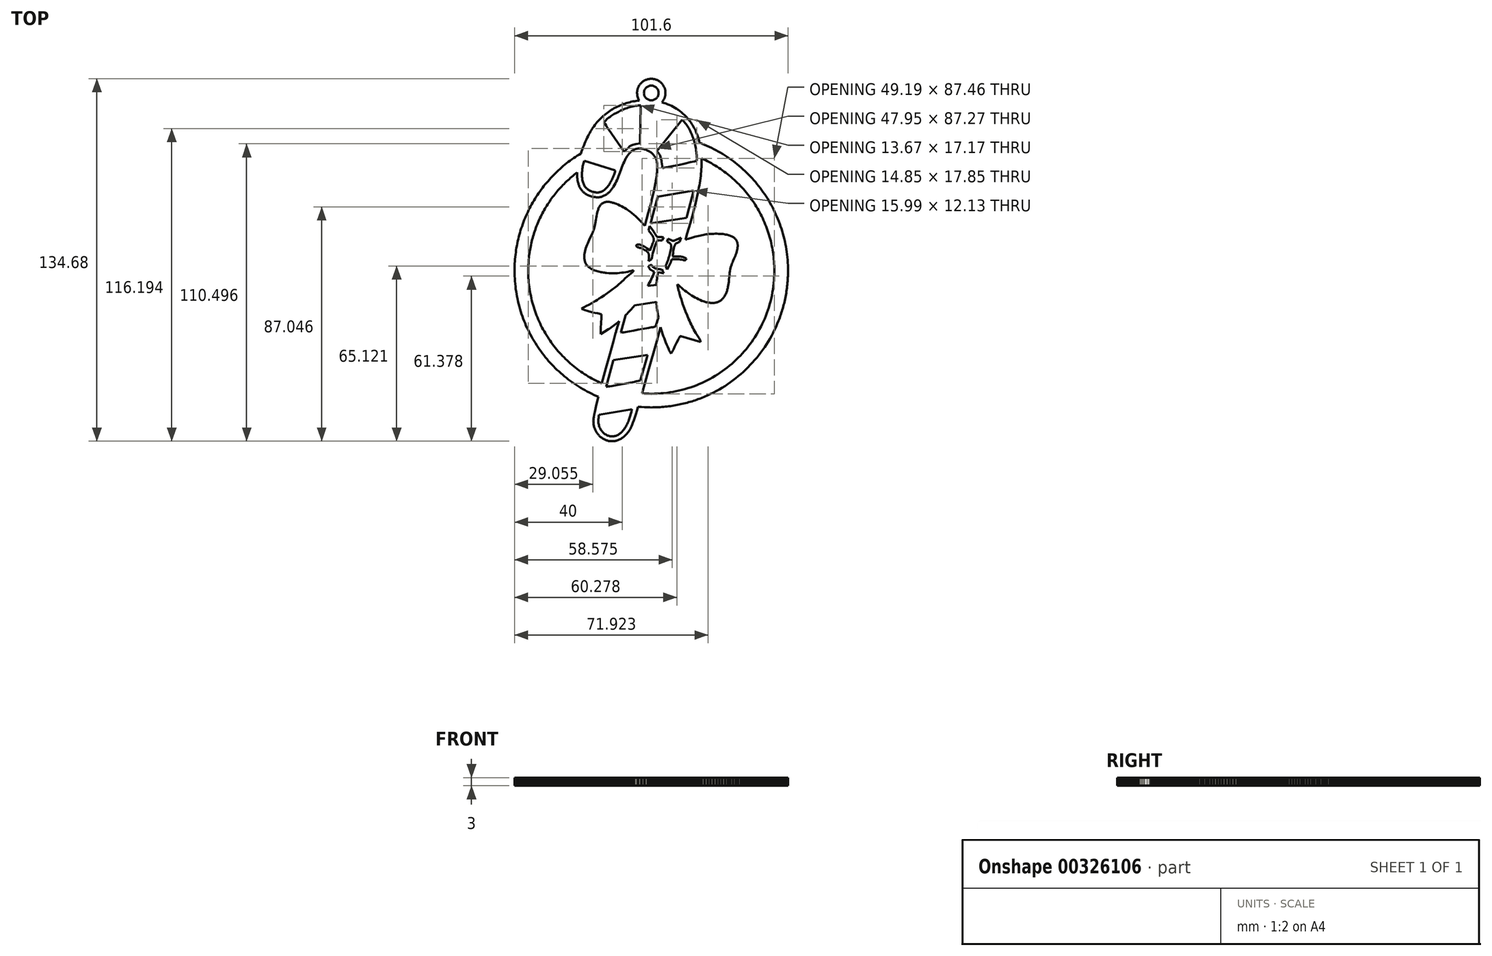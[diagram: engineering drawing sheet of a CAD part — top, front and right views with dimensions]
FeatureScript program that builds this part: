
annotation { "Feature Type Name" : "Feature", "Feature Type Description" : "" }
export const myFeature = defineFeature(function(context is Context, id is Id, definition is map)
    precondition{}
    {
        {
            var Q0;
            Q0=qCreatedBy(makeId("Top.planeOp"),FACE);
            var sketch = newSketch(context, id + "F0", { "sketchPlane" : qUnion([Q0])});
            skLineSegment(sketch, "E0", {"start": v(0.09, -1.72) * mm, "end": v(0.1, -1.8) * mm});
            skLineSegment(sketch, "E1", {"start": v(0.1, -1.8) * mm, "end": v(0.13, -1.9) * mm});
            skLineSegment(sketch, "E2", {"start": v(0.13, -1.9) * mm, "end": v(0.17, -2) * mm});
            skLineSegment(sketch, "E3", {"start": v(0.17, -2) * mm, "end": v(0.22, -2.09) * mm});
            skLineSegment(sketch, "E4", {"start": v(0.22, -2.09) * mm, "end": v(0.27, -2.18) * mm});
            skLineSegment(sketch, "E5", {"start": v(0.27, -2.18) * mm, "end": v(0.4, -2.34) * mm});
            skLineSegment(sketch, "E6", {"start": v(0.4, -2.34) * mm, "end": v(0.54, -2.5) * mm});
            skLineSegment(sketch, "E7", {"start": v(0.54, -2.5) * mm, "end": v(0.72, -2.64) * mm});
            skLineSegment(sketch, "E8", {"start": v(0.72, -2.64) * mm, "end": v(0.9, -2.77) * mm});
            skLineSegment(sketch, "E9", {"start": v(0.9, -2.77) * mm, "end": v(1.12, -2.89) * mm});
            skLineSegment(sketch, "E10", {"start": v(1.12, -2.89) * mm, "end": v(1.34, -3) * mm});
            skLineSegment(sketch, "E11", {"start": v(1.34, -3) * mm, "end": v(1.57, -3.09) * mm});
            skLineSegment(sketch, "E12", {"start": v(1.57, -3.09) * mm, "end": v(1.81, -3.17) * mm});
            skLineSegment(sketch, "E13", {"start": v(1.81, -3.17) * mm, "end": v(2.06, -3.24) * mm});
            skLineSegment(sketch, "E14", {"start": v(2.06, -3.24) * mm, "end": v(2.3, -3.3) * mm});
            skLineSegment(sketch, "E15", {"start": v(2.3, -3.3) * mm, "end": v(2.55, -3.35) * mm});
            skLineSegment(sketch, "E16", {"start": v(2.55, -3.35) * mm, "end": v(2.79, -3.4) * mm});
            skLineSegment(sketch, "E17", {"start": v(2.79, -3.4) * mm, "end": v(3.25, -3.45) * mm});
            skLineSegment(sketch, "E18", {"start": v(3.25, -3.45) * mm, "end": v(3.44, -3.46) * mm});
            skLineSegment(sketch, "E19", {"start": v(3.44, -3.46) * mm, "end": v(3.62, -3.47) * mm});
            skLineSegment(sketch, "E20", {"start": v(3.62, -3.47) * mm, "end": v(3.78, -3.46) * mm});
            skLineSegment(sketch, "E21", {"start": v(3.78, -3.46) * mm, "end": v(3.93, -3.45) * mm});
            skLineSegment(sketch, "E22", {"start": v(3.93, -3.45) * mm, "end": v(4.56, -4.93) * mm});
            skLineSegment(sketch, "E23", {"start": v(4.56, -4.93) * mm, "end": v(4.42, -4.87) * mm});
            skLineSegment(sketch, "E24", {"start": v(4.42, -4.87) * mm, "end": v(4.26, -4.82) * mm});
            skLineSegment(sketch, "E25", {"start": v(4.26, -4.82) * mm, "end": v(4.07, -4.78) * mm});
            skLineSegment(sketch, "E26", {"start": v(4.07, -4.78) * mm, "end": v(3.85, -4.74) * mm});
            skLineSegment(sketch, "E27", {"start": v(3.85, -4.74) * mm, "end": v(3.3, -4.67) * mm});
            skLineSegment(sketch, "E28", {"start": v(3.3, -4.67) * mm, "end": v(2.54, -4.6) * mm});
            skLineSegment(sketch, "E29", {"start": v(2.54, -4.6) * mm, "end": v(2.43, -5.17) * mm});
            skLineSegment(sketch, "E30", {"start": v(2.43, -5.17) * mm, "end": v(2.32, -5.74) * mm});
            skLineSegment(sketch, "E31", {"start": v(2.32, -5.74) * mm, "end": v(2.23, -6.32) * mm});
            skLineSegment(sketch, "E32", {"start": v(2.23, -6.32) * mm, "end": v(2.14, -6.9) * mm});
            skLineSegment(sketch, "E33", {"start": v(2.14, -6.9) * mm, "end": v(2.07, -7.48) * mm});
            skLineSegment(sketch, "E34", {"start": v(2.07, -7.48) * mm, "end": v(2, -8.06) * mm});
            skLineSegment(sketch, "E35", {"start": v(2, -8.06) * mm, "end": v(1.94, -8.64) * mm});
            skLineSegment(sketch, "E36", {"start": v(1.94, -8.64) * mm, "end": v(1.9, -9.23) * mm});
            skLineSegment(sketch, "E37", {"start": v(1.9, -9.23) * mm, "end": v(-1.28, -9.65) * mm});
            skLineSegment(sketch, "E38", {"start": v(-1.28, -9.65) * mm, "end": v(-0.94, -9.02) * mm});
            skLineSegment(sketch, "E39", {"start": v(-0.94, -9.02) * mm, "end": v(-0.61, -8.38) * mm});
            skLineSegment(sketch, "E40", {"start": v(-0.61, -8.38) * mm, "end": v(-0.3, -7.73) * mm});
            skLineSegment(sketch, "E41", {"start": v(-0.3, -7.73) * mm, "end": v(0.02, -7.08) * mm});
            skLineSegment(sketch, "E42", {"start": v(0.02, -7.08) * mm, "end": v(0.31, -6.43) * mm});
            skLineSegment(sketch, "E43", {"start": v(0.31, -6.43) * mm, "end": v(0.6, -5.77) * mm});
            skLineSegment(sketch, "E44", {"start": v(0.6, -5.77) * mm, "end": v(0.87, -5.1) * mm});
            skLineSegment(sketch, "E45", {"start": v(0.87, -5.1) * mm, "end": v(1.13, -4.44) * mm});
            skLineSegment(sketch, "E46", {"start": v(1.13, -4.44) * mm, "end": v(0.88, -4.27) * mm});
            skLineSegment(sketch, "E47", {"start": v(0.88, -4.27) * mm, "end": v(0.65, -4.12) * mm});
            skLineSegment(sketch, "E48", {"start": v(0.65, -4.12) * mm, "end": v(0.25, -3.88) * mm});
            skLineSegment(sketch, "E49", {"start": v(0.25, -3.88) * mm, "end": v(-0.08, -3.7) * mm});
            skLineSegment(sketch, "E50", {"start": v(-0.08, -3.7) * mm, "end": v(-0.22, -3.6) * mm});
            skLineSegment(sketch, "E51", {"start": v(-0.22, -3.6) * mm, "end": v(-0.35, -3.51) * mm});
            skLineSegment(sketch, "E52", {"start": v(-0.35, -3.51) * mm, "end": v(-0.47, -3.42) * mm});
            skLineSegment(sketch, "E53", {"start": v(-0.47, -3.42) * mm, "end": v(-0.57, -3.32) * mm});
            skLineSegment(sketch, "E54", {"start": v(-0.57, -3.32) * mm, "end": v(-0.67, -3.2) * mm});
            skLineSegment(sketch, "E55", {"start": v(-0.67, -3.2) * mm, "end": v(-0.76, -3.06) * mm});
            skLineSegment(sketch, "E56", {"start": v(-0.76, -3.06) * mm, "end": v(-0.84, -2.9) * mm});
            skLineSegment(sketch, "E57", {"start": v(-0.84, -2.9) * mm, "end": v(-0.92, -2.72) * mm});
            skLineSegment(sketch, "E58", {"start": v(-0.92, -2.72) * mm, "end": v(-1, -2.5) * mm});
            skLineSegment(sketch, "E59", {"start": v(-1, -2.5) * mm, "end": v(-1.06, -2.25) * mm});
            skLineSegment(sketch, "E60", {"start": v(-1.06, -2.25) * mm, "end": v(0.09, -1.72) * mm});
            skLineSegment(sketch, "E61", {"start": v(6.21, 7.92) * mm, "end": v(6.78, 7.62) * mm});
            skLineSegment(sketch, "E62", {"start": v(6.78, 7.62) * mm, "end": v(7.06, 7.47) * mm});
            skLineSegment(sketch, "E63", {"start": v(7.06, 7.47) * mm, "end": v(7.34, 7.34) * mm});
            skLineSegment(sketch, "E64", {"start": v(7.34, 7.34) * mm, "end": v(7.6, 7.22) * mm});
            skLineSegment(sketch, "E65", {"start": v(7.6, 7.22) * mm, "end": v(7.84, 7.14) * mm});
            skLineSegment(sketch, "E66", {"start": v(7.84, 7.14) * mm, "end": v(7.96, 7.12) * mm});
            skLineSegment(sketch, "E67", {"start": v(7.96, 7.12) * mm, "end": v(8.07, 7.1) * mm});
            skLineSegment(sketch, "E68", {"start": v(8.07, 7.1) * mm, "end": v(8.17, 7.1) * mm});
            skLineSegment(sketch, "E69", {"start": v(8.17, 7.1) * mm, "end": v(8.27, 7.12) * mm});
            skLineSegment(sketch, "E70", {"start": v(8.27, 7.12) * mm, "end": v(8.44, 7.17) * mm});
            skLineSegment(sketch, "E71", {"start": v(8.44, 7.17) * mm, "end": v(8.69, 7.27) * mm});
            skLineSegment(sketch, "E72", {"start": v(8.69, 7.27) * mm, "end": v(9.34, 7.55) * mm});
            skLineSegment(sketch, "E73", {"start": v(9.34, 7.55) * mm, "end": v(10.14, 7.92) * mm});
            skLineSegment(sketch, "E74", {"start": v(10.14, 7.92) * mm, "end": v(11.02, 8.32) * mm});
            skLineSegment(sketch, "E75", {"start": v(11.02, 8.32) * mm, "end": v(10.58, 6.79) * mm});
            skLineSegment(sketch, "E76", {"start": v(10.58, 6.79) * mm, "end": v(10.17, 6.6) * mm});
            skLineSegment(sketch, "E77", {"start": v(10.17, 6.6) * mm, "end": v(9.8, 6.43) * mm});
            skLineSegment(sketch, "E78", {"start": v(9.8, 6.43) * mm, "end": v(9.46, 6.25) * mm});
            skLineSegment(sketch, "E79", {"start": v(9.46, 6.25) * mm, "end": v(9.18, 6.08) * mm});
            skLineSegment(sketch, "E80", {"start": v(9.18, 6.08) * mm, "end": v(9.09, 6.02) * mm});
            skLineSegment(sketch, "E81", {"start": v(9.09, 6.02) * mm, "end": v(9, 5.94) * mm});
            skLineSegment(sketch, "E82", {"start": v(9, 5.94) * mm, "end": v(8.92, 5.85) * mm});
            skLineSegment(sketch, "E83", {"start": v(8.92, 5.85) * mm, "end": v(8.85, 5.75) * mm});
            skLineSegment(sketch, "E84", {"start": v(8.85, 5.75) * mm, "end": v(8.78, 5.65) * mm});
            skLineSegment(sketch, "E85", {"start": v(8.78, 5.65) * mm, "end": v(8.72, 5.53) * mm});
            skLineSegment(sketch, "E86", {"start": v(8.72, 5.53) * mm, "end": v(8.6, 5.27) * mm});
            skLineSegment(sketch, "E87", {"start": v(8.6, 5.27) * mm, "end": v(8.5, 4.98) * mm});
            skLineSegment(sketch, "E88", {"start": v(8.5, 4.98) * mm, "end": v(8.43, 4.67) * mm});
            skLineSegment(sketch, "E89", {"start": v(8.43, 4.67) * mm, "end": v(8.36, 4.33) * mm});
            skLineSegment(sketch, "E90", {"start": v(8.36, 4.33) * mm, "end": v(8.3, 3.99) * mm});
            skLineSegment(sketch, "E91", {"start": v(8.3, 3.99) * mm, "end": v(8.2, 3.27) * mm});
            skLineSegment(sketch, "E92", {"start": v(8.2, 3.27) * mm, "end": v(8.1, 2.56) * mm});
            skLineSegment(sketch, "E93", {"start": v(8.1, 2.56) * mm, "end": v(8.01, 1.9) * mm});
            skLineSegment(sketch, "E94", {"start": v(8.01, 1.9) * mm, "end": v(7.96, 1.6) * mm});
            skLineSegment(sketch, "E95", {"start": v(7.96, 1.6) * mm, "end": v(7.9, 1.32) * mm});
            skLineSegment(sketch, "E96", {"start": v(7.9, 1.32) * mm, "end": v(8.52, 1.34) * mm});
            skLineSegment(sketch, "E97", {"start": v(8.52, 1.34) * mm, "end": v(9.2, 1.35) * mm});
            skLineSegment(sketch, "E98", {"start": v(9.2, 1.35) * mm, "end": v(9.54, 1.36) * mm});
            skLineSegment(sketch, "E99", {"start": v(9.54, 1.36) * mm, "end": v(9.9, 1.35) * mm});
            skLineSegment(sketch, "E100", {"start": v(9.9, 1.35) * mm, "end": v(10.24, 1.33) * mm});
            skLineSegment(sketch, "E101", {"start": v(10.24, 1.33) * mm, "end": v(10.6, 1.3) * mm});
            skLineSegment(sketch, "E102", {"start": v(10.6, 1.3) * mm, "end": v(10.94, 1.27) * mm});
            skLineSegment(sketch, "E103", {"start": v(10.94, 1.27) * mm, "end": v(11.29, 1.22) * mm});
            skLineSegment(sketch, "E104", {"start": v(11.29, 1.22) * mm, "end": v(11.62, 1.15) * mm});
            skLineSegment(sketch, "E105", {"start": v(11.62, 1.15) * mm, "end": v(11.94, 1.06) * mm});
            skLineSegment(sketch, "E106", {"start": v(11.94, 1.06) * mm, "end": v(12.25, 0.95) * mm});
            skLineSegment(sketch, "E107", {"start": v(12.25, 0.95) * mm, "end": v(12.55, 0.82) * mm});
            skLineSegment(sketch, "E108", {"start": v(12.55, 0.82) * mm, "end": v(12.69, 0.74) * mm});
            skLineSegment(sketch, "E109", {"start": v(12.69, 0.74) * mm, "end": v(12.82, 0.66) * mm});
            skLineSegment(sketch, "E110", {"start": v(12.82, 0.66) * mm, "end": v(12.95, 0.58) * mm});
            skLineSegment(sketch, "E111", {"start": v(12.95, 0.58) * mm, "end": v(13.07, 0.48) * mm});
            skLineSegment(sketch, "E112", {"start": v(13.07, 0.48) * mm, "end": v(12.96, 0.27) * mm});
            skLineSegment(sketch, "E113", {"start": v(12.96, 0.27) * mm, "end": v(12.85, 0.11) * mm});
            skLineSegment(sketch, "E114", {"start": v(12.85, 0.11) * mm, "end": v(12.8, 0.05) * mm});
            skLineSegment(sketch, "E115", {"start": v(12.8, 0.05) * mm, "end": v(12.74, 0) * mm});
            skLineSegment(sketch, "E116", {"start": v(12.74, 0) * mm, "end": v(12.68, -0.03) * mm});
            skLineSegment(sketch, "E117", {"start": v(12.68, -0.03) * mm, "end": v(12.61, -0.06) * mm});
            skLineSegment(sketch, "E118", {"start": v(12.61, -0.06) * mm, "end": v(12.55, -0.08) * mm});
            skLineSegment(sketch, "E119", {"start": v(12.55, -0.08) * mm, "end": v(12.47, -0.09) * mm});
            skLineSegment(sketch, "E120", {"start": v(12.47, -0.09) * mm, "end": v(12.3, -0.08) * mm});
            skLineSegment(sketch, "E121", {"start": v(12.3, -0.08) * mm, "end": v(12.1, -0.06) * mm});
            skLineSegment(sketch, "E122", {"start": v(12.1, -0.06) * mm, "end": v(11.86, -0.01) * mm});
            skLineSegment(sketch, "E123", {"start": v(11.86, -0.01) * mm, "end": v(11.23, 0.1) * mm});
            skLineSegment(sketch, "E124", {"start": v(11.23, 0.1) * mm, "end": v(10.83, 0.17) * mm});
            skLineSegment(sketch, "E125", {"start": v(10.83, 0.17) * mm, "end": v(10.35, 0.23) * mm});
            skLineSegment(sketch, "E126", {"start": v(10.35, 0.23) * mm, "end": v(9.8, 0.27) * mm});
            skLineSegment(sketch, "E127", {"start": v(9.8, 0.27) * mm, "end": v(9.16, 0.3) * mm});
            skLineSegment(sketch, "E128", {"start": v(9.16, 0.3) * mm, "end": v(8.44, 0.29) * mm});
            skLineSegment(sketch, "E129", {"start": v(8.44, 0.29) * mm, "end": v(8.03, 0.27) * mm});
            skLineSegment(sketch, "E130", {"start": v(8.03, 0.27) * mm, "end": v(7.6, 0.25) * mm});
            skLineSegment(sketch, "E131", {"start": v(7.6, 0.25) * mm, "end": v(7.4, -0.37) * mm});
            skLineSegment(sketch, "E132", {"start": v(7.4, -0.37) * mm, "end": v(7.2, -0.9) * mm});
            skLineSegment(sketch, "E133", {"start": v(7.2, -0.9) * mm, "end": v(6.98, -1.39) * mm});
            skLineSegment(sketch, "E134", {"start": v(6.98, -1.39) * mm, "end": v(6.77, -1.82) * mm});
            skLineSegment(sketch, "E135", {"start": v(6.77, -1.82) * mm, "end": v(6.34, -2.65) * mm});
            skLineSegment(sketch, "E136", {"start": v(6.34, -2.65) * mm, "end": v(5.87, -3.5) * mm});
            skLineSegment(sketch, "E137", {"start": v(5.87, -3.5) * mm, "end": v(5.3, -2.17) * mm});
            skLineSegment(sketch, "E138", {"start": v(5.3, -2.17) * mm, "end": v(5.56, -1.66) * mm});
            skLineSegment(sketch, "E139", {"start": v(5.56, -1.66) * mm, "end": v(5.7, -1.37) * mm});
            skLineSegment(sketch, "E140", {"start": v(5.7, -1.37) * mm, "end": v(5.85, -1) * mm});
            skLineSegment(sketch, "E141", {"start": v(5.85, -1) * mm, "end": v(6.02, -0.57) * mm});
            skLineSegment(sketch, "E142", {"start": v(6.02, -0.57) * mm, "end": v(6.19, -0.08) * mm});
            skLineSegment(sketch, "E143", {"start": v(6.19, -0.08) * mm, "end": v(6.37, 0.44) * mm});
            skLineSegment(sketch, "E144", {"start": v(6.37, 0.44) * mm, "end": v(6.54, 1) * mm});
            skLineSegment(sketch, "E145", {"start": v(6.54, 1) * mm, "end": v(6.71, 1.58) * mm});
            skLineSegment(sketch, "E146", {"start": v(6.71, 1.58) * mm, "end": v(6.87, 2.17) * mm});
            skLineSegment(sketch, "E147", {"start": v(6.87, 2.17) * mm, "end": v(7.02, 2.75) * mm});
            skLineSegment(sketch, "E148", {"start": v(7.02, 2.75) * mm, "end": v(7.15, 3.32) * mm});
            skLineSegment(sketch, "E149", {"start": v(7.15, 3.32) * mm, "end": v(7.25, 3.87) * mm});
            skLineSegment(sketch, "E150", {"start": v(7.25, 3.87) * mm, "end": v(7.32, 4.38) * mm});
            skLineSegment(sketch, "E151", {"start": v(7.32, 4.38) * mm, "end": v(7.35, 4.62) * mm});
            skLineSegment(sketch, "E152", {"start": v(7.35, 4.62) * mm, "end": v(7.36, 4.84) * mm});
            skLineSegment(sketch, "E153", {"start": v(7.36, 4.84) * mm, "end": v(7.37, 5.05) * mm});
            skLineSegment(sketch, "E154", {"start": v(7.37, 5.05) * mm, "end": v(7.37, 5.24) * mm});
            skLineSegment(sketch, "E155", {"start": v(7.37, 5.24) * mm, "end": v(7.36, 5.42) * mm});
            skLineSegment(sketch, "E156", {"start": v(7.36, 5.42) * mm, "end": v(7.33, 5.58) * mm});
            skLineSegment(sketch, "E157", {"start": v(7.33, 5.58) * mm, "end": v(7.3, 5.72) * mm});
            skLineSegment(sketch, "E158", {"start": v(7.3, 5.72) * mm, "end": v(7.25, 5.83) * mm});
            skLineSegment(sketch, "E159", {"start": v(7.25, 5.83) * mm, "end": v(7.2, 5.9) * mm});
            skLineSegment(sketch, "E160", {"start": v(7.2, 5.9) * mm, "end": v(7.15, 5.98) * mm});
            skLineSegment(sketch, "E161", {"start": v(7.15, 5.98) * mm, "end": v(7.03, 6.12) * mm});
            skLineSegment(sketch, "E162", {"start": v(7.03, 6.12) * mm, "end": v(6.87, 6.25) * mm});
            skLineSegment(sketch, "E163", {"start": v(6.87, 6.25) * mm, "end": v(6.7, 6.38) * mm});
            skLineSegment(sketch, "E164", {"start": v(6.7, 6.38) * mm, "end": v(6.5, 6.5) * mm});
            skLineSegment(sketch, "E165", {"start": v(6.5, 6.5) * mm, "end": v(6.29, 6.6) * mm});
            skLineSegment(sketch, "E166", {"start": v(6.29, 6.6) * mm, "end": v(6.06, 6.71) * mm});
            skLineSegment(sketch, "E167", {"start": v(6.06, 6.71) * mm, "end": v(5.83, 6.8) * mm});
            skLineSegment(sketch, "E168", {"start": v(5.83, 6.8) * mm, "end": v(6.21, 7.92) * mm});
            skLineSegment(sketch, "E169", {"start": v(2.62, -21.33) * mm, "end": v(1.71, -24.54) * mm});
            skLineSegment(sketch, "E170", {"start": v(1.71, -24.54) * mm, "end": v(1.6, -24.62) * mm});
            skLineSegment(sketch, "E171", {"start": v(1.6, -24.62) * mm, "end": v(1.49, -24.69) * mm});
            skLineSegment(sketch, "E172", {"start": v(1.49, -24.69) * mm, "end": v(1.37, -24.74) * mm});
            skLineSegment(sketch, "E173", {"start": v(1.37, -24.74) * mm, "end": v(1.25, -24.8) * mm});
            skLineSegment(sketch, "E174", {"start": v(1.25, -24.8) * mm, "end": v(1.13, -24.84) * mm});
            skLineSegment(sketch, "E175", {"start": v(1.13, -24.84) * mm, "end": v(1, -24.87) * mm});
            skLineSegment(sketch, "E176", {"start": v(1, -24.87) * mm, "end": v(0.7, -24.93) * mm});
            skLineSegment(sketch, "E177", {"start": v(0.7, -24.93) * mm, "end": v(-0.03, -25.04) * mm});
            skLineSegment(sketch, "E178", {"start": v(-0.03, -25.04) * mm, "end": v(-0.5, -25.1) * mm});
            skLineSegment(sketch, "E179", {"start": v(-0.5, -25.1) * mm, "end": v(-1.05, -25.2) * mm});
            skLineSegment(sketch, "E180", {"start": v(-1.05, -25.2) * mm, "end": v(-3.34, -25.63) * mm});
            skLineSegment(sketch, "E181", {"start": v(-3.34, -25.63) * mm, "end": v(-4.9, -25.93) * mm});
            skLineSegment(sketch, "E182", {"start": v(-4.9, -25.93) * mm, "end": v(-6.54, -26.24) * mm});
            skLineSegment(sketch, "E183", {"start": v(-6.54, -26.24) * mm, "end": v(-8.14, -26.53) * mm});
            skLineSegment(sketch, "E184", {"start": v(-8.14, -26.53) * mm, "end": v(-9.56, -26.77) * mm});
            skLineSegment(sketch, "E185", {"start": v(-9.56, -26.77) * mm, "end": v(-10.16, -26.86) * mm});
            skLineSegment(sketch, "E186", {"start": v(-10.16, -26.86) * mm, "end": v(-10.66, -26.92) * mm});
            skLineSegment(sketch, "E187", {"start": v(-10.66, -26.92) * mm, "end": v(-11.05, -26.95) * mm});
            skLineSegment(sketch, "E188", {"start": v(-11.05, -26.95) * mm, "end": v(-11.2, -26.96) * mm});
            skLineSegment(sketch, "E189", {"start": v(-11.2, -26.96) * mm, "end": v(-11.3, -26.95) * mm});
            skLineSegment(sketch, "E190", {"start": v(-11.3, -26.95) * mm, "end": v(-9.46, -20.43) * mm});
            skLineSegment(sketch, "E191", {"start": v(-9.46, -20.43) * mm, "end": v(-9.03, -20) * mm});
            skLineSegment(sketch, "E192", {"start": v(-9.03, -20) * mm, "end": v(-8.6, -19.57) * mm});
            skLineSegment(sketch, "E193", {"start": v(-8.6, -19.57) * mm, "end": v(-8.19, -19.13) * mm});
            skLineSegment(sketch, "E194", {"start": v(-8.19, -19.13) * mm, "end": v(-7.77, -18.68) * mm});
            skLineSegment(sketch, "E195", {"start": v(-7.77, -18.68) * mm, "end": v(-7.36, -18.23) * mm});
            skLineSegment(sketch, "E196", {"start": v(-7.36, -18.23) * mm, "end": v(-6.96, -17.77) * mm});
            skLineSegment(sketch, "E197", {"start": v(-6.96, -17.77) * mm, "end": v(-6.56, -17.3) * mm});
            skLineSegment(sketch, "E198", {"start": v(-6.56, -17.3) * mm, "end": v(-6.17, -16.83) * mm});
            skLineSegment(sketch, "E199", {"start": v(-6.17, -16.83) * mm, "end": v(1.87, -15.61) * mm});
            skLineSegment(sketch, "E200", {"start": v(1.87, -15.61) * mm, "end": v(1.92, -16.33) * mm});
            skLineSegment(sketch, "E201", {"start": v(1.92, -16.33) * mm, "end": v(2, -17.05) * mm});
            skLineSegment(sketch, "E202", {"start": v(2, -17.05) * mm, "end": v(2.07, -17.77) * mm});
            skLineSegment(sketch, "E203", {"start": v(2.07, -17.77) * mm, "end": v(2.16, -18.49) * mm});
            skLineSegment(sketch, "E204", {"start": v(2.16, -18.49) * mm, "end": v(2.26, -19.2) * mm});
            skLineSegment(sketch, "E205", {"start": v(2.26, -19.2) * mm, "end": v(2.37, -19.91) * mm});
            skLineSegment(sketch, "E206", {"start": v(2.37, -19.91) * mm, "end": v(2.49, -20.62) * mm});
            skLineSegment(sketch, "E207", {"start": v(2.49, -20.62) * mm, "end": v(2.62, -21.33) * mm});
            skLineSegment(sketch, "E208", {"start": v(-1.63, -36.34) * mm, "end": v(-1.35, -35.33) * mm});
            skLineSegment(sketch, "E209", {"start": v(-1.35, -35.33) * mm, "end": v(-14.05, -37.2) * mm});
            skLineSegment(sketch, "E210", {"start": v(-14.05, -37.2) * mm, "end": v(-16.7, -47.05) * mm});
            skLineSegment(sketch, "E211", {"start": v(-16.7, -47.05) * mm, "end": v(-16.62, -47.06) * mm});
            skLineSegment(sketch, "E212", {"start": v(-16.62, -47.06) * mm, "end": v(-16.47, -47.06) * mm});
            skLineSegment(sketch, "E213", {"start": v(-16.47, -47.06) * mm, "end": v(-16.03, -47.01) * mm});
            skLineSegment(sketch, "E214", {"start": v(-16.03, -47.01) * mm, "end": v(-15.4, -46.93) * mm});
            skLineSegment(sketch, "E215", {"start": v(-15.4, -46.93) * mm, "end": v(-14.61, -46.8) * mm});
            skLineSegment(sketch, "E216", {"start": v(-14.61, -46.8) * mm, "end": v(-12.7, -46.48) * mm});
            skLineSegment(sketch, "E217", {"start": v(-12.7, -46.48) * mm, "end": v(-10.53, -46.09) * mm});
            skLineSegment(sketch, "E218", {"start": v(-10.53, -46.09) * mm, "end": v(-8.34, -45.67) * mm});
            skLineSegment(sketch, "E219", {"start": v(-8.34, -45.67) * mm, "end": v(-6.37, -45.27) * mm});
            skLineSegment(sketch, "E220", {"start": v(-6.37, -45.27) * mm, "end": v(-5.54, -45.1) * mm});
            skLineSegment(sketch, "E221", {"start": v(-5.54, -45.1) * mm, "end": v(-4.86, -44.95) * mm});
            skLineSegment(sketch, "E222", {"start": v(-4.86, -44.95) * mm, "end": v(-4.35, -44.82) * mm});
            skLineSegment(sketch, "E223", {"start": v(-4.35, -44.82) * mm, "end": v(-4.04, -44.73) * mm});
            skLineSegment(sketch, "E224", {"start": v(-4.04, -44.73) * mm, "end": v(-1.63, -36.34) * mm});
            skLineSegment(sketch, "E225", {"start": v(-19.42, -57.55) * mm, "end": v(-19.52, -58.08) * mm});
            skLineSegment(sketch, "E226", {"start": v(-19.52, -58.08) * mm, "end": v(-19.6, -58.6) * mm});
            skLineSegment(sketch, "E227", {"start": v(-19.6, -58.6) * mm, "end": v(-19.64, -59.1) * mm});
            skLineSegment(sketch, "E228", {"start": v(-19.64, -59.1) * mm, "end": v(-19.66, -59.58) * mm});
            skLineSegment(sketch, "E229", {"start": v(-19.66, -59.58) * mm, "end": v(-19.65, -60.04) * mm});
            skLineSegment(sketch, "E230", {"start": v(-19.65, -60.04) * mm, "end": v(-19.62, -60.48) * mm});
            skLineSegment(sketch, "E231", {"start": v(-19.62, -60.48) * mm, "end": v(-19.56, -60.9) * mm});
            skLineSegment(sketch, "E232", {"start": v(-19.56, -60.9) * mm, "end": v(-19.47, -61.32) * mm});
            skLineSegment(sketch, "E233", {"start": v(-19.47, -61.32) * mm, "end": v(-19.37, -61.7) * mm});
            skLineSegment(sketch, "E234", {"start": v(-19.37, -61.7) * mm, "end": v(-19.24, -62.08) * mm});
            skLineSegment(sketch, "E235", {"start": v(-19.24, -62.08) * mm, "end": v(-19.1, -62.43) * mm});
            skLineSegment(sketch, "E236", {"start": v(-19.1, -62.43) * mm, "end": v(-18.93, -62.76) * mm});
            skLineSegment(sketch, "E237", {"start": v(-18.93, -62.76) * mm, "end": v(-18.74, -63.08) * mm});
            skLineSegment(sketch, "E238", {"start": v(-18.74, -63.08) * mm, "end": v(-18.54, -63.37) * mm});
            skLineSegment(sketch, "E239", {"start": v(-18.54, -63.37) * mm, "end": v(-18.33, -63.65) * mm});
            skLineSegment(sketch, "E240", {"start": v(-18.33, -63.65) * mm, "end": v(-18.1, -63.9) * mm});
            skLineSegment(sketch, "E241", {"start": v(-18.1, -63.9) * mm, "end": v(-17.86, -64.15) * mm});
            skLineSegment(sketch, "E242", {"start": v(-17.86, -64.15) * mm, "end": v(-17.61, -64.37) * mm});
            skLineSegment(sketch, "E243", {"start": v(-17.61, -64.37) * mm, "end": v(-17.35, -64.57) * mm});
            skLineSegment(sketch, "E244", {"start": v(-17.35, -64.57) * mm, "end": v(-17.08, -64.75) * mm});
            skLineSegment(sketch, "E245", {"start": v(-17.08, -64.75) * mm, "end": v(-16.8, -64.91) * mm});
            skLineSegment(sketch, "E246", {"start": v(-16.8, -64.91) * mm, "end": v(-16.52, -65.06) * mm});
            skLineSegment(sketch, "E247", {"start": v(-16.52, -65.06) * mm, "end": v(-16.23, -65.18) * mm});
            skLineSegment(sketch, "E248", {"start": v(-16.23, -65.18) * mm, "end": v(-15.93, -65.29) * mm});
            skLineSegment(sketch, "E249", {"start": v(-15.93, -65.29) * mm, "end": v(-15.63, -65.37) * mm});
            skLineSegment(sketch, "E250", {"start": v(-15.63, -65.37) * mm, "end": v(-15.34, -65.44) * mm});
            skLineSegment(sketch, "E251", {"start": v(-15.34, -65.44) * mm, "end": v(-15.04, -65.49) * mm});
            skLineSegment(sketch, "E252", {"start": v(-15.04, -65.49) * mm, "end": v(-14.74, -65.52) * mm});
            skLineSegment(sketch, "E253", {"start": v(-14.74, -65.52) * mm, "end": v(-14.44, -65.52) * mm});
            skLineSegment(sketch, "E254", {"start": v(-14.44, -65.52) * mm, "end": v(-14.15, -65.51) * mm});
            skLineSegment(sketch, "E255", {"start": v(-14.15, -65.51) * mm, "end": v(-13.86, -65.48) * mm});
            skLineSegment(sketch, "E256", {"start": v(-13.86, -65.48) * mm, "end": v(-13.58, -65.43) * mm});
            skLineSegment(sketch, "E257", {"start": v(-13.58, -65.43) * mm, "end": v(-13.26, -65.35) * mm});
            skLineSegment(sketch, "E258", {"start": v(-13.26, -65.35) * mm, "end": v(-12.95, -65.24) * mm});
            skLineSegment(sketch, "E259", {"start": v(-12.95, -65.24) * mm, "end": v(-12.65, -65.11) * mm});
            skLineSegment(sketch, "E260", {"start": v(-12.65, -65.11) * mm, "end": v(-12.35, -64.96) * mm});
            skLineSegment(sketch, "E261", {"start": v(-12.35, -64.96) * mm, "end": v(-12.07, -64.8) * mm});
            skLineSegment(sketch, "E262", {"start": v(-12.07, -64.8) * mm, "end": v(-11.79, -64.6) * mm});
            skLineSegment(sketch, "E263", {"start": v(-11.79, -64.6) * mm, "end": v(-11.52, -64.4) * mm});
            skLineSegment(sketch, "E264", {"start": v(-11.52, -64.4) * mm, "end": v(-11.25, -64.17) * mm});
            skLineSegment(sketch, "E265", {"start": v(-11.25, -64.17) * mm, "end": v(-11, -63.93) * mm});
            skLineSegment(sketch, "E266", {"start": v(-11, -63.93) * mm, "end": v(-10.75, -63.67) * mm});
            skLineSegment(sketch, "E267", {"start": v(-10.75, -63.67) * mm, "end": v(-10.51, -63.4) * mm});
            skLineSegment(sketch, "E268", {"start": v(-10.51, -63.4) * mm, "end": v(-10.28, -63.1) * mm});
            skLineSegment(sketch, "E269", {"start": v(-10.28, -63.1) * mm, "end": v(-10.06, -62.8) * mm});
            skLineSegment(sketch, "E270", {"start": v(-10.06, -62.8) * mm, "end": v(-9.84, -62.5) * mm});
            skLineSegment(sketch, "E271", {"start": v(-9.84, -62.5) * mm, "end": v(-9.63, -62.16) * mm});
            skLineSegment(sketch, "E272", {"start": v(-9.63, -62.16) * mm, "end": v(-9.43, -61.82) * mm});
            skLineSegment(sketch, "E273", {"start": v(-9.43, -61.82) * mm, "end": v(-9.24, -61.47) * mm});
            skLineSegment(sketch, "E274", {"start": v(-9.24, -61.47) * mm, "end": v(-9.05, -61.11) * mm});
            skLineSegment(sketch, "E275", {"start": v(-9.05, -61.11) * mm, "end": v(-8.87, -60.74) * mm});
            skLineSegment(sketch, "E276", {"start": v(-8.87, -60.74) * mm, "end": v(-8.7, -60.36) * mm});
            skLineSegment(sketch, "E277", {"start": v(-8.7, -60.36) * mm, "end": v(-8.54, -59.98) * mm});
            skLineSegment(sketch, "E278", {"start": v(-8.54, -59.98) * mm, "end": v(-8.38, -59.59) * mm});
            skLineSegment(sketch, "E279", {"start": v(-8.38, -59.59) * mm, "end": v(-8.23, -59.2) * mm});
            skLineSegment(sketch, "E280", {"start": v(-8.23, -59.2) * mm, "end": v(-8.09, -58.79) * mm});
            skLineSegment(sketch, "E281", {"start": v(-8.09, -58.79) * mm, "end": v(-7.95, -58.38) * mm});
            skLineSegment(sketch, "E282", {"start": v(-7.95, -58.38) * mm, "end": v(-7.82, -57.97) * mm});
            skLineSegment(sketch, "E283", {"start": v(-7.82, -57.97) * mm, "end": v(-7.59, -57.14) * mm});
            skLineSegment(sketch, "E284", {"start": v(-7.59, -57.14) * mm, "end": v(-7.38, -56.31) * mm});
            skLineSegment(sketch, "E285", {"start": v(-7.38, -56.31) * mm, "end": v(-7.2, -55.48) * mm});
            skLineSegment(sketch, "E286", {"start": v(-7.2, -55.48) * mm, "end": v(-19.42, -57.55) * mm});
            skLineSegment(sketch, "E287", {"start": v(-0.56, 12.57) * mm, "end": v(-0.15, 12.03) * mm});
            skLineSegment(sketch, "E288", {"start": v(-0.15, 12.03) * mm, "end": v(0.21, 11.51) * mm});
            skLineSegment(sketch, "E289", {"start": v(0.21, 11.51) * mm, "end": v(0.85, 10.54) * mm});
            skLineSegment(sketch, "E290", {"start": v(0.85, 10.54) * mm, "end": v(1.16, 10.05) * mm});
            skLineSegment(sketch, "E291", {"start": v(1.16, 10.05) * mm, "end": v(1.49, 9.56) * mm});
            skLineSegment(sketch, "E292", {"start": v(1.49, 9.56) * mm, "end": v(1.84, 9.06) * mm});
            skLineSegment(sketch, "E293", {"start": v(1.84, 9.06) * mm, "end": v(2.24, 8.53) * mm});
            skLineSegment(sketch, "E294", {"start": v(2.24, 8.53) * mm, "end": v(2.84, 8.5) * mm});
            skLineSegment(sketch, "E295", {"start": v(2.84, 8.5) * mm, "end": v(3.4, 8.5) * mm});
            skLineSegment(sketch, "E296", {"start": v(3.4, 8.5) * mm, "end": v(3.95, 8.49) * mm});
            skLineSegment(sketch, "E297", {"start": v(3.95, 8.49) * mm, "end": v(4.23, 8.47) * mm});
            skLineSegment(sketch, "E298", {"start": v(4.23, 8.47) * mm, "end": v(4.52, 8.43) * mm});
            skLineSegment(sketch, "E299", {"start": v(4.52, 8.43) * mm, "end": v(4.1, 7.24) * mm});
            skLineSegment(sketch, "E300", {"start": v(4.1, 7.24) * mm, "end": v(3.48, 7.3) * mm});
            skLineSegment(sketch, "E301", {"start": v(3.48, 7.3) * mm, "end": v(3.22, 7.33) * mm});
            skLineSegment(sketch, "E302", {"start": v(3.22, 7.33) * mm, "end": v(3, 7.34) * mm});
            skLineSegment(sketch, "E303", {"start": v(3, 7.34) * mm, "end": v(2.8, 7.33) * mm});
            skLineSegment(sketch, "E304", {"start": v(2.8, 7.33) * mm, "end": v(2.63, 7.32) * mm});
            skLineSegment(sketch, "E305", {"start": v(2.63, 7.32) * mm, "end": v(2.49, 7.28) * mm});
            skLineSegment(sketch, "E306", {"start": v(2.49, 7.28) * mm, "end": v(2.36, 7.22) * mm});
            skLineSegment(sketch, "E307", {"start": v(2.36, 7.22) * mm, "end": v(2.25, 7.14) * mm});
            skLineSegment(sketch, "E308", {"start": v(2.25, 7.14) * mm, "end": v(2.15, 7.03) * mm});
            skLineSegment(sketch, "E309", {"start": v(2.15, 7.03) * mm, "end": v(2.05, 6.9) * mm});
            skLineSegment(sketch, "E310", {"start": v(2.05, 6.9) * mm, "end": v(1.96, 6.73) * mm});
            skLineSegment(sketch, "E311", {"start": v(1.96, 6.73) * mm, "end": v(1.87, 6.54) * mm});
            skLineSegment(sketch, "E312", {"start": v(1.87, 6.54) * mm, "end": v(1.77, 6.3) * mm});
            skLineSegment(sketch, "E313", {"start": v(1.77, 6.3) * mm, "end": v(1.56, 5.73) * mm});
            skLineSegment(sketch, "E314", {"start": v(1.56, 5.73) * mm, "end": v(1.38, 5.22) * mm});
            skLineSegment(sketch, "E315", {"start": v(1.38, 5.22) * mm, "end": v(1.18, 4.63) * mm});
            skLineSegment(sketch, "E316", {"start": v(1.18, 4.63) * mm, "end": v(0.97, 3.97) * mm});
            skLineSegment(sketch, "E317", {"start": v(0.97, 3.97) * mm, "end": v(0.77, 3.25) * mm});
            skLineSegment(sketch, "E318", {"start": v(0.77, 3.25) * mm, "end": v(0.57, 2.5) * mm});
            skLineSegment(sketch, "E319", {"start": v(0.57, 2.5) * mm, "end": v(0.39, 1.73) * mm});
            skLineSegment(sketch, "E320", {"start": v(0.39, 1.73) * mm, "end": v(0.23, 0.97) * mm});
            skLineSegment(sketch, "E321", {"start": v(0.23, 0.97) * mm, "end": v(0.17, 0.6) * mm});
            skLineSegment(sketch, "E322", {"start": v(0.17, 0.6) * mm, "end": v(0.12, 0.24) * mm});
            skLineSegment(sketch, "E323", {"start": v(0.12, 0.24) * mm, "end": v(-1.02, -0.3) * mm});
            skLineSegment(sketch, "E324", {"start": v(-1.02, -0.3) * mm, "end": v(-0.93, 0.58) * mm});
            skLineSegment(sketch, "E325", {"start": v(-0.93, 0.58) * mm, "end": v(-0.9, 0.95) * mm});
            skLineSegment(sketch, "E326", {"start": v(-0.9, 0.95) * mm, "end": v(-0.87, 1.3) * mm});
            skLineSegment(sketch, "E327", {"start": v(-0.87, 1.3) * mm, "end": v(-0.86, 1.6) * mm});
            skLineSegment(sketch, "E328", {"start": v(-0.86, 1.6) * mm, "end": v(-0.88, 1.88) * mm});
            skLineSegment(sketch, "E329", {"start": v(-0.88, 1.88) * mm, "end": v(-0.92, 2.13) * mm});
            skLineSegment(sketch, "E330", {"start": v(-0.92, 2.13) * mm, "end": v(-0.95, 2.25) * mm});
            skLineSegment(sketch, "E331", {"start": v(-0.95, 2.25) * mm, "end": v(-0.98, 2.36) * mm});
            skLineSegment(sketch, "E332", {"start": v(-0.98, 2.36) * mm, "end": v(-1.03, 2.47) * mm});
            skLineSegment(sketch, "E333", {"start": v(-1.03, 2.47) * mm, "end": v(-1.08, 2.58) * mm});
            skLineSegment(sketch, "E334", {"start": v(-1.08, 2.58) * mm, "end": v(-1.14, 2.68) * mm});
            skLineSegment(sketch, "E335", {"start": v(-1.14, 2.68) * mm, "end": v(-1.2, 2.78) * mm});
            skLineSegment(sketch, "E336", {"start": v(-1.2, 2.78) * mm, "end": v(-1.28, 2.88) * mm});
            skLineSegment(sketch, "E337", {"start": v(-1.28, 2.88) * mm, "end": v(-1.37, 2.98) * mm});
            skLineSegment(sketch, "E338", {"start": v(-1.37, 2.98) * mm, "end": v(-1.58, 3.17) * mm});
            skLineSegment(sketch, "E339", {"start": v(-1.58, 3.17) * mm, "end": v(-1.83, 3.37) * mm});
            skLineSegment(sketch, "E340", {"start": v(-1.83, 3.37) * mm, "end": v(-2.12, 3.56) * mm});
            skLineSegment(sketch, "E341", {"start": v(-2.12, 3.56) * mm, "end": v(-2.47, 3.77) * mm});
            skLineSegment(sketch, "E342", {"start": v(-2.47, 3.77) * mm, "end": v(-2.87, 3.99) * mm});
            skLineSegment(sketch, "E343", {"start": v(-2.87, 3.99) * mm, "end": v(-3.23, 4.16) * mm});
            skLineSegment(sketch, "E344", {"start": v(-3.23, 4.16) * mm, "end": v(-3.54, 4.3) * mm});
            skLineSegment(sketch, "E345", {"start": v(-3.54, 4.3) * mm, "end": v(-3.87, 4.42) * mm});
            skLineSegment(sketch, "E346", {"start": v(-3.87, 4.42) * mm, "end": v(-4.25, 4.54) * mm});
            skLineSegment(sketch, "E347", {"start": v(-4.25, 4.54) * mm, "end": v(-4.6, 4.64) * mm});
            skLineSegment(sketch, "E348", {"start": v(-4.6, 4.64) * mm, "end": v(-4.86, 4.7) * mm});
            skLineSegment(sketch, "E349", {"start": v(-4.86, 4.7) * mm, "end": v(-5.07, 4.76) * mm});
            skLineSegment(sketch, "E350", {"start": v(-5.07, 4.76) * mm, "end": v(-5.16, 4.78) * mm});
            skLineSegment(sketch, "E351", {"start": v(-5.16, 4.78) * mm, "end": v(-5.23, 4.81) * mm});
            skLineSegment(sketch, "E352", {"start": v(-5.23, 4.81) * mm, "end": v(-5.3, 4.85) * mm});
            skLineSegment(sketch, "E353", {"start": v(-5.3, 4.85) * mm, "end": v(-5.36, 4.9) * mm});
            skLineSegment(sketch, "E354", {"start": v(-5.36, 4.9) * mm, "end": v(-5.4, 4.95) * mm});
            skLineSegment(sketch, "E355", {"start": v(-5.4, 4.95) * mm, "end": v(-5.45, 5.02) * mm});
            skLineSegment(sketch, "E356", {"start": v(-5.45, 5.02) * mm, "end": v(-5.5, 5.1) * mm});
            skLineSegment(sketch, "E357", {"start": v(-5.5, 5.1) * mm, "end": v(-5.53, 5.2) * mm});
            skLineSegment(sketch, "E358", {"start": v(-5.53, 5.2) * mm, "end": v(-5.61, 5.48) * mm});
            skLineSegment(sketch, "E359", {"start": v(-5.61, 5.48) * mm, "end": v(-5.48, 5.57) * mm});
            skLineSegment(sketch, "E360", {"start": v(-5.48, 5.57) * mm, "end": v(-5.34, 5.64) * mm});
            skLineSegment(sketch, "E361", {"start": v(-5.34, 5.64) * mm, "end": v(-5.2, 5.7) * mm});
            skLineSegment(sketch, "E362", {"start": v(-5.2, 5.7) * mm, "end": v(-5.05, 5.74) * mm});
            skLineSegment(sketch, "E363", {"start": v(-5.05, 5.74) * mm, "end": v(-4.89, 5.76) * mm});
            skLineSegment(sketch, "E364", {"start": v(-4.89, 5.76) * mm, "end": v(-4.72, 5.76) * mm});
            skLineSegment(sketch, "E365", {"start": v(-4.72, 5.76) * mm, "end": v(-4.55, 5.75) * mm});
            skLineSegment(sketch, "E366", {"start": v(-4.55, 5.75) * mm, "end": v(-4.38, 5.73) * mm});
            skLineSegment(sketch, "E367", {"start": v(-4.38, 5.73) * mm, "end": v(-4.2, 5.7) * mm});
            skLineSegment(sketch, "E368", {"start": v(-4.2, 5.7) * mm, "end": v(-4.02, 5.65) * mm});
            skLineSegment(sketch, "E369", {"start": v(-4.02, 5.65) * mm, "end": v(-3.83, 5.6) * mm});
            skLineSegment(sketch, "E370", {"start": v(-3.83, 5.6) * mm, "end": v(-3.65, 5.52) * mm});
            skLineSegment(sketch, "E371", {"start": v(-3.65, 5.52) * mm, "end": v(-3.27, 5.36) * mm});
            skLineSegment(sketch, "E372", {"start": v(-3.27, 5.36) * mm, "end": v(-2.9, 5.17) * mm});
            skLineSegment(sketch, "E373", {"start": v(-2.9, 5.17) * mm, "end": v(-2.52, 4.96) * mm});
            skLineSegment(sketch, "E374", {"start": v(-2.52, 4.96) * mm, "end": v(-2.16, 4.73) * mm});
            skLineSegment(sketch, "E375", {"start": v(-2.16, 4.73) * mm, "end": v(-1.8, 4.5) * mm});
            skLineSegment(sketch, "E376", {"start": v(-1.8, 4.5) * mm, "end": v(-1.48, 4.27) * mm});
            skLineSegment(sketch, "E377", {"start": v(-1.48, 4.27) * mm, "end": v(-0.9, 3.85) * mm});
            skLineSegment(sketch, "E378", {"start": v(-0.9, 3.85) * mm, "end": v(-0.45, 3.52) * mm});
            skLineSegment(sketch, "E379", {"start": v(-0.45, 3.52) * mm, "end": v(-0.34, 3.9) * mm});
            skLineSegment(sketch, "E380", {"start": v(-0.34, 3.9) * mm, "end": v(-0.23, 4.24) * mm});
            skLineSegment(sketch, "E381", {"start": v(-0.23, 4.24) * mm, "end": v(-0.01, 4.87) * mm});
            skLineSegment(sketch, "E382", {"start": v(-0.01, 4.87) * mm, "end": v(0.2, 5.4) * mm});
            skLineSegment(sketch, "E383", {"start": v(0.2, 5.4) * mm, "end": v(0.4, 5.87) * mm});
            skLineSegment(sketch, "E384", {"start": v(0.4, 5.87) * mm, "end": v(0.58, 6.27) * mm});
            skLineSegment(sketch, "E385", {"start": v(0.58, 6.27) * mm, "end": v(0.73, 6.63) * mm});
            skLineSegment(sketch, "E386", {"start": v(0.73, 6.63) * mm, "end": v(0.79, 6.8) * mm});
            skLineSegment(sketch, "E387", {"start": v(0.79, 6.8) * mm, "end": v(0.84, 6.96) * mm});
            skLineSegment(sketch, "E388", {"start": v(0.84, 6.96) * mm, "end": v(0.88, 7.12) * mm});
            skLineSegment(sketch, "E389", {"start": v(0.88, 7.12) * mm, "end": v(0.9, 7.28) * mm});
            skLineSegment(sketch, "E390", {"start": v(0.9, 7.28) * mm, "end": v(0.92, 7.44) * mm});
            skLineSegment(sketch, "E391", {"start": v(0.92, 7.44) * mm, "end": v(0.93, 7.6) * mm});
            skLineSegment(sketch, "E392", {"start": v(0.93, 7.6) * mm, "end": v(0.91, 7.76) * mm});
            skLineSegment(sketch, "E393", {"start": v(0.91, 7.76) * mm, "end": v(0.89, 7.93) * mm});
            skLineSegment(sketch, "E394", {"start": v(0.89, 7.93) * mm, "end": v(0.84, 8.1) * mm});
            skLineSegment(sketch, "E395", {"start": v(0.84, 8.1) * mm, "end": v(0.78, 8.28) * mm});
            skLineSegment(sketch, "E396", {"start": v(0.78, 8.28) * mm, "end": v(0.7, 8.48) * mm});
            skLineSegment(sketch, "E397", {"start": v(0.7, 8.48) * mm, "end": v(0.6, 8.68) * mm});
            skLineSegment(sketch, "E398", {"start": v(0.6, 8.68) * mm, "end": v(0.48, 8.9) * mm});
            skLineSegment(sketch, "E399", {"start": v(0.48, 8.9) * mm, "end": v(0.33, 9.14) * mm});
            skLineSegment(sketch, "E400", {"start": v(0.33, 9.14) * mm, "end": v(0.17, 9.39) * mm});
            skLineSegment(sketch, "E401", {"start": v(0.17, 9.39) * mm, "end": v(-0.02, 9.66) * mm});
            skLineSegment(sketch, "E402", {"start": v(-0.02, 9.66) * mm, "end": v(-0.46, 10.27) * mm});
            skLineSegment(sketch, "E403", {"start": v(-0.46, 10.27) * mm, "end": v(-1.01, 10.98) * mm});
            skLineSegment(sketch, "E404", {"start": v(-1.01, 10.98) * mm, "end": v(-0.56, 12.57) * mm});
            skLineSegment(sketch, "E405", {"start": v(0, 67.34) * mm, "end": v(0.27, 67.33) * mm});
            skLineSegment(sketch, "E406", {"start": v(0.27, 67.33) * mm, "end": v(0.54, 67.3) * mm});
            skLineSegment(sketch, "E407", {"start": v(0.54, 67.3) * mm, "end": v(0.8, 67.28) * mm});
            skLineSegment(sketch, "E408", {"start": v(0.8, 67.28) * mm, "end": v(1.06, 67.23) * mm});
            skLineSegment(sketch, "E409", {"start": v(1.06, 67.23) * mm, "end": v(1.32, 67.17) * mm});
            skLineSegment(sketch, "E410", {"start": v(1.32, 67.17) * mm, "end": v(1.57, 67.1) * mm});
            skLineSegment(sketch, "E411", {"start": v(1.57, 67.1) * mm, "end": v(1.81, 67.02) * mm});
            skLineSegment(sketch, "E412", {"start": v(1.81, 67.02) * mm, "end": v(2.05, 66.92) * mm});
            skLineSegment(sketch, "E413", {"start": v(2.05, 66.92) * mm, "end": v(2.28, 66.82) * mm});
            skLineSegment(sketch, "E414", {"start": v(2.28, 66.82) * mm, "end": v(2.51, 66.7) * mm});
            skLineSegment(sketch, "E415", {"start": v(2.51, 66.7) * mm, "end": v(2.73, 66.57) * mm});
            skLineSegment(sketch, "E416", {"start": v(2.73, 66.57) * mm, "end": v(2.94, 66.44) * mm});
            skLineSegment(sketch, "E417", {"start": v(2.94, 66.44) * mm, "end": v(3.15, 66.3) * mm});
            skLineSegment(sketch, "E418", {"start": v(3.15, 66.3) * mm, "end": v(3.35, 66.13) * mm});
            skLineSegment(sketch, "E419", {"start": v(3.35, 66.13) * mm, "end": v(3.54, 65.97) * mm});
            skLineSegment(sketch, "E420", {"start": v(3.54, 65.97) * mm, "end": v(3.72, 65.8) * mm});
            skLineSegment(sketch, "E421", {"start": v(3.72, 65.8) * mm, "end": v(3.9, 65.61) * mm});
            skLineSegment(sketch, "E422", {"start": v(3.9, 65.61) * mm, "end": v(4.06, 65.42) * mm});
            skLineSegment(sketch, "E423", {"start": v(4.06, 65.42) * mm, "end": v(4.22, 65.22) * mm});
            skLineSegment(sketch, "E424", {"start": v(4.22, 65.22) * mm, "end": v(4.37, 65.01) * mm});
            skLineSegment(sketch, "E425", {"start": v(4.37, 65.01) * mm, "end": v(4.5, 64.8) * mm});
            skLineSegment(sketch, "E426", {"start": v(4.5, 64.8) * mm, "end": v(4.63, 64.58) * mm});
            skLineSegment(sketch, "E427", {"start": v(4.63, 64.58) * mm, "end": v(4.75, 64.35) * mm});
            skLineSegment(sketch, "E428", {"start": v(4.75, 64.35) * mm, "end": v(4.85, 64.12) * mm});
            skLineSegment(sketch, "E429", {"start": v(4.85, 64.12) * mm, "end": v(4.95, 63.88) * mm});
            skLineSegment(sketch, "E430", {"start": v(4.95, 63.88) * mm, "end": v(5.03, 63.64) * mm});
            skLineSegment(sketch, "E431", {"start": v(5.03, 63.64) * mm, "end": v(5.1, 63.39) * mm});
            skLineSegment(sketch, "E432", {"start": v(5.1, 63.39) * mm, "end": v(5.16, 63.13) * mm});
            skLineSegment(sketch, "E433", {"start": v(5.16, 63.13) * mm, "end": v(5.2, 62.87) * mm});
            skLineSegment(sketch, "E434", {"start": v(5.2, 62.87) * mm, "end": v(5.24, 62.6) * mm});
            skLineSegment(sketch, "E435", {"start": v(5.24, 62.6) * mm, "end": v(5.26, 62.34) * mm});
            skLineSegment(sketch, "E436", {"start": v(5.26, 62.34) * mm, "end": v(5.27, 62.07) * mm});
            skLineSegment(sketch, "E437", {"start": v(5.27, 62.07) * mm, "end": v(5.26, 61.82) * mm});
            skLineSegment(sketch, "E438", {"start": v(5.26, 61.82) * mm, "end": v(5.24, 61.58) * mm});
            skLineSegment(sketch, "E439", {"start": v(5.24, 61.58) * mm, "end": v(5.22, 61.33) * mm});
            skLineSegment(sketch, "E440", {"start": v(5.22, 61.33) * mm, "end": v(5.18, 61.1) * mm});
            skLineSegment(sketch, "E441", {"start": v(5.18, 61.1) * mm, "end": v(5.13, 60.86) * mm});
            skLineSegment(sketch, "E442", {"start": v(5.13, 60.86) * mm, "end": v(5.07, 60.63) * mm});
            skLineSegment(sketch, "E443", {"start": v(5.07, 60.63) * mm, "end": v(5, 60.4) * mm});
            skLineSegment(sketch, "E444", {"start": v(5, 60.4) * mm, "end": v(4.92, 60.18) * mm});
            skLineSegment(sketch, "E445", {"start": v(4.92, 60.18) * mm, "end": v(4.83, 59.96) * mm});
            skLineSegment(sketch, "E446", {"start": v(4.83, 59.96) * mm, "end": v(4.73, 59.75) * mm});
            skLineSegment(sketch, "E447", {"start": v(4.73, 59.75) * mm, "end": v(4.62, 59.54) * mm});
            skLineSegment(sketch, "E448", {"start": v(4.62, 59.54) * mm, "end": v(4.5, 59.34) * mm});
            skLineSegment(sketch, "E449", {"start": v(4.5, 59.34) * mm, "end": v(4.38, 59.14) * mm});
            skLineSegment(sketch, "E450", {"start": v(4.38, 59.14) * mm, "end": v(4.25, 58.95) * mm});
            skLineSegment(sketch, "E451", {"start": v(4.25, 58.95) * mm, "end": v(4.1, 58.77) * mm});
            skLineSegment(sketch, "E452", {"start": v(4.1, 58.77) * mm, "end": v(3.96, 58.6) * mm});
            skLineSegment(sketch, "E453", {"start": v(3.96, 58.6) * mm, "end": v(4.68, 58.38) * mm});
            skLineSegment(sketch, "E454", {"start": v(4.68, 58.38) * mm, "end": v(5.4, 58.14) * mm});
            skLineSegment(sketch, "E455", {"start": v(5.4, 58.14) * mm, "end": v(6.1, 57.87) * mm});
            skLineSegment(sketch, "E456", {"start": v(6.1, 57.87) * mm, "end": v(6.8, 57.58) * mm});
            skLineSegment(sketch, "E457", {"start": v(6.8, 57.58) * mm, "end": v(7.49, 57.26) * mm});
            skLineSegment(sketch, "E458", {"start": v(7.49, 57.26) * mm, "end": v(8.16, 56.91) * mm});
            skLineSegment(sketch, "E459", {"start": v(8.16, 56.91) * mm, "end": v(8.82, 56.54) * mm});
            skLineSegment(sketch, "E460", {"start": v(8.82, 56.54) * mm, "end": v(9.46, 56.15) * mm});
            skLineSegment(sketch, "E461", {"start": v(9.46, 56.15) * mm, "end": v(9.78, 55.94) * mm});
            skLineSegment(sketch, "E462", {"start": v(9.78, 55.94) * mm, "end": v(10.09, 55.72) * mm});
            skLineSegment(sketch, "E463", {"start": v(10.09, 55.72) * mm, "end": v(10.4, 55.5) * mm});
            skLineSegment(sketch, "E464", {"start": v(10.4, 55.5) * mm, "end": v(10.7, 55.28) * mm});
            skLineSegment(sketch, "E465", {"start": v(10.7, 55.28) * mm, "end": v(11, 55.04) * mm});
            skLineSegment(sketch, "E466", {"start": v(11, 55.04) * mm, "end": v(11.3, 54.8) * mm});
            skLineSegment(sketch, "E467", {"start": v(11.3, 54.8) * mm, "end": v(11.59, 54.56) * mm});
            skLineSegment(sketch, "E468", {"start": v(11.59, 54.56) * mm, "end": v(11.87, 54.3) * mm});
            skLineSegment(sketch, "E469", {"start": v(11.87, 54.3) * mm, "end": v(12.15, 54.04) * mm});
            skLineSegment(sketch, "E470", {"start": v(12.15, 54.04) * mm, "end": v(12.43, 53.78) * mm});
            skLineSegment(sketch, "E471", {"start": v(12.43, 53.78) * mm, "end": v(12.7, 53.5) * mm});
            skLineSegment(sketch, "E472", {"start": v(12.7, 53.5) * mm, "end": v(12.97, 53.22) * mm});
            skLineSegment(sketch, "E473", {"start": v(12.97, 53.22) * mm, "end": v(13.23, 52.94) * mm});
            skLineSegment(sketch, "E474", {"start": v(13.23, 52.94) * mm, "end": v(13.48, 52.64) * mm});
            skLineSegment(sketch, "E475", {"start": v(13.48, 52.64) * mm, "end": v(13.74, 52.34) * mm});
            skLineSegment(sketch, "E476", {"start": v(13.74, 52.34) * mm, "end": v(13.98, 52.04) * mm});
            skLineSegment(sketch, "E477", {"start": v(13.98, 52.04) * mm, "end": v(14.35, 51.56) * mm});
            skLineSegment(sketch, "E478", {"start": v(14.35, 51.56) * mm, "end": v(14.7, 51.07) * mm});
            skLineSegment(sketch, "E479", {"start": v(14.7, 51.07) * mm, "end": v(15.03, 50.57) * mm});
            skLineSegment(sketch, "E480", {"start": v(15.03, 50.57) * mm, "end": v(15.35, 50.07) * mm});
            skLineSegment(sketch, "E481", {"start": v(15.35, 50.07) * mm, "end": v(15.65, 49.56) * mm});
            skLineSegment(sketch, "E482", {"start": v(15.65, 49.56) * mm, "end": v(15.93, 49.04) * mm});
            skLineSegment(sketch, "E483", {"start": v(15.93, 49.04) * mm, "end": v(16.2, 48.52) * mm});
            skLineSegment(sketch, "E484", {"start": v(16.2, 48.52) * mm, "end": v(16.46, 48) * mm});
            skLineSegment(sketch, "E485", {"start": v(16.46, 48) * mm, "end": v(16.7, 47.46) * mm});
            skLineSegment(sketch, "E486", {"start": v(16.7, 47.46) * mm, "end": v(16.92, 46.92) * mm});
            skLineSegment(sketch, "E487", {"start": v(16.92, 46.92) * mm, "end": v(17.13, 46.37) * mm});
            skLineSegment(sketch, "E488", {"start": v(17.13, 46.37) * mm, "end": v(17.32, 45.82) * mm});
            skLineSegment(sketch, "E489", {"start": v(17.32, 45.82) * mm, "end": v(17.5, 45.26) * mm});
            skLineSegment(sketch, "E490", {"start": v(17.5, 45.26) * mm, "end": v(17.67, 44.7) * mm});
            skLineSegment(sketch, "E491", {"start": v(17.67, 44.7) * mm, "end": v(17.83, 44.13) * mm});
            skLineSegment(sketch, "E492", {"start": v(17.83, 44.13) * mm, "end": v(17.97, 43.56) * mm});
            skLineSegment(sketch, "E493", {"start": v(17.97, 43.56) * mm, "end": v(18.86, 43.2) * mm});
            skLineSegment(sketch, "E494", {"start": v(18.86, 43.2) * mm, "end": v(19.75, 42.84) * mm});
            skLineSegment(sketch, "E495", {"start": v(19.75, 42.84) * mm, "end": v(20.63, 42.46) * mm});
            skLineSegment(sketch, "E496", {"start": v(20.63, 42.46) * mm, "end": v(21.5, 42.07) * mm});
            skLineSegment(sketch, "E497", {"start": v(21.5, 42.07) * mm, "end": v(22.36, 41.65) * mm});
            skLineSegment(sketch, "E498", {"start": v(22.36, 41.65) * mm, "end": v(23.21, 41.22) * mm});
            skLineSegment(sketch, "E499", {"start": v(23.21, 41.22) * mm, "end": v(24.05, 40.78) * mm});
            skLineSegment(sketch, "E500", {"start": v(24.05, 40.78) * mm, "end": v(24.89, 40.32) * mm});
            skLineSegment(sketch, "E501", {"start": v(24.89, 40.32) * mm, "end": v(25.71, 39.85) * mm});
            skLineSegment(sketch, "E502", {"start": v(25.71, 39.85) * mm, "end": v(26.52, 39.36) * mm});
            skLineSegment(sketch, "E503", {"start": v(26.52, 39.36) * mm, "end": v(27.33, 38.86) * mm});
            skLineSegment(sketch, "E504", {"start": v(27.33, 38.86) * mm, "end": v(28.12, 38.34) * mm});
            skLineSegment(sketch, "E505", {"start": v(28.12, 38.34) * mm, "end": v(28.9, 37.8) * mm});
            skLineSegment(sketch, "E506", {"start": v(28.9, 37.8) * mm, "end": v(29.68, 37.26) * mm});
            skLineSegment(sketch, "E507", {"start": v(29.68, 37.26) * mm, "end": v(30.44, 36.7) * mm});
            skLineSegment(sketch, "E508", {"start": v(30.44, 36.7) * mm, "end": v(31.2, 36.12) * mm});
            skLineSegment(sketch, "E509", {"start": v(31.2, 36.12) * mm, "end": v(31.93, 35.54) * mm});
            skLineSegment(sketch, "E510", {"start": v(31.93, 35.54) * mm, "end": v(32.66, 34.94) * mm});
            skLineSegment(sketch, "E511", {"start": v(32.66, 34.94) * mm, "end": v(33.38, 34.32) * mm});
            skLineSegment(sketch, "E512", {"start": v(33.38, 34.32) * mm, "end": v(34.08, 33.7) * mm});
            skLineSegment(sketch, "E513", {"start": v(34.08, 33.7) * mm, "end": v(34.78, 33.05) * mm});
            skLineSegment(sketch, "E514", {"start": v(34.78, 33.05) * mm, "end": v(35.46, 32.4) * mm});
            skLineSegment(sketch, "E515", {"start": v(35.46, 32.4) * mm, "end": v(36.13, 31.74) * mm});
            skLineSegment(sketch, "E516", {"start": v(36.13, 31.74) * mm, "end": v(36.79, 31.06) * mm});
            skLineSegment(sketch, "E517", {"start": v(36.79, 31.06) * mm, "end": v(37.43, 30.37) * mm});
            skLineSegment(sketch, "E518", {"start": v(37.43, 30.37) * mm, "end": v(38.06, 29.67) * mm});
            skLineSegment(sketch, "E519", {"start": v(38.06, 29.67) * mm, "end": v(38.68, 28.96) * mm});
            skLineSegment(sketch, "E520", {"start": v(38.68, 28.96) * mm, "end": v(39.29, 28.23) * mm});
            skLineSegment(sketch, "E521", {"start": v(39.29, 28.23) * mm, "end": v(39.88, 27.5) * mm});
            skLineSegment(sketch, "E522", {"start": v(39.88, 27.5) * mm, "end": v(40.46, 26.75) * mm});
            skLineSegment(sketch, "E523", {"start": v(40.46, 26.75) * mm, "end": v(41.03, 25.99) * mm});
            skLineSegment(sketch, "E524", {"start": v(41.03, 25.99) * mm, "end": v(41.58, 25.22) * mm});
            skLineSegment(sketch, "E525", {"start": v(41.58, 25.22) * mm, "end": v(42.12, 24.44) * mm});
            skLineSegment(sketch, "E526", {"start": v(42.12, 24.44) * mm, "end": v(42.64, 23.65) * mm});
            skLineSegment(sketch, "E527", {"start": v(42.64, 23.65) * mm, "end": v(43.15, 22.85) * mm});
            skLineSegment(sketch, "E528", {"start": v(43.15, 22.85) * mm, "end": v(43.64, 22.04) * mm});
            skLineSegment(sketch, "E529", {"start": v(43.64, 22.04) * mm, "end": v(44.12, 21.22) * mm});
            skLineSegment(sketch, "E530", {"start": v(44.12, 21.22) * mm, "end": v(44.59, 20.4) * mm});
            skLineSegment(sketch, "E531", {"start": v(44.59, 20.4) * mm, "end": v(45.04, 19.55) * mm});
            skLineSegment(sketch, "E532", {"start": v(45.04, 19.55) * mm, "end": v(45.47, 18.7) * mm});
            skLineSegment(sketch, "E533", {"start": v(45.47, 18.7) * mm, "end": v(45.89, 17.85) * mm});
            skLineSegment(sketch, "E534", {"start": v(45.89, 17.85) * mm, "end": v(46.3, 16.98) * mm});
            skLineSegment(sketch, "E535", {"start": v(46.3, 16.98) * mm, "end": v(46.68, 16.1) * mm});
            skLineSegment(sketch, "E536", {"start": v(46.68, 16.1) * mm, "end": v(47.05, 15.22) * mm});
            skLineSegment(sketch, "E537", {"start": v(47.05, 15.22) * mm, "end": v(47.4, 14.33) * mm});
            skLineSegment(sketch, "E538", {"start": v(47.4, 14.33) * mm, "end": v(47.74, 13.43) * mm});
            skLineSegment(sketch, "E539", {"start": v(47.74, 13.43) * mm, "end": v(48.06, 12.52) * mm});
            skLineSegment(sketch, "E540", {"start": v(48.06, 12.52) * mm, "end": v(48.37, 11.6) * mm});
            skLineSegment(sketch, "E541", {"start": v(48.37, 11.6) * mm, "end": v(48.66, 10.68) * mm});
            skLineSegment(sketch, "E542", {"start": v(48.66, 10.68) * mm, "end": v(48.93, 9.75) * mm});
            skLineSegment(sketch, "E543", {"start": v(48.93, 9.75) * mm, "end": v(49.18, 8.8) * mm});
            skLineSegment(sketch, "E544", {"start": v(49.18, 8.8) * mm, "end": v(49.41, 7.86) * mm});
            skLineSegment(sketch, "E545", {"start": v(49.41, 7.86) * mm, "end": v(49.63, 6.91) * mm});
            skLineSegment(sketch, "E546", {"start": v(49.63, 6.91) * mm, "end": v(49.83, 5.95) * mm});
            skLineSegment(sketch, "E547", {"start": v(49.83, 5.95) * mm, "end": v(50.01, 4.99) * mm});
            skLineSegment(sketch, "E548", {"start": v(50.01, 4.99) * mm, "end": v(50.18, 4.01) * mm});
            skLineSegment(sketch, "E549", {"start": v(50.18, 4.01) * mm, "end": v(50.32, 3.03) * mm});
            skLineSegment(sketch, "E550", {"start": v(50.32, 3.03) * mm, "end": v(50.45, 2.05) * mm});
            skLineSegment(sketch, "E551", {"start": v(50.45, 2.05) * mm, "end": v(50.55, 1.06) * mm});
            skLineSegment(sketch, "E552", {"start": v(50.55, 1.06) * mm, "end": v(50.64, 0.06) * mm});
            skLineSegment(sketch, "E553", {"start": v(50.64, 0.06) * mm, "end": v(50.71, -0.94) * mm});
            skLineSegment(sketch, "E554", {"start": v(50.71, -0.94) * mm, "end": v(50.76, -1.94) * mm});
            skLineSegment(sketch, "E555", {"start": v(50.76, -1.94) * mm, "end": v(50.8, -2.95) * mm});
            skLineSegment(sketch, "E556", {"start": v(50.8, -2.95) * mm, "end": v(50.8, -3.97) * mm});
            skLineSegment(sketch, "E557", {"start": v(50.8, -3.97) * mm, "end": v(50.8, -4.63) * mm});
            skLineSegment(sketch, "E558", {"start": v(50.8, -4.63) * mm, "end": v(50.78, -5.28) * mm});
            skLineSegment(sketch, "E559", {"start": v(50.78, -5.28) * mm, "end": v(50.76, -5.93) * mm});
            skLineSegment(sketch, "E560", {"start": v(50.76, -5.93) * mm, "end": v(50.73, -6.58) * mm});
            skLineSegment(sketch, "E561", {"start": v(50.73, -6.58) * mm, "end": v(50.7, -7.23) * mm});
            skLineSegment(sketch, "E562", {"start": v(50.7, -7.23) * mm, "end": v(50.65, -7.88) * mm});
            skLineSegment(sketch, "E563", {"start": v(50.65, -7.88) * mm, "end": v(50.6, -8.52) * mm});
            skLineSegment(sketch, "E564", {"start": v(50.6, -8.52) * mm, "end": v(50.54, -9.16) * mm});
            skLineSegment(sketch, "E565", {"start": v(50.54, -9.16) * mm, "end": v(50.47, -9.8) * mm});
            skLineSegment(sketch, "E566", {"start": v(50.47, -9.8) * mm, "end": v(50.4, -10.44) * mm});
            skLineSegment(sketch, "E567", {"start": v(50.4, -10.44) * mm, "end": v(50.3, -11.07) * mm});
            skLineSegment(sketch, "E568", {"start": v(50.3, -11.07) * mm, "end": v(50.21, -11.7) * mm});
            skLineSegment(sketch, "E569", {"start": v(50.21, -11.7) * mm, "end": v(50.11, -12.34) * mm});
            skLineSegment(sketch, "E570", {"start": v(50.11, -12.34) * mm, "end": v(50, -12.96) * mm});
            skLineSegment(sketch, "E571", {"start": v(50, -12.96) * mm, "end": v(49.9, -13.59) * mm});
            skLineSegment(sketch, "E572", {"start": v(49.9, -13.59) * mm, "end": v(49.77, -14.2) * mm});
            skLineSegment(sketch, "E573", {"start": v(49.77, -14.2) * mm, "end": v(49.64, -14.83) * mm});
            skLineSegment(sketch, "E574", {"start": v(49.64, -14.83) * mm, "end": v(49.5, -15.44) * mm});
            skLineSegment(sketch, "E575", {"start": v(49.5, -15.44) * mm, "end": v(49.35, -16.06) * mm});
            skLineSegment(sketch, "E576", {"start": v(49.35, -16.06) * mm, "end": v(49.2, -16.67) * mm});
            skLineSegment(sketch, "E577", {"start": v(49.2, -16.67) * mm, "end": v(49.04, -17.27) * mm});
            skLineSegment(sketch, "E578", {"start": v(49.04, -17.27) * mm, "end": v(48.87, -17.88) * mm});
            skLineSegment(sketch, "E579", {"start": v(48.87, -17.88) * mm, "end": v(48.7, -18.48) * mm});
            skLineSegment(sketch, "E580", {"start": v(48.7, -18.48) * mm, "end": v(48.52, -19.08) * mm});
            skLineSegment(sketch, "E581", {"start": v(48.52, -19.08) * mm, "end": v(48.33, -19.67) * mm});
            skLineSegment(sketch, "E582", {"start": v(48.33, -19.67) * mm, "end": v(48.13, -20.26) * mm});
            skLineSegment(sketch, "E583", {"start": v(48.13, -20.26) * mm, "end": v(47.93, -20.85) * mm});
            skLineSegment(sketch, "E584", {"start": v(47.93, -20.85) * mm, "end": v(47.72, -21.44) * mm});
            skLineSegment(sketch, "E585", {"start": v(47.72, -21.44) * mm, "end": v(47.5, -22.02) * mm});
            skLineSegment(sketch, "E586", {"start": v(47.5, -22.02) * mm, "end": v(47.28, -22.6) * mm});
            skLineSegment(sketch, "E587", {"start": v(47.28, -22.6) * mm, "end": v(46.8, -23.74) * mm});
            skLineSegment(sketch, "E588", {"start": v(46.8, -23.74) * mm, "end": v(46.31, -24.88) * mm});
            skLineSegment(sketch, "E589", {"start": v(46.31, -24.88) * mm, "end": v(45.8, -26) * mm});
            skLineSegment(sketch, "E590", {"start": v(45.8, -26) * mm, "end": v(45.24, -27.1) * mm});
            skLineSegment(sketch, "E591", {"start": v(45.24, -27.1) * mm, "end": v(44.67, -28.18) * mm});
            skLineSegment(sketch, "E592", {"start": v(44.67, -28.18) * mm, "end": v(44.07, -29.26) * mm});
            skLineSegment(sketch, "E593", {"start": v(44.07, -29.26) * mm, "end": v(43.45, -30.31) * mm});
            skLineSegment(sketch, "E594", {"start": v(43.45, -30.31) * mm, "end": v(42.8, -31.35) * mm});
            skLineSegment(sketch, "E595", {"start": v(42.8, -31.35) * mm, "end": v(42.12, -32.37) * mm});
            skLineSegment(sketch, "E596", {"start": v(42.12, -32.37) * mm, "end": v(41.43, -33.38) * mm});
            skLineSegment(sketch, "E597", {"start": v(41.43, -33.38) * mm, "end": v(40.7, -34.36) * mm});
            skLineSegment(sketch, "E598", {"start": v(40.7, -34.36) * mm, "end": v(39.97, -35.33) * mm});
            skLineSegment(sketch, "E599", {"start": v(39.97, -35.33) * mm, "end": v(39.2, -36.28) * mm});
            skLineSegment(sketch, "E600", {"start": v(39.2, -36.28) * mm, "end": v(38.41, -37.22) * mm});
            skLineSegment(sketch, "E601", {"start": v(38.41, -37.22) * mm, "end": v(37.6, -38.13) * mm});
            skLineSegment(sketch, "E602", {"start": v(37.6, -38.13) * mm, "end": v(36.77, -39.02) * mm});
            skLineSegment(sketch, "E603", {"start": v(36.77, -39.02) * mm, "end": v(35.92, -39.9) * mm});
            skLineSegment(sketch, "E604", {"start": v(35.92, -39.9) * mm, "end": v(35.05, -40.74) * mm});
            skLineSegment(sketch, "E605", {"start": v(35.05, -40.74) * mm, "end": v(34.16, -41.57) * mm});
            skLineSegment(sketch, "E606", {"start": v(34.16, -41.57) * mm, "end": v(33.24, -42.38) * mm});
            skLineSegment(sketch, "E607", {"start": v(33.24, -42.38) * mm, "end": v(32.31, -43.17) * mm});
            skLineSegment(sketch, "E608", {"start": v(32.31, -43.17) * mm, "end": v(31.36, -43.94) * mm});
            skLineSegment(sketch, "E609", {"start": v(31.36, -43.94) * mm, "end": v(30.4, -44.68) * mm});
            skLineSegment(sketch, "E610", {"start": v(30.4, -44.68) * mm, "end": v(29.4, -45.4) * mm});
            skLineSegment(sketch, "E611", {"start": v(29.4, -45.4) * mm, "end": v(28.4, -46.1) * mm});
            skLineSegment(sketch, "E612", {"start": v(28.4, -46.1) * mm, "end": v(27.38, -46.77) * mm});
            skLineSegment(sketch, "E613", {"start": v(27.38, -46.77) * mm, "end": v(26.34, -47.42) * mm});
            skLineSegment(sketch, "E614", {"start": v(26.34, -47.42) * mm, "end": v(25.29, -48.04) * mm});
            skLineSegment(sketch, "E615", {"start": v(25.29, -48.04) * mm, "end": v(24.21, -48.64) * mm});
            skLineSegment(sketch, "E616", {"start": v(24.21, -48.64) * mm, "end": v(23.13, -49.21) * mm});
            skLineSegment(sketch, "E617", {"start": v(23.13, -49.21) * mm, "end": v(22.02, -49.76) * mm});
            skLineSegment(sketch, "E618", {"start": v(22.02, -49.76) * mm, "end": v(20.9, -50.28) * mm});
            skLineSegment(sketch, "E619", {"start": v(20.9, -50.28) * mm, "end": v(19.77, -50.78) * mm});
            skLineSegment(sketch, "E620", {"start": v(19.77, -50.78) * mm, "end": v(18.63, -51.25) * mm});
            skLineSegment(sketch, "E621", {"start": v(18.63, -51.25) * mm, "end": v(18.05, -51.47) * mm});
            skLineSegment(sketch, "E622", {"start": v(18.05, -51.47) * mm, "end": v(17.47, -51.69) * mm});
            skLineSegment(sketch, "E623", {"start": v(17.47, -51.69) * mm, "end": v(16.88, -51.9) * mm});
            skLineSegment(sketch, "E624", {"start": v(16.88, -51.9) * mm, "end": v(16.3, -52.1) * mm});
            skLineSegment(sketch, "E625", {"start": v(16.3, -52.1) * mm, "end": v(15.7, -52.3) * mm});
            skLineSegment(sketch, "E626", {"start": v(15.7, -52.3) * mm, "end": v(15.1, -52.49) * mm});
            skLineSegment(sketch, "E627", {"start": v(15.1, -52.49) * mm, "end": v(14.5, -52.67) * mm});
            skLineSegment(sketch, "E628", {"start": v(14.5, -52.67) * mm, "end": v(13.9, -52.84) * mm});
            skLineSegment(sketch, "E629", {"start": v(13.9, -52.84) * mm, "end": v(13.3, -53.01) * mm});
            skLineSegment(sketch, "E630", {"start": v(13.3, -53.01) * mm, "end": v(12.7, -53.17) * mm});
            skLineSegment(sketch, "E631", {"start": v(12.7, -53.17) * mm, "end": v(12.09, -53.32) * mm});
            skLineSegment(sketch, "E632", {"start": v(12.09, -53.32) * mm, "end": v(11.47, -53.47) * mm});
            skLineSegment(sketch, "E633", {"start": v(11.47, -53.47) * mm, "end": v(10.86, -53.6) * mm});
            skLineSegment(sketch, "E634", {"start": v(10.86, -53.6) * mm, "end": v(10.24, -53.74) * mm});
            skLineSegment(sketch, "E635", {"start": v(10.24, -53.74) * mm, "end": v(9.62, -53.86) * mm});
            skLineSegment(sketch, "E636", {"start": v(9.62, -53.86) * mm, "end": v(9, -53.98) * mm});
            skLineSegment(sketch, "E637", {"start": v(9, -53.98) * mm, "end": v(8.37, -54.08) * mm});
            skLineSegment(sketch, "E638", {"start": v(8.37, -54.08) * mm, "end": v(7.74, -54.18) * mm});
            skLineSegment(sketch, "E639", {"start": v(7.74, -54.18) * mm, "end": v(7.1, -54.28) * mm});
            skLineSegment(sketch, "E640", {"start": v(7.1, -54.28) * mm, "end": v(6.47, -54.36) * mm});
            skLineSegment(sketch, "E641", {"start": v(6.47, -54.36) * mm, "end": v(5.83, -54.44) * mm});
            skLineSegment(sketch, "E642", {"start": v(5.83, -54.44) * mm, "end": v(5.2, -54.5) * mm});
            skLineSegment(sketch, "E643", {"start": v(5.2, -54.5) * mm, "end": v(4.55, -54.57) * mm});
            skLineSegment(sketch, "E644", {"start": v(4.55, -54.57) * mm, "end": v(3.9, -54.62) * mm});
            skLineSegment(sketch, "E645", {"start": v(3.9, -54.62) * mm, "end": v(3.26, -54.67) * mm});
            skLineSegment(sketch, "E646", {"start": v(3.26, -54.67) * mm, "end": v(2.61, -54.7) * mm});
            skLineSegment(sketch, "E647", {"start": v(2.61, -54.7) * mm, "end": v(1.96, -54.73) * mm});
            skLineSegment(sketch, "E648", {"start": v(1.96, -54.73) * mm, "end": v(1.31, -54.75) * mm});
            skLineSegment(sketch, "E649", {"start": v(1.31, -54.75) * mm, "end": v(0.66, -54.77) * mm});
            skLineSegment(sketch, "E650", {"start": v(0.66, -54.77) * mm, "end": v(0, -54.77) * mm});
            skLineSegment(sketch, "E651", {"start": v(0, -54.77) * mm, "end": v(-0.62, -54.77) * mm});
            skLineSegment(sketch, "E652", {"start": v(-0.62, -54.77) * mm, "end": v(-1.25, -54.75) * mm});
            skLineSegment(sketch, "E653", {"start": v(-1.25, -54.75) * mm, "end": v(-2.48, -54.7) * mm});
            skLineSegment(sketch, "E654", {"start": v(-2.48, -54.7) * mm, "end": v(-3.72, -54.63) * mm});
            skLineSegment(sketch, "E655", {"start": v(-3.72, -54.63) * mm, "end": v(-4.94, -54.53) * mm});
            skLineSegment(sketch, "E656", {"start": v(-4.94, -54.53) * mm, "end": v(-5.36, -55.92) * mm});
            skLineSegment(sketch, "E657", {"start": v(-5.36, -55.92) * mm, "end": v(-5.76, -57.22) * mm});
            skLineSegment(sketch, "E658", {"start": v(-5.76, -57.22) * mm, "end": v(-6.14, -58.4) * mm});
            skLineSegment(sketch, "E659", {"start": v(-6.14, -58.4) * mm, "end": v(-6.5, -59.48) * mm});
            skLineSegment(sketch, "E660", {"start": v(-6.5, -59.48) * mm, "end": v(-6.81, -60.41) * mm});
            skLineSegment(sketch, "E661", {"start": v(-6.81, -60.41) * mm, "end": v(-7.1, -61.2) * mm});
            skLineSegment(sketch, "E662", {"start": v(-7.1, -61.2) * mm, "end": v(-7.35, -61.82) * mm});
            skLineSegment(sketch, "E663", {"start": v(-7.35, -61.82) * mm, "end": v(-7.46, -62.07) * mm});
            skLineSegment(sketch, "E664", {"start": v(-7.46, -62.07) * mm, "end": v(-7.56, -62.27) * mm});
            skLineSegment(sketch, "E665", {"start": v(-7.56, -62.27) * mm, "end": v(-7.78, -62.68) * mm});
            skLineSegment(sketch, "E666", {"start": v(-7.78, -62.68) * mm, "end": v(-8.01, -63.07) * mm});
            skLineSegment(sketch, "E667", {"start": v(-8.01, -63.07) * mm, "end": v(-8.25, -63.44) * mm});
            skLineSegment(sketch, "E668", {"start": v(-8.25, -63.44) * mm, "end": v(-8.5, -63.8) * mm});
            skLineSegment(sketch, "E669", {"start": v(-8.5, -63.8) * mm, "end": v(-8.74, -64.13) * mm});
            skLineSegment(sketch, "E670", {"start": v(-8.74, -64.13) * mm, "end": v(-9, -64.44) * mm});
            skLineSegment(sketch, "E671", {"start": v(-9, -64.44) * mm, "end": v(-9.25, -64.74) * mm});
            skLineSegment(sketch, "E672", {"start": v(-9.25, -64.74) * mm, "end": v(-9.52, -65.02) * mm});
            skLineSegment(sketch, "E673", {"start": v(-9.52, -65.02) * mm, "end": v(-9.79, -65.29) * mm});
            skLineSegment(sketch, "E674", {"start": v(-9.79, -65.29) * mm, "end": v(-10.06, -65.53) * mm});
            skLineSegment(sketch, "E675", {"start": v(-10.06, -65.53) * mm, "end": v(-10.33, -65.76) * mm});
            skLineSegment(sketch, "E676", {"start": v(-10.33, -65.76) * mm, "end": v(-10.61, -65.98) * mm});
            skLineSegment(sketch, "E677", {"start": v(-10.61, -65.98) * mm, "end": v(-10.9, -66.17) * mm});
            skLineSegment(sketch, "E678", {"start": v(-10.9, -66.17) * mm, "end": v(-11.18, -66.35) * mm});
            skLineSegment(sketch, "E679", {"start": v(-11.18, -66.35) * mm, "end": v(-11.47, -66.52) * mm});
            skLineSegment(sketch, "E680", {"start": v(-11.47, -66.52) * mm, "end": v(-11.75, -66.67) * mm});
            skLineSegment(sketch, "E681", {"start": v(-11.75, -66.67) * mm, "end": v(-12.04, -66.8) * mm});
            skLineSegment(sketch, "E682", {"start": v(-12.04, -66.8) * mm, "end": v(-12.34, -66.92) * mm});
            skLineSegment(sketch, "E683", {"start": v(-12.34, -66.92) * mm, "end": v(-12.63, -67.02) * mm});
            skLineSegment(sketch, "E684", {"start": v(-12.63, -67.02) * mm, "end": v(-12.92, -67.1) * mm});
            skLineSegment(sketch, "E685", {"start": v(-12.92, -67.1) * mm, "end": v(-13.22, -67.18) * mm});
            skLineSegment(sketch, "E686", {"start": v(-13.22, -67.18) * mm, "end": v(-13.51, -67.24) * mm});
            skLineSegment(sketch, "E687", {"start": v(-13.51, -67.24) * mm, "end": v(-13.8, -67.29) * mm});
            skLineSegment(sketch, "E688", {"start": v(-13.8, -67.29) * mm, "end": v(-14.1, -67.32) * mm});
            skLineSegment(sketch, "E689", {"start": v(-14.1, -67.32) * mm, "end": v(-14.4, -67.33) * mm});
            skLineSegment(sketch, "E690", {"start": v(-14.4, -67.33) * mm, "end": v(-14.68, -67.34) * mm});
            skLineSegment(sketch, "E691", {"start": v(-14.68, -67.34) * mm, "end": v(-14.97, -67.33) * mm});
            skLineSegment(sketch, "E692", {"start": v(-14.97, -67.33) * mm, "end": v(-15.26, -67.3) * mm});
            skLineSegment(sketch, "E693", {"start": v(-15.26, -67.3) * mm, "end": v(-15.54, -67.27) * mm});
            skLineSegment(sketch, "E694", {"start": v(-15.54, -67.27) * mm, "end": v(-15.83, -67.22) * mm});
            skLineSegment(sketch, "E695", {"start": v(-15.83, -67.22) * mm, "end": v(-16.1, -67.15) * mm});
            skLineSegment(sketch, "E696", {"start": v(-16.1, -67.15) * mm, "end": v(-16.38, -67.08) * mm});
            skLineSegment(sketch, "E697", {"start": v(-16.38, -67.08) * mm, "end": v(-16.66, -67) * mm});
            skLineSegment(sketch, "E698", {"start": v(-16.66, -67) * mm, "end": v(-16.92, -66.9) * mm});
            skLineSegment(sketch, "E699", {"start": v(-16.92, -66.9) * mm, "end": v(-17.19, -66.79) * mm});
            skLineSegment(sketch, "E700", {"start": v(-17.19, -66.79) * mm, "end": v(-17.45, -66.66) * mm});
            skLineSegment(sketch, "E701", {"start": v(-17.45, -66.66) * mm, "end": v(-17.7, -66.53) * mm});
            skLineSegment(sketch, "E702", {"start": v(-17.7, -66.53) * mm, "end": v(-17.95, -66.39) * mm});
            skLineSegment(sketch, "E703", {"start": v(-17.95, -66.39) * mm, "end": v(-18.2, -66.23) * mm});
            skLineSegment(sketch, "E704", {"start": v(-18.2, -66.23) * mm, "end": v(-18.44, -66.07) * mm});
            skLineSegment(sketch, "E705", {"start": v(-18.44, -66.07) * mm, "end": v(-18.67, -65.9) * mm});
            skLineSegment(sketch, "E706", {"start": v(-18.67, -65.9) * mm, "end": v(-18.9, -65.7) * mm});
            skLineSegment(sketch, "E707", {"start": v(-18.9, -65.7) * mm, "end": v(-19.11, -65.5) * mm});
            skLineSegment(sketch, "E708", {"start": v(-19.11, -65.5) * mm, "end": v(-19.32, -65.3) * mm});
            skLineSegment(sketch, "E709", {"start": v(-19.32, -65.3) * mm, "end": v(-19.53, -65.09) * mm});
            skLineSegment(sketch, "E710", {"start": v(-19.53, -65.09) * mm, "end": v(-19.72, -64.86) * mm});
            skLineSegment(sketch, "E711", {"start": v(-19.72, -64.86) * mm, "end": v(-19.9, -64.63) * mm});
            skLineSegment(sketch, "E712", {"start": v(-19.9, -64.63) * mm, "end": v(-20.09, -64.38) * mm});
            skLineSegment(sketch, "E713", {"start": v(-20.09, -64.38) * mm, "end": v(-20.26, -64.13) * mm});
            skLineSegment(sketch, "E714", {"start": v(-20.26, -64.13) * mm, "end": v(-20.42, -63.87) * mm});
            skLineSegment(sketch, "E715", {"start": v(-20.42, -63.87) * mm, "end": v(-20.57, -63.6) * mm});
            skLineSegment(sketch, "E716", {"start": v(-20.57, -63.6) * mm, "end": v(-20.71, -63.33) * mm});
            skLineSegment(sketch, "E717", {"start": v(-20.71, -63.33) * mm, "end": v(-20.84, -63.04) * mm});
            skLineSegment(sketch, "E718", {"start": v(-20.84, -63.04) * mm, "end": v(-20.96, -62.75) * mm});
            skLineSegment(sketch, "E719", {"start": v(-20.96, -62.75) * mm, "end": v(-21.07, -62.45) * mm});
            skLineSegment(sketch, "E720", {"start": v(-21.07, -62.45) * mm, "end": v(-21.17, -62.14) * mm});
            skLineSegment(sketch, "E721", {"start": v(-21.17, -62.14) * mm, "end": v(-21.26, -61.83) * mm});
            skLineSegment(sketch, "E722", {"start": v(-21.26, -61.83) * mm, "end": v(-21.33, -61.5) * mm});
            skLineSegment(sketch, "E723", {"start": v(-21.33, -61.5) * mm, "end": v(-21.4, -61.18) * mm});
            skLineSegment(sketch, "E724", {"start": v(-21.4, -61.18) * mm, "end": v(-21.45, -60.84) * mm});
            skLineSegment(sketch, "E725", {"start": v(-21.45, -60.84) * mm, "end": v(-21.48, -60.5) * mm});
            skLineSegment(sketch, "E726", {"start": v(-21.48, -60.5) * mm, "end": v(-21.5, -60.16) * mm});
            skLineSegment(sketch, "E727", {"start": v(-21.5, -60.16) * mm, "end": v(-21.52, -59.8) * mm});
            skLineSegment(sketch, "E728", {"start": v(-21.52, -59.8) * mm, "end": v(-21.51, -59.45) * mm});
            skLineSegment(sketch, "E729", {"start": v(-21.51, -59.45) * mm, "end": v(-21.5, -59.23) * mm});
            skLineSegment(sketch, "E730", {"start": v(-21.5, -59.23) * mm, "end": v(-21.47, -58.96) * mm});
            skLineSegment(sketch, "E731", {"start": v(-21.47, -58.96) * mm, "end": v(-21.36, -58.26) * mm});
            skLineSegment(sketch, "E732", {"start": v(-21.36, -58.26) * mm, "end": v(-21.2, -57.39) * mm});
            skLineSegment(sketch, "E733", {"start": v(-21.2, -57.39) * mm, "end": v(-20.97, -56.34) * mm});
            skLineSegment(sketch, "E734", {"start": v(-20.97, -56.34) * mm, "end": v(-20.7, -55.14) * mm});
            skLineSegment(sketch, "E735", {"start": v(-20.7, -55.14) * mm, "end": v(-20.38, -53.81) * mm});
            skLineSegment(sketch, "E736", {"start": v(-20.38, -53.81) * mm, "end": v(-20.03, -52.37) * mm});
            skLineSegment(sketch, "E737", {"start": v(-20.03, -52.37) * mm, "end": v(-19.64, -50.83) * mm});
            skLineSegment(sketch, "E738", {"start": v(-19.64, -50.83) * mm, "end": v(-20.5, -50.46) * mm});
            skLineSegment(sketch, "E739", {"start": v(-20.5, -50.46) * mm, "end": v(-21.34, -50.08) * mm});
            skLineSegment(sketch, "E740", {"start": v(-21.34, -50.08) * mm, "end": v(-22.18, -49.68) * mm});
            skLineSegment(sketch, "E741", {"start": v(-22.18, -49.68) * mm, "end": v(-23, -49.27) * mm});
            skLineSegment(sketch, "E742", {"start": v(-23, -49.27) * mm, "end": v(-23.83, -48.84) * mm});
            skLineSegment(sketch, "E743", {"start": v(-23.83, -48.84) * mm, "end": v(-24.64, -48.4) * mm});
            skLineSegment(sketch, "E744", {"start": v(-24.64, -48.4) * mm, "end": v(-25.44, -47.94) * mm});
            skLineSegment(sketch, "E745", {"start": v(-25.44, -47.94) * mm, "end": v(-26.24, -47.47) * mm});
            skLineSegment(sketch, "E746", {"start": v(-26.24, -47.47) * mm, "end": v(-27.02, -46.99) * mm});
            skLineSegment(sketch, "E747", {"start": v(-27.02, -46.99) * mm, "end": v(-27.8, -46.5) * mm});
            skLineSegment(sketch, "E748", {"start": v(-27.8, -46.5) * mm, "end": v(-28.56, -45.98) * mm});
            skLineSegment(sketch, "E749", {"start": v(-28.56, -45.98) * mm, "end": v(-29.31, -45.46) * mm});
            skLineSegment(sketch, "E750", {"start": v(-29.31, -45.46) * mm, "end": v(-30.06, -44.92) * mm});
            skLineSegment(sketch, "E751", {"start": v(-30.06, -44.92) * mm, "end": v(-30.8, -44.37) * mm});
            skLineSegment(sketch, "E752", {"start": v(-30.8, -44.37) * mm, "end": v(-31.52, -43.8) * mm});
            skLineSegment(sketch, "E753", {"start": v(-31.52, -43.8) * mm, "end": v(-32.23, -43.23) * mm});
            skLineSegment(sketch, "E754", {"start": v(-32.23, -43.23) * mm, "end": v(-32.94, -42.64) * mm});
            skLineSegment(sketch, "E755", {"start": v(-32.94, -42.64) * mm, "end": v(-33.63, -42.04) * mm});
            skLineSegment(sketch, "E756", {"start": v(-33.63, -42.04) * mm, "end": v(-34.3, -41.43) * mm});
            skLineSegment(sketch, "E757", {"start": v(-34.3, -41.43) * mm, "end": v(-34.98, -40.8) * mm});
            skLineSegment(sketch, "E758", {"start": v(-34.98, -40.8) * mm, "end": v(-35.64, -40.17) * mm});
            skLineSegment(sketch, "E759", {"start": v(-35.64, -40.17) * mm, "end": v(-36.28, -39.52) * mm});
            skLineSegment(sketch, "E760", {"start": v(-36.28, -39.52) * mm, "end": v(-36.92, -38.86) * mm});
            skLineSegment(sketch, "E761", {"start": v(-36.92, -38.86) * mm, "end": v(-37.54, -38.19) * mm});
            skLineSegment(sketch, "E762", {"start": v(-37.54, -38.19) * mm, "end": v(-38.16, -37.5) * mm});
            skLineSegment(sketch, "E763", {"start": v(-38.16, -37.5) * mm, "end": v(-38.75, -36.81) * mm});
            skLineSegment(sketch, "E764", {"start": v(-38.75, -36.81) * mm, "end": v(-39.34, -36.1) * mm});
            skLineSegment(sketch, "E765", {"start": v(-39.34, -36.1) * mm, "end": v(-39.92, -35.4) * mm});
            skLineSegment(sketch, "E766", {"start": v(-39.92, -35.4) * mm, "end": v(-40.48, -34.67) * mm});
            skLineSegment(sketch, "E767", {"start": v(-40.48, -34.67) * mm, "end": v(-41.03, -33.93) * mm});
            skLineSegment(sketch, "E768", {"start": v(-41.03, -33.93) * mm, "end": v(-41.56, -33.18) * mm});
            skLineSegment(sketch, "E769", {"start": v(-41.56, -33.18) * mm, "end": v(-42.08, -32.43) * mm});
            skLineSegment(sketch, "E770", {"start": v(-42.08, -32.43) * mm, "end": v(-42.6, -31.66) * mm});
            skLineSegment(sketch, "E771", {"start": v(-42.6, -31.66) * mm, "end": v(-43.09, -30.89) * mm});
            skLineSegment(sketch, "E772", {"start": v(-43.09, -30.89) * mm, "end": v(-43.57, -30.1) * mm});
            skLineSegment(sketch, "E773", {"start": v(-43.57, -30.1) * mm, "end": v(-44.04, -29.3) * mm});
            skLineSegment(sketch, "E774", {"start": v(-44.04, -29.3) * mm, "end": v(-44.5, -28.5) * mm});
            skLineSegment(sketch, "E775", {"start": v(-44.5, -28.5) * mm, "end": v(-44.93, -27.7) * mm});
            skLineSegment(sketch, "E776", {"start": v(-44.93, -27.7) * mm, "end": v(-45.36, -26.87) * mm});
            skLineSegment(sketch, "E777", {"start": v(-45.36, -26.87) * mm, "end": v(-45.77, -26.04) * mm});
            skLineSegment(sketch, "E778", {"start": v(-45.77, -26.04) * mm, "end": v(-46.16, -25.2) * mm});
            skLineSegment(sketch, "E779", {"start": v(-46.16, -25.2) * mm, "end": v(-46.54, -24.35) * mm});
            skLineSegment(sketch, "E780", {"start": v(-46.54, -24.35) * mm, "end": v(-46.9, -23.5) * mm});
            skLineSegment(sketch, "E781", {"start": v(-46.9, -23.5) * mm, "end": v(-47.26, -22.64) * mm});
            skLineSegment(sketch, "E782", {"start": v(-47.26, -22.64) * mm, "end": v(-47.6, -21.77) * mm});
            skLineSegment(sketch, "E783", {"start": v(-47.6, -21.77) * mm, "end": v(-47.91, -20.89) * mm});
            skLineSegment(sketch, "E784", {"start": v(-47.91, -20.89) * mm, "end": v(-48.22, -20) * mm});
            skLineSegment(sketch, "E785", {"start": v(-48.22, -20) * mm, "end": v(-48.5, -19.1) * mm});
            skLineSegment(sketch, "E786", {"start": v(-48.5, -19.1) * mm, "end": v(-48.78, -18.2) * mm});
            skLineSegment(sketch, "E787", {"start": v(-48.78, -18.2) * mm, "end": v(-49.03, -17.3) * mm});
            skLineSegment(sketch, "E788", {"start": v(-49.03, -17.3) * mm, "end": v(-49.27, -16.39) * mm});
            skLineSegment(sketch, "E789", {"start": v(-49.27, -16.39) * mm, "end": v(-49.5, -15.47) * mm});
            skLineSegment(sketch, "E790", {"start": v(-49.5, -15.47) * mm, "end": v(-49.7, -14.54) * mm});
            skLineSegment(sketch, "E791", {"start": v(-49.7, -14.54) * mm, "end": v(-49.89, -13.6) * mm});
            skLineSegment(sketch, "E792", {"start": v(-49.89, -13.6) * mm, "end": v(-50.06, -12.67) * mm});
            skLineSegment(sketch, "E793", {"start": v(-50.06, -12.67) * mm, "end": v(-50.21, -11.72) * mm});
            skLineSegment(sketch, "E794", {"start": v(-50.21, -11.72) * mm, "end": v(-50.35, -10.77) * mm});
            skLineSegment(sketch, "E795", {"start": v(-50.35, -10.77) * mm, "end": v(-50.47, -9.82) * mm});
            skLineSegment(sketch, "E796", {"start": v(-50.47, -9.82) * mm, "end": v(-50.57, -8.85) * mm});
            skLineSegment(sketch, "E797", {"start": v(-50.57, -8.85) * mm, "end": v(-50.65, -7.89) * mm});
            skLineSegment(sketch, "E798", {"start": v(-50.65, -7.89) * mm, "end": v(-50.72, -6.92) * mm});
            skLineSegment(sketch, "E799", {"start": v(-50.72, -6.92) * mm, "end": v(-50.76, -5.94) * mm});
            skLineSegment(sketch, "E800", {"start": v(-50.76, -5.94) * mm, "end": v(-50.8, -4.96) * mm});
            skLineSegment(sketch, "E801", {"start": v(-50.8, -4.96) * mm, "end": v(-50.8, -3.97) * mm});
            skLineSegment(sketch, "E802", {"start": v(-50.8, -3.97) * mm, "end": v(-50.8, -3.1) * mm});
            skLineSegment(sketch, "E803", {"start": v(-50.8, -3.1) * mm, "end": v(-50.77, -2.24) * mm});
            skLineSegment(sketch, "E804", {"start": v(-50.77, -2.24) * mm, "end": v(-50.74, -1.39) * mm});
            skLineSegment(sketch, "E805", {"start": v(-50.74, -1.39) * mm, "end": v(-50.69, -0.53) * mm});
            skLineSegment(sketch, "E806", {"start": v(-50.69, -0.53) * mm, "end": v(-50.62, 0.32) * mm});
            skLineSegment(sketch, "E807", {"start": v(-50.62, 0.32) * mm, "end": v(-50.54, 1.17) * mm});
            skLineSegment(sketch, "E808", {"start": v(-50.54, 1.17) * mm, "end": v(-50.45, 2) * mm});
            skLineSegment(sketch, "E809", {"start": v(-50.45, 2) * mm, "end": v(-50.35, 2.85) * mm});
            skLineSegment(sketch, "E810", {"start": v(-50.35, 2.85) * mm, "end": v(-50.23, 3.68) * mm});
            skLineSegment(sketch, "E811", {"start": v(-50.23, 3.68) * mm, "end": v(-50.1, 4.51) * mm});
            skLineSegment(sketch, "E812", {"start": v(-50.1, 4.51) * mm, "end": v(-49.95, 5.34) * mm});
            skLineSegment(sketch, "E813", {"start": v(-49.95, 5.34) * mm, "end": v(-49.8, 6.16) * mm});
            skLineSegment(sketch, "E814", {"start": v(-49.8, 6.16) * mm, "end": v(-49.62, 6.97) * mm});
            skLineSegment(sketch, "E815", {"start": v(-49.62, 6.97) * mm, "end": v(-49.43, 7.78) * mm});
            skLineSegment(sketch, "E816", {"start": v(-49.43, 7.78) * mm, "end": v(-49.24, 8.59) * mm});
            skLineSegment(sketch, "E817", {"start": v(-49.24, 8.59) * mm, "end": v(-49.02, 9.39) * mm});
            skLineSegment(sketch, "E818", {"start": v(-49.02, 9.39) * mm, "end": v(-48.8, 10.18) * mm});
            skLineSegment(sketch, "E819", {"start": v(-48.8, 10.18) * mm, "end": v(-48.57, 10.97) * mm});
            skLineSegment(sketch, "E820", {"start": v(-48.57, 10.97) * mm, "end": v(-48.32, 11.76) * mm});
            skLineSegment(sketch, "E821", {"start": v(-48.32, 11.76) * mm, "end": v(-48.06, 12.54) * mm});
            skLineSegment(sketch, "E822", {"start": v(-48.06, 12.54) * mm, "end": v(-47.78, 13.31) * mm});
            skLineSegment(sketch, "E823", {"start": v(-47.78, 13.31) * mm, "end": v(-47.5, 14.08) * mm});
            skLineSegment(sketch, "E824", {"start": v(-47.5, 14.08) * mm, "end": v(-47.2, 14.84) * mm});
            skLineSegment(sketch, "E825", {"start": v(-47.2, 14.84) * mm, "end": v(-46.9, 15.6) * mm});
            skLineSegment(sketch, "E826", {"start": v(-46.9, 15.6) * mm, "end": v(-46.57, 16.35) * mm});
            skLineSegment(sketch, "E827", {"start": v(-46.57, 16.35) * mm, "end": v(-46.24, 17.1) * mm});
            skLineSegment(sketch, "E828", {"start": v(-46.24, 17.1) * mm, "end": v(-45.9, 17.83) * mm});
            skLineSegment(sketch, "E829", {"start": v(-45.9, 17.83) * mm, "end": v(-45.54, 18.56) * mm});
            skLineSegment(sketch, "E830", {"start": v(-45.54, 18.56) * mm, "end": v(-45.18, 19.28) * mm});
            skLineSegment(sketch, "E831", {"start": v(-45.18, 19.28) * mm, "end": v(-44.8, 20) * mm});
            skLineSegment(sketch, "E832", {"start": v(-44.8, 20) * mm, "end": v(-44.41, 20.71) * mm});
            skLineSegment(sketch, "E833", {"start": v(-44.41, 20.71) * mm, "end": v(-44.01, 21.41) * mm});
            skLineSegment(sketch, "E834", {"start": v(-44.01, 21.41) * mm, "end": v(-43.6, 22.11) * mm});
            skLineSegment(sketch, "E835", {"start": v(-43.6, 22.11) * mm, "end": v(-43.18, 22.8) * mm});
            skLineSegment(sketch, "E836", {"start": v(-43.18, 22.8) * mm, "end": v(-42.75, 23.48) * mm});
            skLineSegment(sketch, "E837", {"start": v(-42.75, 23.48) * mm, "end": v(-42.3, 24.16) * mm});
            skLineSegment(sketch, "E838", {"start": v(-42.3, 24.16) * mm, "end": v(-41.85, 24.82) * mm});
            skLineSegment(sketch, "E839", {"start": v(-41.85, 24.82) * mm, "end": v(-41.4, 25.48) * mm});
            skLineSegment(sketch, "E840", {"start": v(-41.4, 25.48) * mm, "end": v(-40.92, 26.14) * mm});
            skLineSegment(sketch, "E841", {"start": v(-40.92, 26.14) * mm, "end": v(-40.44, 26.78) * mm});
            skLineSegment(sketch, "E842", {"start": v(-40.44, 26.78) * mm, "end": v(-39.94, 27.42) * mm});
            skLineSegment(sketch, "E843", {"start": v(-39.94, 27.42) * mm, "end": v(-39.44, 28.04) * mm});
            skLineSegment(sketch, "E844", {"start": v(-39.44, 28.04) * mm, "end": v(-38.93, 28.66) * mm});
            skLineSegment(sketch, "E845", {"start": v(-38.93, 28.66) * mm, "end": v(-38.4, 29.28) * mm});
            skLineSegment(sketch, "E846", {"start": v(-38.4, 29.28) * mm, "end": v(-37.88, 29.88) * mm});
            skLineSegment(sketch, "E847", {"start": v(-37.88, 29.88) * mm, "end": v(-37.34, 30.47) * mm});
            skLineSegment(sketch, "E848", {"start": v(-37.34, 30.47) * mm, "end": v(-36.79, 31.06) * mm});
            skLineSegment(sketch, "E849", {"start": v(-36.79, 31.06) * mm, "end": v(-36.23, 31.64) * mm});
            skLineSegment(sketch, "E850", {"start": v(-36.23, 31.64) * mm, "end": v(-35.66, 32.2) * mm});
            skLineSegment(sketch, "E851", {"start": v(-35.66, 32.2) * mm, "end": v(-35.08, 32.77) * mm});
            skLineSegment(sketch, "E852", {"start": v(-35.08, 32.77) * mm, "end": v(-34.5, 33.32) * mm});
            skLineSegment(sketch, "E853", {"start": v(-34.5, 33.32) * mm, "end": v(-33.9, 33.86) * mm});
            skLineSegment(sketch, "E854", {"start": v(-33.9, 33.86) * mm, "end": v(-33.3, 34.39) * mm});
            skLineSegment(sketch, "E855", {"start": v(-33.3, 34.39) * mm, "end": v(-32.69, 34.91) * mm});
            skLineSegment(sketch, "E856", {"start": v(-32.69, 34.91) * mm, "end": v(-32.07, 35.42) * mm});
            skLineSegment(sketch, "E857", {"start": v(-32.07, 35.42) * mm, "end": v(-31.44, 35.93) * mm});
            skLineSegment(sketch, "E858", {"start": v(-31.44, 35.93) * mm, "end": v(-30.8, 36.42) * mm});
            skLineSegment(sketch, "E859", {"start": v(-30.8, 36.42) * mm, "end": v(-30.16, 36.9) * mm});
            skLineSegment(sketch, "E860", {"start": v(-30.16, 36.9) * mm, "end": v(-29.51, 37.38) * mm});
            skLineSegment(sketch, "E861", {"start": v(-29.51, 37.38) * mm, "end": v(-28.85, 37.84) * mm});
            skLineSegment(sketch, "E862", {"start": v(-28.85, 37.84) * mm, "end": v(-28.19, 38.3) * mm});
            skLineSegment(sketch, "E863", {"start": v(-28.19, 38.3) * mm, "end": v(-27.51, 38.74) * mm});
            skLineSegment(sketch, "E864", {"start": v(-27.51, 38.74) * mm, "end": v(-26.83, 39.17) * mm});
            skLineSegment(sketch, "E865", {"start": v(-26.83, 39.17) * mm, "end": v(-26.14, 39.6) * mm});
            skLineSegment(sketch, "E866", {"start": v(-26.14, 39.6) * mm, "end": v(-25.89, 40.36) * mm});
            skLineSegment(sketch, "E867", {"start": v(-25.89, 40.36) * mm, "end": v(-25.62, 41.11) * mm});
            skLineSegment(sketch, "E868", {"start": v(-25.62, 41.11) * mm, "end": v(-25.35, 41.86) * mm});
            skLineSegment(sketch, "E869", {"start": v(-25.35, 41.86) * mm, "end": v(-25.06, 42.6) * mm});
            skLineSegment(sketch, "E870", {"start": v(-25.06, 42.6) * mm, "end": v(-24.76, 43.31) * mm});
            skLineSegment(sketch, "E871", {"start": v(-24.76, 43.31) * mm, "end": v(-24.45, 44.01) * mm});
            skLineSegment(sketch, "E872", {"start": v(-24.45, 44.01) * mm, "end": v(-24.14, 44.7) * mm});
            skLineSegment(sketch, "E873", {"start": v(-24.14, 44.7) * mm, "end": v(-23.83, 45.36) * mm});
            skLineSegment(sketch, "E874", {"start": v(-23.83, 45.36) * mm, "end": v(-23.51, 46) * mm});
            skLineSegment(sketch, "E875", {"start": v(-23.51, 46) * mm, "end": v(-23.2, 46.6) * mm});
            skLineSegment(sketch, "E876", {"start": v(-23.2, 46.6) * mm, "end": v(-22.88, 47.2) * mm});
            skLineSegment(sketch, "E877", {"start": v(-22.88, 47.2) * mm, "end": v(-22.56, 47.74) * mm});
            skLineSegment(sketch, "E878", {"start": v(-22.56, 47.74) * mm, "end": v(-22.25, 48.27) * mm});
            skLineSegment(sketch, "E879", {"start": v(-22.25, 48.27) * mm, "end": v(-21.95, 48.76) * mm});
            skLineSegment(sketch, "E880", {"start": v(-21.95, 48.76) * mm, "end": v(-21.65, 49.2) * mm});
            skLineSegment(sketch, "E881", {"start": v(-21.65, 49.2) * mm, "end": v(-21.36, 49.62) * mm});
            skLineSegment(sketch, "E882", {"start": v(-21.36, 49.62) * mm, "end": v(-20.97, 50.16) * mm});
            skLineSegment(sketch, "E883", {"start": v(-20.97, 50.16) * mm, "end": v(-20.56, 50.67) * mm});
            skLineSegment(sketch, "E884", {"start": v(-20.56, 50.67) * mm, "end": v(-20.14, 51.17) * mm});
            skLineSegment(sketch, "E885", {"start": v(-20.14, 51.17) * mm, "end": v(-19.71, 51.66) * mm});
            skLineSegment(sketch, "E886", {"start": v(-19.71, 51.66) * mm, "end": v(-19.27, 52.14) * mm});
            skLineSegment(sketch, "E887", {"start": v(-19.27, 52.14) * mm, "end": v(-18.82, 52.6) * mm});
            skLineSegment(sketch, "E888", {"start": v(-18.82, 52.6) * mm, "end": v(-18.35, 53.04) * mm});
            skLineSegment(sketch, "E889", {"start": v(-18.35, 53.04) * mm, "end": v(-17.88, 53.47) * mm});
            skLineSegment(sketch, "E890", {"start": v(-17.88, 53.47) * mm, "end": v(-17.4, 53.88) * mm});
            skLineSegment(sketch, "E891", {"start": v(-17.4, 53.88) * mm, "end": v(-16.9, 54.28) * mm});
            skLineSegment(sketch, "E892", {"start": v(-16.9, 54.28) * mm, "end": v(-16.4, 54.66) * mm});
            skLineSegment(sketch, "E893", {"start": v(-16.4, 54.66) * mm, "end": v(-15.9, 55.03) * mm});
            skLineSegment(sketch, "E894", {"start": v(-15.9, 55.03) * mm, "end": v(-15.37, 55.39) * mm});
            skLineSegment(sketch, "E895", {"start": v(-15.37, 55.39) * mm, "end": v(-14.85, 55.73) * mm});
            skLineSegment(sketch, "E896", {"start": v(-14.85, 55.73) * mm, "end": v(-14.31, 56.05) * mm});
            skLineSegment(sketch, "E897", {"start": v(-14.31, 56.05) * mm, "end": v(-13.77, 56.36) * mm});
            skLineSegment(sketch, "E898", {"start": v(-13.77, 56.36) * mm, "end": v(-13.22, 56.65) * mm});
            skLineSegment(sketch, "E899", {"start": v(-13.22, 56.65) * mm, "end": v(-12.67, 56.93) * mm});
            skLineSegment(sketch, "E900", {"start": v(-12.67, 56.93) * mm, "end": v(-12.1, 57.2) * mm});
            skLineSegment(sketch, "E901", {"start": v(-12.1, 57.2) * mm, "end": v(-11.54, 57.45) * mm});
            skLineSegment(sketch, "E902", {"start": v(-11.54, 57.45) * mm, "end": v(-10.97, 57.68) * mm});
            skLineSegment(sketch, "E903", {"start": v(-10.97, 57.68) * mm, "end": v(-10.4, 57.9) * mm});
            skLineSegment(sketch, "E904", {"start": v(-10.4, 57.9) * mm, "end": v(-9.81, 58.1) * mm});
            skLineSegment(sketch, "E905", {"start": v(-9.81, 58.1) * mm, "end": v(-9.23, 58.3) * mm});
            skLineSegment(sketch, "E906", {"start": v(-9.23, 58.3) * mm, "end": v(-8.64, 58.47) * mm});
            skLineSegment(sketch, "E907", {"start": v(-8.64, 58.47) * mm, "end": v(-8.05, 58.63) * mm});
            skLineSegment(sketch, "E908", {"start": v(-8.05, 58.63) * mm, "end": v(-7.46, 58.78) * mm});
            skLineSegment(sketch, "E909", {"start": v(-7.46, 58.78) * mm, "end": v(-6.86, 58.9) * mm});
            skLineSegment(sketch, "E910", {"start": v(-6.86, 58.9) * mm, "end": v(-6.26, 59.02) * mm});
            skLineSegment(sketch, "E911", {"start": v(-6.26, 59.02) * mm, "end": v(-5.66, 59.12) * mm});
            skLineSegment(sketch, "E912", {"start": v(-5.66, 59.12) * mm, "end": v(-5.06, 59.2) * mm});
            skLineSegment(sketch, "E913", {"start": v(-5.06, 59.2) * mm, "end": v(-4.46, 59.27) * mm});
            skLineSegment(sketch, "E914", {"start": v(-4.46, 59.27) * mm, "end": v(-4.64, 59.58) * mm});
            skLineSegment(sketch, "E915", {"start": v(-4.64, 59.58) * mm, "end": v(-4.8, 59.9) * mm});
            skLineSegment(sketch, "E916", {"start": v(-4.8, 59.9) * mm, "end": v(-4.94, 60.24) * mm});
            skLineSegment(sketch, "E917", {"start": v(-4.94, 60.24) * mm, "end": v(-5.06, 60.59) * mm});
            skLineSegment(sketch, "E918", {"start": v(-5.06, 60.59) * mm, "end": v(-5.15, 60.95) * mm});
            skLineSegment(sketch, "E919", {"start": v(-5.15, 60.95) * mm, "end": v(-5.21, 61.31) * mm});
            skLineSegment(sketch, "E920", {"start": v(-5.21, 61.31) * mm, "end": v(-5.25, 61.69) * mm});
            skLineSegment(sketch, "E921", {"start": v(-5.25, 61.69) * mm, "end": v(-5.27, 62.07) * mm});
            skLineSegment(sketch, "E922", {"start": v(-5.27, 62.07) * mm, "end": v(-5.26, 62.34) * mm});
            skLineSegment(sketch, "E923", {"start": v(-5.26, 62.34) * mm, "end": v(-5.24, 62.6) * mm});
            skLineSegment(sketch, "E924", {"start": v(-5.24, 62.6) * mm, "end": v(-5.2, 62.87) * mm});
            skLineSegment(sketch, "E925", {"start": v(-5.2, 62.87) * mm, "end": v(-5.16, 63.13) * mm});
            skLineSegment(sketch, "E926", {"start": v(-5.16, 63.13) * mm, "end": v(-5.1, 63.39) * mm});
            skLineSegment(sketch, "E927", {"start": v(-5.1, 63.39) * mm, "end": v(-5.03, 63.64) * mm});
            skLineSegment(sketch, "E928", {"start": v(-5.03, 63.64) * mm, "end": v(-4.95, 63.88) * mm});
            skLineSegment(sketch, "E929", {"start": v(-4.95, 63.88) * mm, "end": v(-4.85, 64.12) * mm});
            skLineSegment(sketch, "E930", {"start": v(-4.85, 64.12) * mm, "end": v(-4.75, 64.35) * mm});
            skLineSegment(sketch, "E931", {"start": v(-4.75, 64.35) * mm, "end": v(-4.63, 64.58) * mm});
            skLineSegment(sketch, "E932", {"start": v(-4.63, 64.58) * mm, "end": v(-4.5, 64.8) * mm});
            skLineSegment(sketch, "E933", {"start": v(-4.5, 64.8) * mm, "end": v(-4.37, 65.01) * mm});
            skLineSegment(sketch, "E934", {"start": v(-4.37, 65.01) * mm, "end": v(-4.22, 65.22) * mm});
            skLineSegment(sketch, "E935", {"start": v(-4.22, 65.22) * mm, "end": v(-4.06, 65.42) * mm});
            skLineSegment(sketch, "E936", {"start": v(-4.06, 65.42) * mm, "end": v(-3.9, 65.61) * mm});
            skLineSegment(sketch, "E937", {"start": v(-3.9, 65.61) * mm, "end": v(-3.72, 65.8) * mm});
            skLineSegment(sketch, "E938", {"start": v(-3.72, 65.8) * mm, "end": v(-3.54, 65.97) * mm});
            skLineSegment(sketch, "E939", {"start": v(-3.54, 65.97) * mm, "end": v(-3.35, 66.13) * mm});
            skLineSegment(sketch, "E940", {"start": v(-3.35, 66.13) * mm, "end": v(-3.15, 66.3) * mm});
            skLineSegment(sketch, "E941", {"start": v(-3.15, 66.3) * mm, "end": v(-2.94, 66.44) * mm});
            skLineSegment(sketch, "E942", {"start": v(-2.94, 66.44) * mm, "end": v(-2.73, 66.57) * mm});
            skLineSegment(sketch, "E943", {"start": v(-2.73, 66.57) * mm, "end": v(-2.51, 66.7) * mm});
            skLineSegment(sketch, "E944", {"start": v(-2.51, 66.7) * mm, "end": v(-2.28, 66.82) * mm});
            skLineSegment(sketch, "E945", {"start": v(-2.28, 66.82) * mm, "end": v(-2.05, 66.92) * mm});
            skLineSegment(sketch, "E946", {"start": v(-2.05, 66.92) * mm, "end": v(-1.81, 67.02) * mm});
            skLineSegment(sketch, "E947", {"start": v(-1.81, 67.02) * mm, "end": v(-1.57, 67.1) * mm});
            skLineSegment(sketch, "E948", {"start": v(-1.57, 67.1) * mm, "end": v(-1.32, 67.17) * mm});
            skLineSegment(sketch, "E949", {"start": v(-1.32, 67.17) * mm, "end": v(-1.06, 67.23) * mm});
            skLineSegment(sketch, "E950", {"start": v(-1.06, 67.23) * mm, "end": v(-0.8, 67.28) * mm});
            skLineSegment(sketch, "E951", {"start": v(-0.8, 67.28) * mm, "end": v(-0.54, 67.3) * mm});
            skLineSegment(sketch, "E952", {"start": v(-0.54, 67.3) * mm, "end": v(-0.27, 67.33) * mm});
            skLineSegment(sketch, "E953", {"start": v(-0.27, 67.33) * mm, "end": v(0, 67.34) * mm});
            skLineSegment(sketch, "E954", {"start": v(0, 64.8) * mm, "end": v(0.28, 64.78) * mm});
            skLineSegment(sketch, "E955", {"start": v(0.28, 64.78) * mm, "end": v(0.55, 64.74) * mm});
            skLineSegment(sketch, "E956", {"start": v(0.55, 64.74) * mm, "end": v(0.81, 64.67) * mm});
            skLineSegment(sketch, "E957", {"start": v(0.81, 64.67) * mm, "end": v(1.06, 64.58) * mm});
            skLineSegment(sketch, "E958", {"start": v(1.06, 64.58) * mm, "end": v(1.3, 64.47) * mm});
            skLineSegment(sketch, "E959", {"start": v(1.3, 64.47) * mm, "end": v(1.52, 64.33) * mm});
            skLineSegment(sketch, "E960", {"start": v(1.52, 64.33) * mm, "end": v(1.73, 64.17) * mm});
            skLineSegment(sketch, "E961", {"start": v(1.73, 64.17) * mm, "end": v(1.93, 64) * mm});
            skLineSegment(sketch, "E962", {"start": v(1.93, 64) * mm, "end": v(2.1, 63.8) * mm});
            skLineSegment(sketch, "E963", {"start": v(2.1, 63.8) * mm, "end": v(2.26, 63.6) * mm});
            skLineSegment(sketch, "E964", {"start": v(2.26, 63.6) * mm, "end": v(2.4, 63.37) * mm});
            skLineSegment(sketch, "E965", {"start": v(2.4, 63.37) * mm, "end": v(2.51, 63.13) * mm});
            skLineSegment(sketch, "E966", {"start": v(2.51, 63.13) * mm, "end": v(2.6, 62.88) * mm});
            skLineSegment(sketch, "E967", {"start": v(2.6, 62.88) * mm, "end": v(2.67, 62.62) * mm});
            skLineSegment(sketch, "E968", {"start": v(2.67, 62.62) * mm, "end": v(2.71, 62.35) * mm});
            skLineSegment(sketch, "E969", {"start": v(2.71, 62.35) * mm, "end": v(2.73, 62.07) * mm});
            skLineSegment(sketch, "E970", {"start": v(2.73, 62.07) * mm, "end": v(2.71, 61.8) * mm});
            skLineSegment(sketch, "E971", {"start": v(2.71, 61.8) * mm, "end": v(2.67, 61.52) * mm});
            skLineSegment(sketch, "E972", {"start": v(2.67, 61.52) * mm, "end": v(2.6, 61.26) * mm});
            skLineSegment(sketch, "E973", {"start": v(2.6, 61.26) * mm, "end": v(2.51, 61) * mm});
            skLineSegment(sketch, "E974", {"start": v(2.51, 61) * mm, "end": v(2.4, 60.77) * mm});
            skLineSegment(sketch, "E975", {"start": v(2.4, 60.77) * mm, "end": v(2.26, 60.55) * mm});
            skLineSegment(sketch, "E976", {"start": v(2.26, 60.55) * mm, "end": v(2.1, 60.34) * mm});
            skLineSegment(sketch, "E977", {"start": v(2.1, 60.34) * mm, "end": v(1.93, 60.14) * mm});
            skLineSegment(sketch, "E978", {"start": v(1.93, 60.14) * mm, "end": v(1.73, 59.97) * mm});
            skLineSegment(sketch, "E979", {"start": v(1.73, 59.97) * mm, "end": v(1.52, 59.8) * mm});
            skLineSegment(sketch, "E980", {"start": v(1.52, 59.8) * mm, "end": v(1.3, 59.67) * mm});
            skLineSegment(sketch, "E981", {"start": v(1.3, 59.67) * mm, "end": v(1.06, 59.56) * mm});
            skLineSegment(sketch, "E982", {"start": v(1.06, 59.56) * mm, "end": v(0.81, 59.47) * mm});
            skLineSegment(sketch, "E983", {"start": v(0.81, 59.47) * mm, "end": v(0.55, 59.4) * mm});
            skLineSegment(sketch, "E984", {"start": v(0.55, 59.4) * mm, "end": v(0.28, 59.36) * mm});
            skLineSegment(sketch, "E985", {"start": v(0.28, 59.36) * mm, "end": v(0, 59.34) * mm});
            skLineSegment(sketch, "E986", {"start": v(0, 59.34) * mm, "end": v(-0.28, 59.36) * mm});
            skLineSegment(sketch, "E987", {"start": v(-0.28, 59.36) * mm, "end": v(-0.55, 59.4) * mm});
            skLineSegment(sketch, "E988", {"start": v(-0.55, 59.4) * mm, "end": v(-0.81, 59.47) * mm});
            skLineSegment(sketch, "E989", {"start": v(-0.81, 59.47) * mm, "end": v(-1.06, 59.56) * mm});
            skLineSegment(sketch, "E990", {"start": v(-1.06, 59.56) * mm, "end": v(-1.3, 59.67) * mm});
            skLineSegment(sketch, "E991", {"start": v(-1.3, 59.67) * mm, "end": v(-1.52, 59.8) * mm});
            skLineSegment(sketch, "E992", {"start": v(-1.52, 59.8) * mm, "end": v(-1.73, 59.97) * mm});
            skLineSegment(sketch, "E993", {"start": v(-1.73, 59.97) * mm, "end": v(-1.93, 60.14) * mm});
            skLineSegment(sketch, "E994", {"start": v(-1.93, 60.14) * mm, "end": v(-2.1, 60.34) * mm});
            skLineSegment(sketch, "E995", {"start": v(-2.1, 60.34) * mm, "end": v(-2.26, 60.55) * mm});
            skLineSegment(sketch, "E996", {"start": v(-2.26, 60.55) * mm, "end": v(-2.4, 60.77) * mm});
            skLineSegment(sketch, "E997", {"start": v(-2.4, 60.77) * mm, "end": v(-2.51, 61) * mm});
            skLineSegment(sketch, "E998", {"start": v(-2.51, 61) * mm, "end": v(-2.6, 61.26) * mm});
            skLineSegment(sketch, "E999", {"start": v(-2.6, 61.26) * mm, "end": v(-2.67, 61.52) * mm});
            skLineSegment(sketch, "E1000", {"start": v(-2.67, 61.52) * mm, "end": v(-2.71, 61.8) * mm});
            skLineSegment(sketch, "E1001", {"start": v(-2.71, 61.8) * mm, "end": v(-2.73, 62.07) * mm});
            skLineSegment(sketch, "E1002", {"start": v(-2.73, 62.07) * mm, "end": v(-2.71, 62.35) * mm});
            skLineSegment(sketch, "E1003", {"start": v(-2.71, 62.35) * mm, "end": v(-2.67, 62.62) * mm});
            skLineSegment(sketch, "E1004", {"start": v(-2.67, 62.62) * mm, "end": v(-2.6, 62.88) * mm});
            skLineSegment(sketch, "E1005", {"start": v(-2.6, 62.88) * mm, "end": v(-2.51, 63.13) * mm});
            skLineSegment(sketch, "E1006", {"start": v(-2.51, 63.13) * mm, "end": v(-2.4, 63.37) * mm});
            skLineSegment(sketch, "E1007", {"start": v(-2.4, 63.37) * mm, "end": v(-2.26, 63.6) * mm});
            skLineSegment(sketch, "E1008", {"start": v(-2.26, 63.6) * mm, "end": v(-2.1, 63.8) * mm});
            skLineSegment(sketch, "E1009", {"start": v(-2.1, 63.8) * mm, "end": v(-1.93, 64) * mm});
            skLineSegment(sketch, "E1010", {"start": v(-1.93, 64) * mm, "end": v(-1.73, 64.17) * mm});
            skLineSegment(sketch, "E1011", {"start": v(-1.73, 64.17) * mm, "end": v(-1.52, 64.33) * mm});
            skLineSegment(sketch, "E1012", {"start": v(-1.52, 64.33) * mm, "end": v(-1.3, 64.47) * mm});
            skLineSegment(sketch, "E1013", {"start": v(-1.3, 64.47) * mm, "end": v(-1.06, 64.58) * mm});
            skLineSegment(sketch, "E1014", {"start": v(-1.06, 64.58) * mm, "end": v(-0.81, 64.67) * mm});
            skLineSegment(sketch, "E1015", {"start": v(-0.81, 64.67) * mm, "end": v(-0.55, 64.74) * mm});
            skLineSegment(sketch, "E1016", {"start": v(-0.55, 64.74) * mm, "end": v(-0.28, 64.78) * mm});
            skLineSegment(sketch, "E1017", {"start": v(-0.28, 64.78) * mm, "end": v(0, 64.8) * mm});
            skLineSegment(sketch, "E1018", {"start": v(-3.47, -49.56) * mm, "end": v(-2.61, -49.61) * mm});
            skLineSegment(sketch, "E1019", {"start": v(-2.61, -49.61) * mm, "end": v(-1.75, -49.66) * mm});
            skLineSegment(sketch, "E1020", {"start": v(-1.75, -49.66) * mm, "end": v(-0.87, -49.68) * mm});
            skLineSegment(sketch, "E1021", {"start": v(-0.87, -49.68) * mm, "end": v(0, -49.7) * mm});
            skLineSegment(sketch, "E1022", {"start": v(0, -49.7) * mm, "end": v(1.18, -49.68) * mm});
            skLineSegment(sketch, "E1023", {"start": v(1.18, -49.68) * mm, "end": v(2.35, -49.63) * mm});
            skLineSegment(sketch, "E1024", {"start": v(2.35, -49.63) * mm, "end": v(3.52, -49.56) * mm});
            skLineSegment(sketch, "E1025", {"start": v(3.52, -49.56) * mm, "end": v(4.67, -49.45) * mm});
            skLineSegment(sketch, "E1026", {"start": v(4.67, -49.45) * mm, "end": v(5.82, -49.32) * mm});
            skLineSegment(sketch, "E1027", {"start": v(5.82, -49.32) * mm, "end": v(6.96, -49.16) * mm});
            skLineSegment(sketch, "E1028", {"start": v(6.96, -49.16) * mm, "end": v(8.1, -48.98) * mm});
            skLineSegment(sketch, "E1029", {"start": v(8.1, -48.98) * mm, "end": v(9.21, -48.76) * mm});
            skLineSegment(sketch, "E1030", {"start": v(9.21, -48.76) * mm, "end": v(10.33, -48.52) * mm});
            skLineSegment(sketch, "E1031", {"start": v(10.33, -48.52) * mm, "end": v(11.43, -48.25) * mm});
            skLineSegment(sketch, "E1032", {"start": v(11.43, -48.25) * mm, "end": v(12.52, -47.96) * mm});
            skLineSegment(sketch, "E1033", {"start": v(12.52, -47.96) * mm, "end": v(13.6, -47.63) * mm});
            skLineSegment(sketch, "E1034", {"start": v(13.6, -47.63) * mm, "end": v(14.66, -47.29) * mm});
            skLineSegment(sketch, "E1035", {"start": v(14.66, -47.29) * mm, "end": v(15.72, -46.92) * mm});
            skLineSegment(sketch, "E1036", {"start": v(15.72, -46.92) * mm, "end": v(16.76, -46.52) * mm});
            skLineSegment(sketch, "E1037", {"start": v(16.76, -46.52) * mm, "end": v(17.8, -46.1) * mm});
            skLineSegment(sketch, "E1038", {"start": v(17.8, -46.1) * mm, "end": v(18.82, -45.65) * mm});
            skLineSegment(sketch, "E1039", {"start": v(18.82, -45.65) * mm, "end": v(19.82, -45.18) * mm});
            skLineSegment(sketch, "E1040", {"start": v(19.82, -45.18) * mm, "end": v(20.81, -44.69) * mm});
            skLineSegment(sketch, "E1041", {"start": v(20.81, -44.69) * mm, "end": v(21.8, -44.17) * mm});
            skLineSegment(sketch, "E1042", {"start": v(21.8, -44.17) * mm, "end": v(22.76, -43.63) * mm});
            skLineSegment(sketch, "E1043", {"start": v(22.76, -43.63) * mm, "end": v(23.7, -43.07) * mm});
            skLineSegment(sketch, "E1044", {"start": v(23.7, -43.07) * mm, "end": v(24.64, -42.49) * mm});
            skLineSegment(sketch, "E1045", {"start": v(24.64, -42.49) * mm, "end": v(25.56, -41.88) * mm});
            skLineSegment(sketch, "E1046", {"start": v(25.56, -41.88) * mm, "end": v(26.47, -41.26) * mm});
            skLineSegment(sketch, "E1047", {"start": v(26.47, -41.26) * mm, "end": v(27.36, -40.6) * mm});
            skLineSegment(sketch, "E1048", {"start": v(27.36, -40.6) * mm, "end": v(28.23, -39.94) * mm});
            skLineSegment(sketch, "E1049", {"start": v(28.23, -39.94) * mm, "end": v(29.08, -39.25) * mm});
            skLineSegment(sketch, "E1050", {"start": v(29.08, -39.25) * mm, "end": v(29.92, -38.54) * mm});
            skLineSegment(sketch, "E1051", {"start": v(29.92, -38.54) * mm, "end": v(30.74, -37.81) * mm});
            skLineSegment(sketch, "E1052", {"start": v(30.74, -37.81) * mm, "end": v(31.54, -37.07) * mm});
            skLineSegment(sketch, "E1053", {"start": v(31.54, -37.07) * mm, "end": v(32.33, -36.3) * mm});
            skLineSegment(sketch, "E1054", {"start": v(32.33, -36.3) * mm, "end": v(33.1, -35.51) * mm});
            skLineSegment(sketch, "E1055", {"start": v(33.1, -35.51) * mm, "end": v(33.84, -34.71) * mm});
            skLineSegment(sketch, "E1056", {"start": v(33.84, -34.71) * mm, "end": v(34.57, -33.9) * mm});
            skLineSegment(sketch, "E1057", {"start": v(34.57, -33.9) * mm, "end": v(35.28, -33.05) * mm});
            skLineSegment(sketch, "E1058", {"start": v(35.28, -33.05) * mm, "end": v(35.97, -32.2) * mm});
            skLineSegment(sketch, "E1059", {"start": v(35.97, -32.2) * mm, "end": v(36.64, -31.33) * mm});
            skLineSegment(sketch, "E1060", {"start": v(36.64, -31.33) * mm, "end": v(37.28, -30.44) * mm});
            skLineSegment(sketch, "E1061", {"start": v(37.28, -30.44) * mm, "end": v(37.91, -29.53) * mm});
            skLineSegment(sketch, "E1062", {"start": v(37.91, -29.53) * mm, "end": v(38.52, -28.61) * mm});
            skLineSegment(sketch, "E1063", {"start": v(38.52, -28.61) * mm, "end": v(39.1, -27.68) * mm});
            skLineSegment(sketch, "E1064", {"start": v(39.1, -27.68) * mm, "end": v(39.66, -26.73) * mm});
            skLineSegment(sketch, "E1065", {"start": v(39.66, -26.73) * mm, "end": v(40.2, -25.76) * mm});
            skLineSegment(sketch, "E1066", {"start": v(40.2, -25.76) * mm, "end": v(40.72, -24.78) * mm});
            skLineSegment(sketch, "E1067", {"start": v(40.72, -24.78) * mm, "end": v(41.21, -23.8) * mm});
            skLineSegment(sketch, "E1068", {"start": v(41.21, -23.8) * mm, "end": v(41.68, -22.79) * mm});
            skLineSegment(sketch, "E1069", {"start": v(41.68, -22.79) * mm, "end": v(42.13, -21.77) * mm});
            skLineSegment(sketch, "E1070", {"start": v(42.13, -21.77) * mm, "end": v(42.55, -20.73) * mm});
            skLineSegment(sketch, "E1071", {"start": v(42.55, -20.73) * mm, "end": v(42.95, -19.7) * mm});
            skLineSegment(sketch, "E1072", {"start": v(42.95, -19.7) * mm, "end": v(43.32, -18.63) * mm});
            skLineSegment(sketch, "E1073", {"start": v(43.32, -18.63) * mm, "end": v(43.66, -17.57) * mm});
            skLineSegment(sketch, "E1074", {"start": v(43.66, -17.57) * mm, "end": v(43.99, -16.49) * mm});
            skLineSegment(sketch, "E1075", {"start": v(43.99, -16.49) * mm, "end": v(44.28, -15.4) * mm});
            skLineSegment(sketch, "E1076", {"start": v(44.28, -15.4) * mm, "end": v(44.55, -14.3) * mm});
            skLineSegment(sketch, "E1077", {"start": v(44.55, -14.3) * mm, "end": v(44.8, -13.18) * mm});
            skLineSegment(sketch, "E1078", {"start": v(44.8, -13.18) * mm, "end": v(45, -12.06) * mm});
            skLineSegment(sketch, "E1079", {"start": v(45, -12.06) * mm, "end": v(45.2, -10.93) * mm});
            skLineSegment(sketch, "E1080", {"start": v(45.2, -10.93) * mm, "end": v(45.35, -9.8) * mm});
            skLineSegment(sketch, "E1081", {"start": v(45.35, -9.8) * mm, "end": v(45.48, -8.64) * mm});
            skLineSegment(sketch, "E1082", {"start": v(45.48, -8.64) * mm, "end": v(45.59, -7.49) * mm});
            skLineSegment(sketch, "E1083", {"start": v(45.59, -7.49) * mm, "end": v(45.66, -6.32) * mm});
            skLineSegment(sketch, "E1084", {"start": v(45.66, -6.32) * mm, "end": v(45.7, -5.15) * mm});
            skLineSegment(sketch, "E1085", {"start": v(45.7, -5.15) * mm, "end": v(45.72, -3.97) * mm});
            skLineSegment(sketch, "E1086", {"start": v(45.72, -3.97) * mm, "end": v(45.71, -3.1) * mm});
            skLineSegment(sketch, "E1087", {"start": v(45.71, -3.1) * mm, "end": v(45.69, -2.23) * mm});
            skLineSegment(sketch, "E1088", {"start": v(45.69, -2.23) * mm, "end": v(45.65, -1.37) * mm});
            skLineSegment(sketch, "E1089", {"start": v(45.65, -1.37) * mm, "end": v(45.6, -0.52) * mm});
            skLineSegment(sketch, "E1090", {"start": v(45.6, -0.52) * mm, "end": v(45.52, 0.34) * mm});
            skLineSegment(sketch, "E1091", {"start": v(45.52, 0.34) * mm, "end": v(45.43, 1.19) * mm});
            skLineSegment(sketch, "E1092", {"start": v(45.43, 1.19) * mm, "end": v(45.33, 2.03) * mm});
            skLineSegment(sketch, "E1093", {"start": v(45.33, 2.03) * mm, "end": v(45.21, 2.87) * mm});
            skLineSegment(sketch, "E1094", {"start": v(45.21, 2.87) * mm, "end": v(45.08, 3.7) * mm});
            skLineSegment(sketch, "E1095", {"start": v(45.08, 3.7) * mm, "end": v(44.93, 4.53) * mm});
            skLineSegment(sketch, "E1096", {"start": v(44.93, 4.53) * mm, "end": v(44.77, 5.36) * mm});
            skLineSegment(sketch, "E1097", {"start": v(44.77, 5.36) * mm, "end": v(44.6, 6.17) * mm});
            skLineSegment(sketch, "E1098", {"start": v(44.6, 6.17) * mm, "end": v(44.4, 6.99) * mm});
            skLineSegment(sketch, "E1099", {"start": v(44.4, 6.99) * mm, "end": v(44.2, 7.8) * mm});
            skLineSegment(sketch, "E1100", {"start": v(44.2, 7.8) * mm, "end": v(43.97, 8.6) * mm});
            skLineSegment(sketch, "E1101", {"start": v(43.97, 8.6) * mm, "end": v(43.74, 9.4) * mm});
            skLineSegment(sketch, "E1102", {"start": v(43.74, 9.4) * mm, "end": v(43.49, 10.18) * mm});
            skLineSegment(sketch, "E1103", {"start": v(43.49, 10.18) * mm, "end": v(43.23, 10.96) * mm});
            skLineSegment(sketch, "E1104", {"start": v(43.23, 10.96) * mm, "end": v(42.95, 11.74) * mm});
            skLineSegment(sketch, "E1105", {"start": v(42.95, 11.74) * mm, "end": v(42.66, 12.5) * mm});
            skLineSegment(sketch, "E1106", {"start": v(42.66, 12.5) * mm, "end": v(42.36, 13.27) * mm});
            skLineSegment(sketch, "E1107", {"start": v(42.36, 13.27) * mm, "end": v(42.04, 14.03) * mm});
            skLineSegment(sketch, "E1108", {"start": v(42.04, 14.03) * mm, "end": v(41.7, 14.78) * mm});
            skLineSegment(sketch, "E1109", {"start": v(41.7, 14.78) * mm, "end": v(41.37, 15.52) * mm});
            skLineSegment(sketch, "E1110", {"start": v(41.37, 15.52) * mm, "end": v(41.01, 16.26) * mm});
            skLineSegment(sketch, "E1111", {"start": v(41.01, 16.26) * mm, "end": v(40.64, 16.99) * mm});
            skLineSegment(sketch, "E1112", {"start": v(40.64, 16.99) * mm, "end": v(40.26, 17.7) * mm});
            skLineSegment(sketch, "E1113", {"start": v(40.26, 17.7) * mm, "end": v(39.87, 18.42) * mm});
            skLineSegment(sketch, "E1114", {"start": v(39.87, 18.42) * mm, "end": v(39.47, 19.12) * mm});
            skLineSegment(sketch, "E1115", {"start": v(39.47, 19.12) * mm, "end": v(39.05, 19.82) * mm});
            skLineSegment(sketch, "E1116", {"start": v(39.05, 19.82) * mm, "end": v(38.62, 20.51) * mm});
            skLineSegment(sketch, "E1117", {"start": v(38.62, 20.51) * mm, "end": v(38.18, 21.2) * mm});
            skLineSegment(sketch, "E1118", {"start": v(38.18, 21.2) * mm, "end": v(37.73, 21.86) * mm});
            skLineSegment(sketch, "E1119", {"start": v(37.73, 21.86) * mm, "end": v(37.26, 22.53) * mm});
            skLineSegment(sketch, "E1120", {"start": v(37.26, 22.53) * mm, "end": v(36.79, 23.18) * mm});
            skLineSegment(sketch, "E1121", {"start": v(36.79, 23.18) * mm, "end": v(36.3, 23.83) * mm});
            skLineSegment(sketch, "E1122", {"start": v(36.3, 23.83) * mm, "end": v(35.8, 24.47) * mm});
            skLineSegment(sketch, "E1123", {"start": v(35.8, 24.47) * mm, "end": v(35.3, 25.1) * mm});
            skLineSegment(sketch, "E1124", {"start": v(35.3, 25.1) * mm, "end": v(34.77, 25.71) * mm});
            skLineSegment(sketch, "E1125", {"start": v(34.77, 25.71) * mm, "end": v(34.24, 26.32) * mm});
            skLineSegment(sketch, "E1126", {"start": v(34.24, 26.32) * mm, "end": v(33.7, 26.92) * mm});
            skLineSegment(sketch, "E1127", {"start": v(33.7, 26.92) * mm, "end": v(33.15, 27.51) * mm});
            skLineSegment(sketch, "E1128", {"start": v(33.15, 27.51) * mm, "end": v(32.59, 28.1) * mm});
            skLineSegment(sketch, "E1129", {"start": v(32.59, 28.1) * mm, "end": v(32.02, 28.66) * mm});
            skLineSegment(sketch, "E1130", {"start": v(32.02, 28.66) * mm, "end": v(31.43, 29.23) * mm});
            skLineSegment(sketch, "E1131", {"start": v(31.43, 29.23) * mm, "end": v(30.84, 29.78) * mm});
            skLineSegment(sketch, "E1132", {"start": v(30.84, 29.78) * mm, "end": v(30.24, 30.32) * mm});
            skLineSegment(sketch, "E1133", {"start": v(30.24, 30.32) * mm, "end": v(29.63, 30.84) * mm});
            skLineSegment(sketch, "E1134", {"start": v(29.63, 30.84) * mm, "end": v(29.01, 31.36) * mm});
            skLineSegment(sketch, "E1135", {"start": v(29.01, 31.36) * mm, "end": v(28.38, 31.87) * mm});
            skLineSegment(sketch, "E1136", {"start": v(28.38, 31.87) * mm, "end": v(27.74, 32.37) * mm});
            skLineSegment(sketch, "E1137", {"start": v(27.74, 32.37) * mm, "end": v(27.1, 32.85) * mm});
            skLineSegment(sketch, "E1138", {"start": v(27.1, 32.85) * mm, "end": v(26.44, 33.33) * mm});
            skLineSegment(sketch, "E1139", {"start": v(26.44, 33.33) * mm, "end": v(25.78, 33.8) * mm});
            skLineSegment(sketch, "E1140", {"start": v(25.78, 33.8) * mm, "end": v(25.1, 34.24) * mm});
            skLineSegment(sketch, "E1141", {"start": v(25.1, 34.24) * mm, "end": v(24.42, 34.68) * mm});
            skLineSegment(sketch, "E1142", {"start": v(24.42, 34.68) * mm, "end": v(23.73, 35.11) * mm});
            skLineSegment(sketch, "E1143", {"start": v(23.73, 35.11) * mm, "end": v(23.03, 35.53) * mm});
            skLineSegment(sketch, "E1144", {"start": v(23.03, 35.53) * mm, "end": v(22.33, 35.93) * mm});
            skLineSegment(sketch, "E1145", {"start": v(22.33, 35.93) * mm, "end": v(21.61, 36.32) * mm});
            skLineSegment(sketch, "E1146", {"start": v(21.61, 36.32) * mm, "end": v(20.9, 36.7) * mm});
            skLineSegment(sketch, "E1147", {"start": v(20.9, 36.7) * mm, "end": v(20.16, 37.07) * mm});
            skLineSegment(sketch, "E1148", {"start": v(20.16, 37.07) * mm, "end": v(19.43, 37.42) * mm});
            skLineSegment(sketch, "E1149", {"start": v(19.43, 37.42) * mm, "end": v(18.69, 37.77) * mm});
            skLineSegment(sketch, "E1150", {"start": v(18.69, 37.77) * mm, "end": v(18.7, 36.97) * mm});
            skLineSegment(sketch, "E1151", {"start": v(18.7, 36.97) * mm, "end": v(18.7, 36.17) * mm});
            skLineSegment(sketch, "E1152", {"start": v(18.7, 36.17) * mm, "end": v(18.68, 35.36) * mm});
            skLineSegment(sketch, "E1153", {"start": v(18.68, 35.36) * mm, "end": v(18.65, 34.54) * mm});
            skLineSegment(sketch, "E1154", {"start": v(18.65, 34.54) * mm, "end": v(18.6, 33.72) * mm});
            skLineSegment(sketch, "E1155", {"start": v(18.6, 33.72) * mm, "end": v(18.54, 32.9) * mm});
            skLineSegment(sketch, "E1156", {"start": v(18.54, 32.9) * mm, "end": v(18.46, 32.06) * mm});
            skLineSegment(sketch, "E1157", {"start": v(18.46, 32.06) * mm, "end": v(18.37, 31.22) * mm});
            skLineSegment(sketch, "E1158", {"start": v(18.37, 31.22) * mm, "end": v(18.26, 30.37) * mm});
            skLineSegment(sketch, "E1159", {"start": v(18.26, 30.37) * mm, "end": v(18.15, 29.52) * mm});
            skLineSegment(sketch, "E1160", {"start": v(18.15, 29.52) * mm, "end": v(18.02, 28.67) * mm});
            skLineSegment(sketch, "E1161", {"start": v(18.02, 28.67) * mm, "end": v(17.87, 27.8) * mm});
            skLineSegment(sketch, "E1162", {"start": v(17.87, 27.8) * mm, "end": v(17.72, 26.94) * mm});
            skLineSegment(sketch, "E1163", {"start": v(17.72, 26.94) * mm, "end": v(17.56, 26.07) * mm});
            skLineSegment(sketch, "E1164", {"start": v(17.56, 26.07) * mm, "end": v(17.39, 25.2) * mm});
            skLineSegment(sketch, "E1165", {"start": v(17.39, 25.2) * mm, "end": v(17.2, 24.32) * mm});
            skLineSegment(sketch, "E1166", {"start": v(17.2, 24.32) * mm, "end": v(16.8, 22.56) * mm});
            skLineSegment(sketch, "E1167", {"start": v(16.8, 22.56) * mm, "end": v(16.38, 20.78) * mm});
            skLineSegment(sketch, "E1168", {"start": v(16.38, 20.78) * mm, "end": v(15.93, 18.99) * mm});
            skLineSegment(sketch, "E1169", {"start": v(15.93, 18.99) * mm, "end": v(15.45, 17.19) * mm});
            skLineSegment(sketch, "E1170", {"start": v(15.45, 17.19) * mm, "end": v(14.95, 15.38) * mm});
            skLineSegment(sketch, "E1171", {"start": v(14.95, 15.38) * mm, "end": v(14.43, 13.56) * mm});
            skLineSegment(sketch, "E1172", {"start": v(14.43, 13.56) * mm, "end": v(13.36, 9.92) * mm});
            skLineSegment(sketch, "E1173", {"start": v(13.36, 9.92) * mm, "end": v(12.7, 7.58) * mm});
            skLineSegment(sketch, "E1174", {"start": v(12.7, 7.58) * mm, "end": v(13.27, 7.77) * mm});
            skLineSegment(sketch, "E1175", {"start": v(13.27, 7.77) * mm, "end": v(13.87, 7.96) * mm});
            skLineSegment(sketch, "E1176", {"start": v(13.87, 7.96) * mm, "end": v(15.08, 8.32) * mm});
            skLineSegment(sketch, "E1177", {"start": v(15.08, 8.32) * mm, "end": v(16.32, 8.65) * mm});
            skLineSegment(sketch, "E1178", {"start": v(16.32, 8.65) * mm, "end": v(17.55, 8.96) * mm});
            skLineSegment(sketch, "E1179", {"start": v(17.55, 8.96) * mm, "end": v(18.15, 9.1) * mm});
            skLineSegment(sketch, "E1180", {"start": v(18.15, 9.1) * mm, "end": v(18.74, 9.22) * mm});
            skLineSegment(sketch, "E1181", {"start": v(18.74, 9.22) * mm, "end": v(19.3, 9.34) * mm});
            skLineSegment(sketch, "E1182", {"start": v(19.3, 9.34) * mm, "end": v(19.86, 9.43) * mm});
            skLineSegment(sketch, "E1183", {"start": v(19.86, 9.43) * mm, "end": v(20.38, 9.52) * mm});
            skLineSegment(sketch, "E1184", {"start": v(20.38, 9.52) * mm, "end": v(20.87, 9.59) * mm});
            skLineSegment(sketch, "E1185", {"start": v(20.87, 9.59) * mm, "end": v(21.32, 9.64) * mm});
            skLineSegment(sketch, "E1186", {"start": v(21.32, 9.64) * mm, "end": v(21.74, 9.68) * mm});
            skLineSegment(sketch, "E1187", {"start": v(21.74, 9.68) * mm, "end": v(22.46, 9.72) * mm});
            skLineSegment(sketch, "E1188", {"start": v(22.46, 9.72) * mm, "end": v(23.15, 9.74) * mm});
            skLineSegment(sketch, "E1189", {"start": v(23.15, 9.74) * mm, "end": v(23.8, 9.76) * mm});
            skLineSegment(sketch, "E1190", {"start": v(23.8, 9.76) * mm, "end": v(24.44, 9.76) * mm});
            skLineSegment(sketch, "E1191", {"start": v(24.44, 9.76) * mm, "end": v(25.03, 9.74) * mm});
            skLineSegment(sketch, "E1192", {"start": v(25.03, 9.74) * mm, "end": v(25.6, 9.72) * mm});
            skLineSegment(sketch, "E1193", {"start": v(25.6, 9.72) * mm, "end": v(26.14, 9.68) * mm});
            skLineSegment(sketch, "E1194", {"start": v(26.14, 9.68) * mm, "end": v(26.65, 9.63) * mm});
            skLineSegment(sketch, "E1195", {"start": v(26.65, 9.63) * mm, "end": v(27.14, 9.57) * mm});
            skLineSegment(sketch, "E1196", {"start": v(27.14, 9.57) * mm, "end": v(27.6, 9.5) * mm});
            skLineSegment(sketch, "E1197", {"start": v(27.6, 9.5) * mm, "end": v(28.02, 9.4) * mm});
            skLineSegment(sketch, "E1198", {"start": v(28.02, 9.4) * mm, "end": v(28.43, 9.31) * mm});
            skLineSegment(sketch, "E1199", {"start": v(28.43, 9.31) * mm, "end": v(28.8, 9.2) * mm});
            skLineSegment(sketch, "E1200", {"start": v(28.8, 9.2) * mm, "end": v(29.16, 9.1) * mm});
            skLineSegment(sketch, "E1201", {"start": v(29.16, 9.1) * mm, "end": v(29.5, 8.97) * mm});
            skLineSegment(sketch, "E1202", {"start": v(29.5, 8.97) * mm, "end": v(29.8, 8.83) * mm});
            skLineSegment(sketch, "E1203", {"start": v(29.8, 8.83) * mm, "end": v(30.09, 8.69) * mm});
            skLineSegment(sketch, "E1204", {"start": v(30.09, 8.69) * mm, "end": v(30.35, 8.54) * mm});
            skLineSegment(sketch, "E1205", {"start": v(30.35, 8.54) * mm, "end": v(30.6, 8.38) * mm});
            skLineSegment(sketch, "E1206", {"start": v(30.6, 8.38) * mm, "end": v(30.81, 8.2) * mm});
            skLineSegment(sketch, "E1207", {"start": v(30.81, 8.2) * mm, "end": v(31.02, 8.03) * mm});
            skLineSegment(sketch, "E1208", {"start": v(31.02, 8.03) * mm, "end": v(31.2, 7.85) * mm});
            skLineSegment(sketch, "E1209", {"start": v(31.2, 7.85) * mm, "end": v(31.36, 7.66) * mm});
            skLineSegment(sketch, "E1210", {"start": v(31.36, 7.66) * mm, "end": v(31.5, 7.46) * mm});
            skLineSegment(sketch, "E1211", {"start": v(31.5, 7.46) * mm, "end": v(31.64, 7.26) * mm});
            skLineSegment(sketch, "E1212", {"start": v(31.64, 7.26) * mm, "end": v(31.75, 7.05) * mm});
            skLineSegment(sketch, "E1213", {"start": v(31.75, 7.05) * mm, "end": v(31.84, 6.84) * mm});
            skLineSegment(sketch, "E1214", {"start": v(31.84, 6.84) * mm, "end": v(31.92, 6.62) * mm});
            skLineSegment(sketch, "E1215", {"start": v(31.92, 6.62) * mm, "end": v(31.99, 6.4) * mm});
            skLineSegment(sketch, "E1216", {"start": v(31.99, 6.4) * mm, "end": v(32.04, 6.16) * mm});
            skLineSegment(sketch, "E1217", {"start": v(32.04, 6.16) * mm, "end": v(32.07, 5.93) * mm});
            skLineSegment(sketch, "E1218", {"start": v(32.07, 5.93) * mm, "end": v(32.1, 5.69) * mm});
            skLineSegment(sketch, "E1219", {"start": v(32.1, 5.69) * mm, "end": v(32.1, 5.45) * mm});
            skLineSegment(sketch, "E1220", {"start": v(32.1, 5.45) * mm, "end": v(32.1, 5.2) * mm});
            skLineSegment(sketch, "E1221", {"start": v(32.1, 5.2) * mm, "end": v(32.1, 4.95) * mm});
            skLineSegment(sketch, "E1222", {"start": v(32.1, 4.95) * mm, "end": v(32.07, 4.7) * mm});
            skLineSegment(sketch, "E1223", {"start": v(32.07, 4.7) * mm, "end": v(32.04, 4.45) * mm});
            skLineSegment(sketch, "E1224", {"start": v(32.04, 4.45) * mm, "end": v(32, 4.2) * mm});
            skLineSegment(sketch, "E1225", {"start": v(32, 4.2) * mm, "end": v(31.9, 3.68) * mm});
            skLineSegment(sketch, "E1226", {"start": v(31.9, 3.68) * mm, "end": v(31.75, 3.16) * mm});
            skLineSegment(sketch, "E1227", {"start": v(31.75, 3.16) * mm, "end": v(31.6, 2.63) * mm});
            skLineSegment(sketch, "E1228", {"start": v(31.6, 2.63) * mm, "end": v(31.4, 2.11) * mm});
            skLineSegment(sketch, "E1229", {"start": v(31.4, 2.11) * mm, "end": v(31.21, 1.6) * mm});
            skLineSegment(sketch, "E1230", {"start": v(31.21, 1.6) * mm, "end": v(30.8, 0.59) * mm});
            skLineSegment(sketch, "E1231", {"start": v(30.8, 0.59) * mm, "end": v(30.38, -0.38) * mm});
            skLineSegment(sketch, "E1232", {"start": v(30.38, -0.38) * mm, "end": v(30.19, -0.84) * mm});
            skLineSegment(sketch, "E1233", {"start": v(30.19, -0.84) * mm, "end": v(30, -1.27) * mm});
            skLineSegment(sketch, "E1234", {"start": v(30, -1.27) * mm, "end": v(29.85, -1.7) * mm});
            skLineSegment(sketch, "E1235", {"start": v(29.85, -1.7) * mm, "end": v(29.72, -2.08) * mm});
            skLineSegment(sketch, "E1236", {"start": v(29.72, -2.08) * mm, "end": v(29.62, -2.42) * mm});
            skLineSegment(sketch, "E1237", {"start": v(29.62, -2.42) * mm, "end": v(29.53, -2.76) * mm});
            skLineSegment(sketch, "E1238", {"start": v(29.53, -2.76) * mm, "end": v(29.38, -3.44) * mm});
            skLineSegment(sketch, "E1239", {"start": v(29.38, -3.44) * mm, "end": v(29.25, -4.1) * mm});
            skLineSegment(sketch, "E1240", {"start": v(29.25, -4.1) * mm, "end": v(29.15, -4.78) * mm});
            skLineSegment(sketch, "E1241", {"start": v(29.15, -4.78) * mm, "end": v(29.07, -5.44) * mm});
            skLineSegment(sketch, "E1242", {"start": v(29.07, -5.44) * mm, "end": v(29, -6.1) * mm});
            skLineSegment(sketch, "E1243", {"start": v(29, -6.1) * mm, "end": v(28.87, -7.43) * mm});
            skLineSegment(sketch, "E1244", {"start": v(28.87, -7.43) * mm, "end": v(28.8, -8.08) * mm});
            skLineSegment(sketch, "E1245", {"start": v(28.8, -8.08) * mm, "end": v(28.71, -8.74) * mm});
            skLineSegment(sketch, "E1246", {"start": v(28.71, -8.74) * mm, "end": v(28.62, -9.4) * mm});
            skLineSegment(sketch, "E1247", {"start": v(28.62, -9.4) * mm, "end": v(28.5, -10.04) * mm});
            skLineSegment(sketch, "E1248", {"start": v(28.5, -10.04) * mm, "end": v(28.42, -10.37) * mm});
            skLineSegment(sketch, "E1249", {"start": v(28.42, -10.37) * mm, "end": v(28.34, -10.7) * mm});
            skLineSegment(sketch, "E1250", {"start": v(28.34, -10.7) * mm, "end": v(28.25, -11.02) * mm});
            skLineSegment(sketch, "E1251", {"start": v(28.25, -11.02) * mm, "end": v(28.16, -11.35) * mm});
            skLineSegment(sketch, "E1252", {"start": v(28.16, -11.35) * mm, "end": v(28.05, -11.67) * mm});
            skLineSegment(sketch, "E1253", {"start": v(28.05, -11.67) * mm, "end": v(27.93, -12) * mm});
            skLineSegment(sketch, "E1254", {"start": v(27.93, -12) * mm, "end": v(27.8, -12.32) * mm});
            skLineSegment(sketch, "E1255", {"start": v(27.8, -12.32) * mm, "end": v(27.65, -12.65) * mm});
            skLineSegment(sketch, "E1256", {"start": v(27.65, -12.65) * mm, "end": v(27.5, -12.97) * mm});
            skLineSegment(sketch, "E1257", {"start": v(27.5, -12.97) * mm, "end": v(27.34, -13.27) * mm});
            skLineSegment(sketch, "E1258", {"start": v(27.34, -13.27) * mm, "end": v(27.16, -13.55) * mm});
            skLineSegment(sketch, "E1259", {"start": v(27.16, -13.55) * mm, "end": v(26.98, -13.82) * mm});
            skLineSegment(sketch, "E1260", {"start": v(26.98, -13.82) * mm, "end": v(26.8, -14.07) * mm});
            skLineSegment(sketch, "E1261", {"start": v(26.8, -14.07) * mm, "end": v(26.6, -14.3) * mm});
            skLineSegment(sketch, "E1262", {"start": v(26.6, -14.3) * mm, "end": v(26.4, -14.52) * mm});
            skLineSegment(sketch, "E1263", {"start": v(26.4, -14.52) * mm, "end": v(26.18, -14.72) * mm});
            skLineSegment(sketch, "E1264", {"start": v(26.18, -14.72) * mm, "end": v(25.96, -14.9) * mm});
            skLineSegment(sketch, "E1265", {"start": v(25.96, -14.9) * mm, "end": v(25.74, -15.07) * mm});
            skLineSegment(sketch, "E1266", {"start": v(25.74, -15.07) * mm, "end": v(25.5, -15.22) * mm});
            skLineSegment(sketch, "E1267", {"start": v(25.5, -15.22) * mm, "end": v(25.26, -15.36) * mm});
            skLineSegment(sketch, "E1268", {"start": v(25.26, -15.36) * mm, "end": v(25.02, -15.48) * mm});
            skLineSegment(sketch, "E1269", {"start": v(25.02, -15.48) * mm, "end": v(24.77, -15.59) * mm});
            skLineSegment(sketch, "E1270", {"start": v(24.77, -15.59) * mm, "end": v(24.51, -15.68) * mm});
            skLineSegment(sketch, "E1271", {"start": v(24.51, -15.68) * mm, "end": v(24.25, -15.76) * mm});
            skLineSegment(sketch, "E1272", {"start": v(24.25, -15.76) * mm, "end": v(23.98, -15.83) * mm});
            skLineSegment(sketch, "E1273", {"start": v(23.98, -15.83) * mm, "end": v(23.7, -15.88) * mm});
            skLineSegment(sketch, "E1274", {"start": v(23.7, -15.88) * mm, "end": v(23.43, -15.92) * mm});
            skLineSegment(sketch, "E1275", {"start": v(23.43, -15.92) * mm, "end": v(23.15, -15.95) * mm});
            skLineSegment(sketch, "E1276", {"start": v(23.15, -15.95) * mm, "end": v(22.86, -15.96) * mm});
            skLineSegment(sketch, "E1277", {"start": v(22.86, -15.96) * mm, "end": v(22.57, -15.96) * mm});
            skLineSegment(sketch, "E1278", {"start": v(22.57, -15.96) * mm, "end": v(22.28, -15.95) * mm});
            skLineSegment(sketch, "E1279", {"start": v(22.28, -15.95) * mm, "end": v(21.98, -15.93) * mm});
            skLineSegment(sketch, "E1280", {"start": v(21.98, -15.93) * mm, "end": v(21.68, -15.9) * mm});
            skLineSegment(sketch, "E1281", {"start": v(21.68, -15.9) * mm, "end": v(21.37, -15.86) * mm});
            skLineSegment(sketch, "E1282", {"start": v(21.37, -15.86) * mm, "end": v(21.06, -15.8) * mm});
            skLineSegment(sketch, "E1283", {"start": v(21.06, -15.8) * mm, "end": v(20.75, -15.74) * mm});
            skLineSegment(sketch, "E1284", {"start": v(20.75, -15.74) * mm, "end": v(20.44, -15.66) * mm});
            skLineSegment(sketch, "E1285", {"start": v(20.44, -15.66) * mm, "end": v(20.12, -15.58) * mm});
            skLineSegment(sketch, "E1286", {"start": v(20.12, -15.58) * mm, "end": v(19.8, -15.48) * mm});
            skLineSegment(sketch, "E1287", {"start": v(19.8, -15.48) * mm, "end": v(19.48, -15.38) * mm});
            skLineSegment(sketch, "E1288", {"start": v(19.48, -15.38) * mm, "end": v(18.84, -15.15) * mm});
            skLineSegment(sketch, "E1289", {"start": v(18.84, -15.15) * mm, "end": v(18.19, -14.88) * mm});
            skLineSegment(sketch, "E1290", {"start": v(18.19, -14.88) * mm, "end": v(17.54, -14.58) * mm});
            skLineSegment(sketch, "E1291", {"start": v(17.54, -14.58) * mm, "end": v(16.88, -14.25) * mm});
            skLineSegment(sketch, "E1292", {"start": v(16.88, -14.25) * mm, "end": v(16.23, -13.9) * mm});
            skLineSegment(sketch, "E1293", {"start": v(16.23, -13.9) * mm, "end": v(15.58, -13.52) * mm});
            skLineSegment(sketch, "E1294", {"start": v(15.58, -13.52) * mm, "end": v(14.93, -13.12) * mm});
            skLineSegment(sketch, "E1295", {"start": v(14.93, -13.12) * mm, "end": v(14.3, -12.7) * mm});
            skLineSegment(sketch, "E1296", {"start": v(14.3, -12.7) * mm, "end": v(13.66, -12.27) * mm});
            skLineSegment(sketch, "E1297", {"start": v(13.66, -12.27) * mm, "end": v(13.04, -11.82) * mm});
            skLineSegment(sketch, "E1298", {"start": v(13.04, -11.82) * mm, "end": v(12.43, -11.35) * mm});
            skLineSegment(sketch, "E1299", {"start": v(12.43, -11.35) * mm, "end": v(11.83, -10.88) * mm});
            skLineSegment(sketch, "E1300", {"start": v(11.83, -10.88) * mm, "end": v(11.25, -10.4) * mm});
            skLineSegment(sketch, "E1301", {"start": v(11.25, -10.4) * mm, "end": v(10.69, -9.9) * mm});
            skLineSegment(sketch, "E1302", {"start": v(10.69, -9.9) * mm, "end": v(10.14, -9.42) * mm});
            skLineSegment(sketch, "E1303", {"start": v(10.14, -9.42) * mm, "end": v(9.62, -8.92) * mm});
            skLineSegment(sketch, "E1304", {"start": v(9.62, -8.92) * mm, "end": v(10.16, -11.47) * mm});
            skLineSegment(sketch, "E1305", {"start": v(10.16, -11.47) * mm, "end": v(10.16, -11.47) * mm});
            skLineSegment(sketch, "E1306", {"start": v(10.16, -11.47) * mm, "end": v(10.26, -11.7) * mm});
            skLineSegment(sketch, "E1307", {"start": v(10.26, -11.7) * mm, "end": v(10.36, -12) * mm});
            skLineSegment(sketch, "E1308", {"start": v(10.36, -12) * mm, "end": v(10.47, -12.34) * mm});
            skLineSegment(sketch, "E1309", {"start": v(10.47, -12.34) * mm, "end": v(10.58, -12.75) * mm});
            skLineSegment(sketch, "E1310", {"start": v(10.58, -12.75) * mm, "end": v(10.85, -13.71) * mm});
            skLineSegment(sketch, "E1311", {"start": v(10.85, -13.71) * mm, "end": v(11.12, -14.64) * mm});
            skLineSegment(sketch, "E1312", {"start": v(11.12, -14.64) * mm, "end": v(11.42, -15.54) * mm});
            skLineSegment(sketch, "E1313", {"start": v(11.42, -15.54) * mm, "end": v(11.74, -16.44) * mm});
            skLineSegment(sketch, "E1314", {"start": v(11.74, -16.44) * mm, "end": v(12.22, -17.73) * mm});
            skLineSegment(sketch, "E1315", {"start": v(12.22, -17.73) * mm, "end": v(12.74, -19.09) * mm});
            skLineSegment(sketch, "E1316", {"start": v(12.74, -19.09) * mm, "end": v(13.3, -20.48) * mm});
            skLineSegment(sketch, "E1317", {"start": v(13.3, -20.48) * mm, "end": v(13.9, -21.89) * mm});
            skLineSegment(sketch, "E1318", {"start": v(13.9, -21.89) * mm, "end": v(14.2, -22.6) * mm});
            skLineSegment(sketch, "E1319", {"start": v(14.2, -22.6) * mm, "end": v(14.51, -23.28) * mm});
            skLineSegment(sketch, "E1320", {"start": v(14.51, -23.28) * mm, "end": v(14.83, -23.97) * mm});
            skLineSegment(sketch, "E1321", {"start": v(14.83, -23.97) * mm, "end": v(15.15, -24.64) * mm});
            skLineSegment(sketch, "E1322", {"start": v(15.15, -24.64) * mm, "end": v(15.48, -25.3) * mm});
            skLineSegment(sketch, "E1323", {"start": v(15.48, -25.3) * mm, "end": v(15.81, -25.93) * mm});
            skLineSegment(sketch, "E1324", {"start": v(15.81, -25.93) * mm, "end": v(16.15, -26.54) * mm});
            skLineSegment(sketch, "E1325", {"start": v(16.15, -26.54) * mm, "end": v(16.49, -27.12) * mm});
            skLineSegment(sketch, "E1326", {"start": v(16.49, -27.12) * mm, "end": v(16.72, -27.49) * mm});
            skLineSegment(sketch, "E1327", {"start": v(16.72, -27.49) * mm, "end": v(16.98, -27.87) * mm});
            skLineSegment(sketch, "E1328", {"start": v(16.98, -27.87) * mm, "end": v(17.26, -28.26) * mm});
            skLineSegment(sketch, "E1329", {"start": v(17.26, -28.26) * mm, "end": v(17.54, -28.67) * mm});
            skLineSegment(sketch, "E1330", {"start": v(17.54, -28.67) * mm, "end": v(17.8, -29.1) * mm});
            skLineSegment(sketch, "E1331", {"start": v(17.8, -29.1) * mm, "end": v(17.92, -29.31) * mm});
            skLineSegment(sketch, "E1332", {"start": v(17.92, -29.31) * mm, "end": v(18.03, -29.53) * mm});
            skLineSegment(sketch, "E1333", {"start": v(18.03, -29.53) * mm, "end": v(18.13, -29.75) * mm});
            skLineSegment(sketch, "E1334", {"start": v(18.13, -29.75) * mm, "end": v(18.21, -29.98) * mm});
            skLineSegment(sketch, "E1335", {"start": v(18.21, -29.98) * mm, "end": v(18.28, -30.2) * mm});
            skLineSegment(sketch, "E1336", {"start": v(18.28, -30.2) * mm, "end": v(18.32, -30.43) * mm});
            skLineSegment(sketch, "E1337", {"start": v(18.32, -30.43) * mm, "end": v(10.92, -28.27) * mm});
            skLineSegment(sketch, "E1338", {"start": v(10.92, -28.27) * mm, "end": v(10.8, -28.34) * mm});
            skLineSegment(sketch, "E1339", {"start": v(10.8, -28.34) * mm, "end": v(10.75, -28.37) * mm});
            skLineSegment(sketch, "E1340", {"start": v(10.75, -28.37) * mm, "end": v(10.55, -28.58) * mm});
            skLineSegment(sketch, "E1341", {"start": v(10.55, -28.58) * mm, "end": v(10.45, -28.7) * mm});
            skLineSegment(sketch, "E1342", {"start": v(10.45, -28.7) * mm, "end": v(10.39, -28.78) * mm});
            skLineSegment(sketch, "E1343", {"start": v(10.39, -28.78) * mm, "end": v(10.25, -29) * mm});
            skLineSegment(sketch, "E1344", {"start": v(10.25, -29) * mm, "end": v(10.05, -29.4) * mm});
            skLineSegment(sketch, "E1345", {"start": v(10.05, -29.4) * mm, "end": v(9.85, -29.83) * mm});
            skLineSegment(sketch, "E1346", {"start": v(9.85, -29.83) * mm, "end": v(9.45, -30.64) * mm});
            skLineSegment(sketch, "E1347", {"start": v(9.45, -30.64) * mm, "end": v(9.03, -31.48) * mm});
            skLineSegment(sketch, "E1348", {"start": v(9.03, -31.48) * mm, "end": v(8.68, -32.23) * mm});
            skLineSegment(sketch, "E1349", {"start": v(8.68, -32.23) * mm, "end": v(8.23, -33.2) * mm});
            skLineSegment(sketch, "E1350", {"start": v(8.23, -33.2) * mm, "end": v(7.99, -33.67) * mm});
            skLineSegment(sketch, "E1351", {"start": v(7.99, -33.67) * mm, "end": v(7.75, -34.11) * mm});
            skLineSegment(sketch, "E1352", {"start": v(7.75, -34.11) * mm, "end": v(7.63, -34.3) * mm});
            skLineSegment(sketch, "E1353", {"start": v(7.63, -34.3) * mm, "end": v(7.52, -34.47) * mm});
            skLineSegment(sketch, "E1354", {"start": v(7.52, -34.47) * mm, "end": v(7.42, -34.62) * mm});
            skLineSegment(sketch, "E1355", {"start": v(7.42, -34.62) * mm, "end": v(7.32, -34.73) * mm});
            skLineSegment(sketch, "E1356", {"start": v(7.32, -34.73) * mm, "end": v(7.22, -34.58) * mm});
            skLineSegment(sketch, "E1357", {"start": v(7.22, -34.58) * mm, "end": v(7.1, -34.42) * mm});
            skLineSegment(sketch, "E1358", {"start": v(7.1, -34.42) * mm, "end": v(6.9, -34.03) * mm});
            skLineSegment(sketch, "E1359", {"start": v(6.9, -34.03) * mm, "end": v(6.68, -33.6) * mm});
            skLineSegment(sketch, "E1360", {"start": v(6.68, -33.6) * mm, "end": v(6.46, -33.14) * mm});
            skLineSegment(sketch, "E1361", {"start": v(6.46, -33.14) * mm, "end": v(6.06, -32.2) * mm});
            skLineSegment(sketch, "E1362", {"start": v(6.06, -32.2) * mm, "end": v(5.72, -31.4) * mm});
            skLineSegment(sketch, "E1363", {"start": v(5.72, -31.4) * mm, "end": v(5.4, -30.63) * mm});
            skLineSegment(sketch, "E1364", {"start": v(5.4, -30.63) * mm, "end": v(5.09, -29.86) * mm});
            skLineSegment(sketch, "E1365", {"start": v(5.09, -29.86) * mm, "end": v(4.79, -29.07) * mm});
            skLineSegment(sketch, "E1366", {"start": v(4.79, -29.07) * mm, "end": v(4.5, -28.28) * mm});
            skLineSegment(sketch, "E1367", {"start": v(4.5, -28.28) * mm, "end": v(4.23, -27.48) * mm});
            skLineSegment(sketch, "E1368", {"start": v(4.23, -27.48) * mm, "end": v(3.97, -26.67) * mm});
            skLineSegment(sketch, "E1369", {"start": v(3.97, -26.67) * mm, "end": v(3.72, -25.85) * mm});
            skLineSegment(sketch, "E1370", {"start": v(3.72, -25.85) * mm, "end": v(3.49, -25.03) * mm});
            skLineSegment(sketch, "E1371", {"start": v(3.49, -25.03) * mm, "end": v(2.45, -28.68) * mm});
            skLineSegment(sketch, "E1372", {"start": v(2.45, -28.68) * mm, "end": v(2.31, -29.22) * mm});
            skLineSegment(sketch, "E1373", {"start": v(2.31, -29.22) * mm, "end": v(2.13, -29.84) * mm});
            skLineSegment(sketch, "E1374", {"start": v(2.13, -29.84) * mm, "end": v(2.04, -30.13) * mm});
            skLineSegment(sketch, "E1375", {"start": v(2.04, -30.13) * mm, "end": v(-1.1, -41.2) * mm});
            skLineSegment(sketch, "E1376", {"start": v(-1.1, -41.2) * mm, "end": v(-2.27, -45.37) * mm});
            skLineSegment(sketch, "E1377", {"start": v(-2.27, -45.37) * mm, "end": v(-3.47, -49.56) * mm});
            skLineSegment(sketch, "E1378", {"start": v(-27.52, 32.54) * mm, "end": v(-28.03, 32.14) * mm});
            skLineSegment(sketch, "E1379", {"start": v(-28.03, 32.14) * mm, "end": v(-28.54, 31.74) * mm});
            skLineSegment(sketch, "E1380", {"start": v(-28.54, 31.74) * mm, "end": v(-29.05, 31.33) * mm});
            skLineSegment(sketch, "E1381", {"start": v(-29.05, 31.33) * mm, "end": v(-29.55, 30.92) * mm});
            skLineSegment(sketch, "E1382", {"start": v(-29.55, 30.92) * mm, "end": v(-30.04, 30.5) * mm});
            skLineSegment(sketch, "E1383", {"start": v(-30.04, 30.5) * mm, "end": v(-30.52, 30.07) * mm});
            skLineSegment(sketch, "E1384", {"start": v(-30.52, 30.07) * mm, "end": v(-31, 29.63) * mm});
            skLineSegment(sketch, "E1385", {"start": v(-31, 29.63) * mm, "end": v(-31.48, 29.19) * mm});
            skLineSegment(sketch, "E1386", {"start": v(-31.48, 29.19) * mm, "end": v(-31.94, 28.74) * mm});
            skLineSegment(sketch, "E1387", {"start": v(-31.94, 28.74) * mm, "end": v(-32.4, 28.28) * mm});
            skLineSegment(sketch, "E1388", {"start": v(-32.4, 28.28) * mm, "end": v(-32.86, 27.82) * mm});
            skLineSegment(sketch, "E1389", {"start": v(-32.86, 27.82) * mm, "end": v(-33.3, 27.35) * mm});
            skLineSegment(sketch, "E1390", {"start": v(-33.3, 27.35) * mm, "end": v(-33.74, 26.87) * mm});
            skLineSegment(sketch, "E1391", {"start": v(-33.74, 26.87) * mm, "end": v(-34.18, 26.4) * mm});
            skLineSegment(sketch, "E1392", {"start": v(-34.18, 26.4) * mm, "end": v(-34.6, 25.9) * mm});
            skLineSegment(sketch, "E1393", {"start": v(-34.6, 25.9) * mm, "end": v(-35.03, 25.41) * mm});
            skLineSegment(sketch, "E1394", {"start": v(-35.03, 25.41) * mm, "end": v(-35.44, 24.91) * mm});
            skLineSegment(sketch, "E1395", {"start": v(-35.44, 24.91) * mm, "end": v(-35.85, 24.4) * mm});
            skLineSegment(sketch, "E1396", {"start": v(-35.85, 24.4) * mm, "end": v(-36.25, 23.9) * mm});
            skLineSegment(sketch, "E1397", {"start": v(-36.25, 23.9) * mm, "end": v(-36.64, 23.38) * mm});
            skLineSegment(sketch, "E1398", {"start": v(-36.64, 23.38) * mm, "end": v(-37.02, 22.86) * mm});
            skLineSegment(sketch, "E1399", {"start": v(-37.02, 22.86) * mm, "end": v(-37.4, 22.33) * mm});
            skLineSegment(sketch, "E1400", {"start": v(-37.4, 22.33) * mm, "end": v(-37.77, 21.8) * mm});
            skLineSegment(sketch, "E1401", {"start": v(-37.77, 21.8) * mm, "end": v(-38.14, 21.25) * mm});
            skLineSegment(sketch, "E1402", {"start": v(-38.14, 21.25) * mm, "end": v(-38.5, 20.7) * mm});
            skLineSegment(sketch, "E1403", {"start": v(-38.5, 20.7) * mm, "end": v(-38.84, 20.16) * mm});
            skLineSegment(sketch, "E1404", {"start": v(-38.84, 20.16) * mm, "end": v(-39.18, 19.6) * mm});
            skLineSegment(sketch, "E1405", {"start": v(-39.18, 19.6) * mm, "end": v(-39.51, 19.04) * mm});
            skLineSegment(sketch, "E1406", {"start": v(-39.51, 19.04) * mm, "end": v(-39.84, 18.48) * mm});
            skLineSegment(sketch, "E1407", {"start": v(-39.84, 18.48) * mm, "end": v(-40.15, 17.9) * mm});
            skLineSegment(sketch, "E1408", {"start": v(-40.15, 17.9) * mm, "end": v(-40.46, 17.33) * mm});
            skLineSegment(sketch, "E1409", {"start": v(-40.46, 17.33) * mm, "end": v(-40.77, 16.75) * mm});
            skLineSegment(sketch, "E1410", {"start": v(-40.77, 16.75) * mm, "end": v(-41.06, 16.16) * mm});
            skLineSegment(sketch, "E1411", {"start": v(-41.06, 16.16) * mm, "end": v(-41.34, 15.57) * mm});
            skLineSegment(sketch, "E1412", {"start": v(-41.34, 15.57) * mm, "end": v(-41.62, 14.98) * mm});
            skLineSegment(sketch, "E1413", {"start": v(-41.62, 14.98) * mm, "end": v(-41.89, 14.38) * mm});
            skLineSegment(sketch, "E1414", {"start": v(-41.89, 14.38) * mm, "end": v(-42.15, 13.78) * mm});
            skLineSegment(sketch, "E1415", {"start": v(-42.15, 13.78) * mm, "end": v(-42.4, 13.17) * mm});
            skLineSegment(sketch, "E1416", {"start": v(-42.4, 13.17) * mm, "end": v(-42.64, 12.55) * mm});
            skLineSegment(sketch, "E1417", {"start": v(-42.64, 12.55) * mm, "end": v(-42.88, 11.94) * mm});
            skLineSegment(sketch, "E1418", {"start": v(-42.88, 11.94) * mm, "end": v(-43.1, 11.32) * mm});
            skLineSegment(sketch, "E1419", {"start": v(-43.1, 11.32) * mm, "end": v(-43.32, 10.69) * mm});
            skLineSegment(sketch, "E1420", {"start": v(-43.32, 10.69) * mm, "end": v(-43.53, 10.06) * mm});
            skLineSegment(sketch, "E1421", {"start": v(-43.53, 10.06) * mm, "end": v(-43.73, 9.43) * mm});
            skLineSegment(sketch, "E1422", {"start": v(-43.73, 9.43) * mm, "end": v(-43.92, 8.79) * mm});
            skLineSegment(sketch, "E1423", {"start": v(-43.92, 8.79) * mm, "end": v(-44.1, 8.15) * mm});
            skLineSegment(sketch, "E1424", {"start": v(-44.1, 8.15) * mm, "end": v(-44.27, 7.5) * mm});
            skLineSegment(sketch, "E1425", {"start": v(-44.27, 7.5) * mm, "end": v(-44.43, 6.85) * mm});
            skLineSegment(sketch, "E1426", {"start": v(-44.43, 6.85) * mm, "end": v(-44.58, 6.2) * mm});
            skLineSegment(sketch, "E1427", {"start": v(-44.58, 6.2) * mm, "end": v(-44.73, 5.55) * mm});
            skLineSegment(sketch, "E1428", {"start": v(-44.73, 5.55) * mm, "end": v(-44.86, 4.89) * mm});
            skLineSegment(sketch, "E1429", {"start": v(-44.86, 4.89) * mm, "end": v(-44.99, 4.22) * mm});
            skLineSegment(sketch, "E1430", {"start": v(-44.99, 4.22) * mm, "end": v(-45.1, 3.56) * mm});
            skLineSegment(sketch, "E1431", {"start": v(-45.1, 3.56) * mm, "end": v(-45.2, 2.89) * mm});
            skLineSegment(sketch, "E1432", {"start": v(-45.2, 2.89) * mm, "end": v(-45.3, 2.22) * mm});
            skLineSegment(sketch, "E1433", {"start": v(-45.3, 2.22) * mm, "end": v(-45.4, 1.54) * mm});
            skLineSegment(sketch, "E1434", {"start": v(-45.4, 1.54) * mm, "end": v(-45.47, 0.86) * mm});
            skLineSegment(sketch, "E1435", {"start": v(-45.47, 0.86) * mm, "end": v(-45.53, 0.18) * mm});
            skLineSegment(sketch, "E1436", {"start": v(-45.53, 0.18) * mm, "end": v(-45.6, -0.5) * mm});
            skLineSegment(sketch, "E1437", {"start": v(-45.6, -0.5) * mm, "end": v(-45.64, -1.2) * mm});
            skLineSegment(sketch, "E1438", {"start": v(-45.64, -1.2) * mm, "end": v(-45.67, -1.88) * mm});
            skLineSegment(sketch, "E1439", {"start": v(-45.67, -1.88) * mm, "end": v(-45.7, -2.58) * mm});
            skLineSegment(sketch, "E1440", {"start": v(-45.7, -2.58) * mm, "end": v(-45.71, -3.27) * mm});
            skLineSegment(sketch, "E1441", {"start": v(-45.71, -3.27) * mm, "end": v(-45.72, -3.97) * mm});
            skLineSegment(sketch, "E1442", {"start": v(-45.72, -3.97) * mm, "end": v(-45.71, -4.85) * mm});
            skLineSegment(sketch, "E1443", {"start": v(-45.71, -4.85) * mm, "end": v(-45.69, -5.72) * mm});
            skLineSegment(sketch, "E1444", {"start": v(-45.69, -5.72) * mm, "end": v(-45.65, -6.59) * mm});
            skLineSegment(sketch, "E1445", {"start": v(-45.65, -6.59) * mm, "end": v(-45.59, -7.45) * mm});
            skLineSegment(sketch, "E1446", {"start": v(-45.59, -7.45) * mm, "end": v(-45.52, -8.3) * mm});
            skLineSegment(sketch, "E1447", {"start": v(-45.52, -8.3) * mm, "end": v(-45.43, -9.16) * mm});
            skLineSegment(sketch, "E1448", {"start": v(-45.43, -9.16) * mm, "end": v(-45.32, -10.01) * mm});
            skLineSegment(sketch, "E1449", {"start": v(-45.32, -10.01) * mm, "end": v(-45.2, -10.86) * mm});
            skLineSegment(sketch, "E1450", {"start": v(-45.2, -10.86) * mm, "end": v(-45.07, -11.7) * mm});
            skLineSegment(sketch, "E1451", {"start": v(-45.07, -11.7) * mm, "end": v(-44.92, -12.53) * mm});
            skLineSegment(sketch, "E1452", {"start": v(-44.92, -12.53) * mm, "end": v(-44.76, -13.36) * mm});
            skLineSegment(sketch, "E1453", {"start": v(-44.76, -13.36) * mm, "end": v(-44.58, -14.18) * mm});
            skLineSegment(sketch, "E1454", {"start": v(-44.58, -14.18) * mm, "end": v(-44.38, -15) * mm});
            skLineSegment(sketch, "E1455", {"start": v(-44.38, -15) * mm, "end": v(-44.17, -15.81) * mm});
            skLineSegment(sketch, "E1456", {"start": v(-44.17, -15.81) * mm, "end": v(-43.95, -16.62) * mm});
            skLineSegment(sketch, "E1457", {"start": v(-43.95, -16.62) * mm, "end": v(-43.7, -17.42) * mm});
            skLineSegment(sketch, "E1458", {"start": v(-43.7, -17.42) * mm, "end": v(-43.46, -18.21) * mm});
            skLineSegment(sketch, "E1459", {"start": v(-43.46, -18.21) * mm, "end": v(-43.2, -19) * mm});
            skLineSegment(sketch, "E1460", {"start": v(-43.2, -19) * mm, "end": v(-42.91, -19.78) * mm});
            skLineSegment(sketch, "E1461", {"start": v(-42.91, -19.78) * mm, "end": v(-42.62, -20.56) * mm});
            skLineSegment(sketch, "E1462", {"start": v(-42.62, -20.56) * mm, "end": v(-42.31, -21.32) * mm});
            skLineSegment(sketch, "E1463", {"start": v(-42.31, -21.32) * mm, "end": v(-42, -22.09) * mm});
            skLineSegment(sketch, "E1464", {"start": v(-42, -22.09) * mm, "end": v(-41.66, -22.84) * mm});
            skLineSegment(sketch, "E1465", {"start": v(-41.66, -22.84) * mm, "end": v(-41.3, -23.59) * mm});
            skLineSegment(sketch, "E1466", {"start": v(-41.3, -23.59) * mm, "end": v(-40.95, -24.32) * mm});
            skLineSegment(sketch, "E1467", {"start": v(-40.95, -24.32) * mm, "end": v(-40.58, -25.06) * mm});
            skLineSegment(sketch, "E1468", {"start": v(-40.58, -25.06) * mm, "end": v(-40.2, -25.78) * mm});
            skLineSegment(sketch, "E1469", {"start": v(-40.2, -25.78) * mm, "end": v(-39.8, -26.5) * mm});
            skLineSegment(sketch, "E1470", {"start": v(-39.8, -26.5) * mm, "end": v(-39.38, -27.2) * mm});
            skLineSegment(sketch, "E1471", {"start": v(-39.38, -27.2) * mm, "end": v(-38.96, -27.9) * mm});
            skLineSegment(sketch, "E1472", {"start": v(-38.96, -27.9) * mm, "end": v(-38.53, -28.6) * mm});
            skLineSegment(sketch, "E1473", {"start": v(-38.53, -28.6) * mm, "end": v(-38.08, -29.28) * mm});
            skLineSegment(sketch, "E1474", {"start": v(-38.08, -29.28) * mm, "end": v(-37.62, -29.96) * mm});
            skLineSegment(sketch, "E1475", {"start": v(-37.62, -29.96) * mm, "end": v(-37.15, -30.62) * mm});
            skLineSegment(sketch, "E1476", {"start": v(-37.15, -30.62) * mm, "end": v(-36.67, -31.28) * mm});
            skLineSegment(sketch, "E1477", {"start": v(-36.67, -31.28) * mm, "end": v(-36.18, -31.93) * mm});
            skLineSegment(sketch, "E1478", {"start": v(-36.18, -31.93) * mm, "end": v(-35.67, -32.57) * mm});
            skLineSegment(sketch, "E1479", {"start": v(-35.67, -32.57) * mm, "end": v(-35.16, -33.2) * mm});
            skLineSegment(sketch, "E1480", {"start": v(-35.16, -33.2) * mm, "end": v(-34.63, -33.82) * mm});
            skLineSegment(sketch, "E1481", {"start": v(-34.63, -33.82) * mm, "end": v(-34.1, -34.43) * mm});
            skLineSegment(sketch, "E1482", {"start": v(-34.1, -34.43) * mm, "end": v(-33.55, -35.03) * mm});
            skLineSegment(sketch, "E1483", {"start": v(-33.55, -35.03) * mm, "end": v(-32.99, -35.62) * mm});
            skLineSegment(sketch, "E1484", {"start": v(-32.99, -35.62) * mm, "end": v(-32.42, -36.2) * mm});
            skLineSegment(sketch, "E1485", {"start": v(-32.42, -36.2) * mm, "end": v(-31.84, -36.78) * mm});
            skLineSegment(sketch, "E1486", {"start": v(-31.84, -36.78) * mm, "end": v(-31.25, -37.34) * mm});
            skLineSegment(sketch, "E1487", {"start": v(-31.25, -37.34) * mm, "end": v(-30.65, -37.89) * mm});
            skLineSegment(sketch, "E1488", {"start": v(-30.65, -37.89) * mm, "end": v(-30.05, -38.43) * mm});
            skLineSegment(sketch, "E1489", {"start": v(-30.05, -38.43) * mm, "end": v(-29.43, -38.96) * mm});
            skLineSegment(sketch, "E1490", {"start": v(-29.43, -38.96) * mm, "end": v(-28.8, -39.48) * mm});
            skLineSegment(sketch, "E1491", {"start": v(-28.8, -39.48) * mm, "end": v(-28.16, -39.99) * mm});
            skLineSegment(sketch, "E1492", {"start": v(-28.16, -39.99) * mm, "end": v(-27.52, -40.48) * mm});
            skLineSegment(sketch, "E1493", {"start": v(-27.52, -40.48) * mm, "end": v(-26.86, -40.97) * mm});
            skLineSegment(sketch, "E1494", {"start": v(-26.86, -40.97) * mm, "end": v(-26.2, -41.44) * mm});
            skLineSegment(sketch, "E1495", {"start": v(-26.2, -41.44) * mm, "end": v(-25.53, -41.9) * mm});
            skLineSegment(sketch, "E1496", {"start": v(-25.53, -41.9) * mm, "end": v(-24.85, -42.35) * mm});
            skLineSegment(sketch, "E1497", {"start": v(-24.85, -42.35) * mm, "end": v(-24.16, -42.8) * mm});
            skLineSegment(sketch, "E1498", {"start": v(-24.16, -42.8) * mm, "end": v(-23.46, -43.22) * mm});
            skLineSegment(sketch, "E1499", {"start": v(-23.46, -43.22) * mm, "end": v(-22.75, -43.63) * mm});
            skLineSegment(sketch, "E1500", {"start": v(-22.75, -43.63) * mm, "end": v(-22.04, -44.03) * mm});
            skLineSegment(sketch, "E1501", {"start": v(-22.04, -44.03) * mm, "end": v(-21.32, -44.42) * mm});
            skLineSegment(sketch, "E1502", {"start": v(-21.32, -44.42) * mm, "end": v(-20.59, -44.8) * mm});
            skLineSegment(sketch, "E1503", {"start": v(-20.59, -44.8) * mm, "end": v(-19.85, -45.17) * mm});
            skLineSegment(sketch, "E1504", {"start": v(-19.85, -45.17) * mm, "end": v(-19.1, -45.52) * mm});
            skLineSegment(sketch, "E1505", {"start": v(-19.1, -45.52) * mm, "end": v(-18.36, -45.85) * mm});
            skLineSegment(sketch, "E1506", {"start": v(-18.36, -45.85) * mm, "end": v(-17.6, -43.03) * mm});
            skLineSegment(sketch, "E1507", {"start": v(-17.6, -43.03) * mm, "end": v(-16.85, -40.2) * mm});
            skLineSegment(sketch, "E1508", {"start": v(-16.85, -40.2) * mm, "end": v(-15.38, -34.84) * mm});
            skLineSegment(sketch, "E1509", {"start": v(-15.38, -34.84) * mm, "end": v(-14.13, -30.33) * mm});
            skLineSegment(sketch, "E1510", {"start": v(-14.13, -30.33) * mm, "end": v(-13.27, -27.26) * mm});
            skLineSegment(sketch, "E1511", {"start": v(-13.27, -27.26) * mm, "end": v(-13.1, -26.65) * mm});
            skLineSegment(sketch, "E1512", {"start": v(-13.1, -26.65) * mm, "end": v(-13.01, -26.34) * mm});
            skLineSegment(sketch, "E1513", {"start": v(-13.01, -26.34) * mm, "end": v(-12.92, -26.04) * mm});
            skLineSegment(sketch, "E1514", {"start": v(-12.92, -26.04) * mm, "end": v(-11.99, -22.76) * mm});
            skLineSegment(sketch, "E1515", {"start": v(-11.99, -22.76) * mm, "end": v(-12.47, -23.17) * mm});
            skLineSegment(sketch, "E1516", {"start": v(-12.47, -23.17) * mm, "end": v(-12.96, -23.57) * mm});
            skLineSegment(sketch, "E1517", {"start": v(-12.96, -23.57) * mm, "end": v(-13.45, -23.96) * mm});
            skLineSegment(sketch, "E1518", {"start": v(-13.45, -23.96) * mm, "end": v(-13.95, -24.34) * mm});
            skLineSegment(sketch, "E1519", {"start": v(-13.95, -24.34) * mm, "end": v(-14.45, -24.72) * mm});
            skLineSegment(sketch, "E1520", {"start": v(-14.45, -24.72) * mm, "end": v(-14.95, -25.09) * mm});
            skLineSegment(sketch, "E1521", {"start": v(-14.95, -25.09) * mm, "end": v(-15.46, -25.45) * mm});
            skLineSegment(sketch, "E1522", {"start": v(-15.46, -25.45) * mm, "end": v(-15.97, -25.8) * mm});
            skLineSegment(sketch, "E1523", {"start": v(-15.97, -25.8) * mm, "end": v(-18.82, -27.59) * mm});
            skLineSegment(sketch, "E1524", {"start": v(-18.82, -27.59) * mm, "end": v(-18.83, -27.14) * mm});
            skLineSegment(sketch, "E1525", {"start": v(-18.83, -27.14) * mm, "end": v(-18.83, -26.69) * mm});
            skLineSegment(sketch, "E1526", {"start": v(-18.83, -26.69) * mm, "end": v(-18.8, -25.77) * mm});
            skLineSegment(sketch, "E1527", {"start": v(-18.8, -25.77) * mm, "end": v(-18.74, -24.83) * mm});
            skLineSegment(sketch, "E1528", {"start": v(-18.74, -24.83) * mm, "end": v(-18.68, -23.88) * mm});
            skLineSegment(sketch, "E1529", {"start": v(-18.68, -23.88) * mm, "end": v(-18.6, -22.93) * mm});
            skLineSegment(sketch, "E1530", {"start": v(-18.6, -22.93) * mm, "end": v(-18.56, -21.98) * mm});
            skLineSegment(sketch, "E1531", {"start": v(-18.56, -21.98) * mm, "end": v(-18.54, -21.51) * mm});
            skLineSegment(sketch, "E1532", {"start": v(-18.54, -21.51) * mm, "end": v(-18.53, -21.04) * mm});
            skLineSegment(sketch, "E1533", {"start": v(-18.53, -21.04) * mm, "end": v(-18.53, -20.58) * mm});
            skLineSegment(sketch, "E1534", {"start": v(-18.53, -20.58) * mm, "end": v(-18.54, -20.12) * mm});
            skLineSegment(sketch, "E1535", {"start": v(-18.54, -20.12) * mm, "end": v(-19.92, -19.83) * mm});
            skLineSegment(sketch, "E1536", {"start": v(-19.92, -19.83) * mm, "end": v(-20.95, -19.63) * mm});
            skLineSegment(sketch, "E1537", {"start": v(-20.95, -19.63) * mm, "end": v(-21.74, -19.47) * mm});
            skLineSegment(sketch, "E1538", {"start": v(-21.74, -19.47) * mm, "end": v(-22.4, -19.32) * mm});
            skLineSegment(sketch, "E1539", {"start": v(-22.4, -19.32) * mm, "end": v(-23.04, -19.16) * mm});
            skLineSegment(sketch, "E1540", {"start": v(-23.04, -19.16) * mm, "end": v(-23.76, -18.94) * mm});
            skLineSegment(sketch, "E1541", {"start": v(-23.76, -18.94) * mm, "end": v(-24.67, -18.62) * mm});
            skLineSegment(sketch, "E1542", {"start": v(-24.67, -18.62) * mm, "end": v(-25.88, -18.2) * mm});
            skLineSegment(sketch, "E1543", {"start": v(-25.88, -18.2) * mm, "end": v(-25.84, -18.11) * mm});
            skLineSegment(sketch, "E1544", {"start": v(-25.84, -18.11) * mm, "end": v(-25.79, -18.04) * mm});
            skLineSegment(sketch, "E1545", {"start": v(-25.79, -18.04) * mm, "end": v(-25.72, -17.96) * mm});
            skLineSegment(sketch, "E1546", {"start": v(-25.72, -17.96) * mm, "end": v(-25.63, -17.88) * mm});
            skLineSegment(sketch, "E1547", {"start": v(-25.63, -17.88) * mm, "end": v(-25.42, -17.73) * mm});
            skLineSegment(sketch, "E1548", {"start": v(-25.42, -17.73) * mm, "end": v(-25.17, -17.58) * mm});
            skLineSegment(sketch, "E1549", {"start": v(-25.17, -17.58) * mm, "end": v(-24.67, -17.32) * mm});
            skLineSegment(sketch, "E1550", {"start": v(-24.67, -17.32) * mm, "end": v(-24.27, -17.14) * mm});
            skLineSegment(sketch, "E1551", {"start": v(-24.27, -17.14) * mm, "end": v(-23.1, -16.55) * mm});
            skLineSegment(sketch, "E1552", {"start": v(-23.1, -16.55) * mm, "end": v(-22.16, -16.06) * mm});
            skLineSegment(sketch, "E1553", {"start": v(-22.16, -16.06) * mm, "end": v(-21.4, -15.64) * mm});
            skLineSegment(sketch, "E1554", {"start": v(-21.4, -15.64) * mm, "end": v(-20.72, -15.24) * mm});
            skLineSegment(sketch, "E1555", {"start": v(-20.72, -15.24) * mm, "end": v(-20.07, -14.83) * mm});
            skLineSegment(sketch, "E1556", {"start": v(-20.07, -14.83) * mm, "end": v(-19.37, -14.37) * mm});
            skLineSegment(sketch, "E1557", {"start": v(-19.37, -14.37) * mm, "end": v(-18.53, -13.83) * mm});
            skLineSegment(sketch, "E1558", {"start": v(-18.53, -13.83) * mm, "end": v(-17.48, -13.16) * mm});
            skLineSegment(sketch, "E1559", {"start": v(-17.48, -13.16) * mm, "end": v(-12.73, -9.56) * mm});
            skLineSegment(sketch, "E1560", {"start": v(-12.73, -9.56) * mm, "end": v(-12, -8.96) * mm});
            skLineSegment(sketch, "E1561", {"start": v(-12, -8.96) * mm, "end": v(-11.4, -8.43) * mm});
            skLineSegment(sketch, "E1562", {"start": v(-11.4, -8.43) * mm, "end": v(-10.88, -7.96) * mm});
            skLineSegment(sketch, "E1563", {"start": v(-10.88, -7.96) * mm, "end": v(-10.44, -7.55) * mm});
            skLineSegment(sketch, "E1564", {"start": v(-10.44, -7.55) * mm, "end": v(-9.74, -6.88) * mm});
            skLineSegment(sketch, "E1565", {"start": v(-9.74, -6.88) * mm, "end": v(-9.45, -6.61) * mm});
            skLineSegment(sketch, "E1566", {"start": v(-9.45, -6.61) * mm, "end": v(-9.19, -6.38) * mm});
            skLineSegment(sketch, "E1567", {"start": v(-9.19, -6.38) * mm, "end": v(-9.19, -6.38) * mm});
            skLineSegment(sketch, "E1568", {"start": v(-9.19, -6.38) * mm, "end": v(-9.18, -6.37) * mm});
            skLineSegment(sketch, "E1569", {"start": v(-9.18, -6.37) * mm, "end": v(-8.98, -6.2) * mm});
            skLineSegment(sketch, "E1570", {"start": v(-8.98, -6.2) * mm, "end": v(-6.8, -4.46) * mm});
            skLineSegment(sketch, "E1571", {"start": v(-6.8, -4.46) * mm, "end": v(-6.63, -3.84) * mm});
            skLineSegment(sketch, "E1572", {"start": v(-6.63, -3.84) * mm, "end": v(-7.33, -4.02) * mm});
            skLineSegment(sketch, "E1573", {"start": v(-7.33, -4.02) * mm, "end": v(-8.04, -4.2) * mm});
            skLineSegment(sketch, "E1574", {"start": v(-8.04, -4.2) * mm, "end": v(-8.77, -4.36) * mm});
            skLineSegment(sketch, "E1575", {"start": v(-8.77, -4.36) * mm, "end": v(-9.5, -4.5) * mm});
            skLineSegment(sketch, "E1576", {"start": v(-9.5, -4.5) * mm, "end": v(-10.25, -4.62) * mm});
            skLineSegment(sketch, "E1577", {"start": v(-10.25, -4.62) * mm, "end": v(-11.01, -4.73) * mm});
            skLineSegment(sketch, "E1578", {"start": v(-11.01, -4.73) * mm, "end": v(-11.78, -4.81) * mm});
            skLineSegment(sketch, "E1579", {"start": v(-11.78, -4.81) * mm, "end": v(-12.56, -4.88) * mm});
            skLineSegment(sketch, "E1580", {"start": v(-12.56, -4.88) * mm, "end": v(-13.35, -4.92) * mm});
            skLineSegment(sketch, "E1581", {"start": v(-13.35, -4.92) * mm, "end": v(-14.15, -4.93) * mm});
            skLineSegment(sketch, "E1582", {"start": v(-14.15, -4.93) * mm, "end": v(-14.95, -4.92) * mm});
            skLineSegment(sketch, "E1583", {"start": v(-14.95, -4.92) * mm, "end": v(-15.76, -4.88) * mm});
            skLineSegment(sketch, "E1584", {"start": v(-15.76, -4.88) * mm, "end": v(-16.58, -4.82) * mm});
            skLineSegment(sketch, "E1585", {"start": v(-16.58, -4.82) * mm, "end": v(-16.99, -4.77) * mm});
            skLineSegment(sketch, "E1586", {"start": v(-16.99, -4.77) * mm, "end": v(-17.4, -4.72) * mm});
            skLineSegment(sketch, "E1587", {"start": v(-17.4, -4.72) * mm, "end": v(-17.8, -4.66) * mm});
            skLineSegment(sketch, "E1588", {"start": v(-17.8, -4.66) * mm, "end": v(-18.22, -4.6) * mm});
            skLineSegment(sketch, "E1589", {"start": v(-18.22, -4.6) * mm, "end": v(-18.64, -4.52) * mm});
            skLineSegment(sketch, "E1590", {"start": v(-18.64, -4.52) * mm, "end": v(-19.05, -4.43) * mm});
            skLineSegment(sketch, "E1591", {"start": v(-19.05, -4.43) * mm, "end": v(-19.56, -4.31) * mm});
            skLineSegment(sketch, "E1592", {"start": v(-19.56, -4.31) * mm, "end": v(-20.04, -4.18) * mm});
            skLineSegment(sketch, "E1593", {"start": v(-20.04, -4.18) * mm, "end": v(-20.49, -4.05) * mm});
            skLineSegment(sketch, "E1594", {"start": v(-20.49, -4.05) * mm, "end": v(-20.92, -3.9) * mm});
            skLineSegment(sketch, "E1595", {"start": v(-20.92, -3.9) * mm, "end": v(-21.32, -3.74) * mm});
            skLineSegment(sketch, "E1596", {"start": v(-21.32, -3.74) * mm, "end": v(-21.7, -3.58) * mm});
            skLineSegment(sketch, "E1597", {"start": v(-21.7, -3.58) * mm, "end": v(-22.05, -3.4) * mm});
            skLineSegment(sketch, "E1598", {"start": v(-22.05, -3.4) * mm, "end": v(-22.38, -3.22) * mm});
            skLineSegment(sketch, "E1599", {"start": v(-22.38, -3.22) * mm, "end": v(-22.68, -3.02) * mm});
            skLineSegment(sketch, "E1600", {"start": v(-22.68, -3.02) * mm, "end": v(-22.96, -2.82) * mm});
            skLineSegment(sketch, "E1601", {"start": v(-22.96, -2.82) * mm, "end": v(-23.22, -2.62) * mm});
            skLineSegment(sketch, "E1602", {"start": v(-23.22, -2.62) * mm, "end": v(-23.46, -2.4) * mm});
            skLineSegment(sketch, "E1603", {"start": v(-23.46, -2.4) * mm, "end": v(-23.68, -2.18) * mm});
            skLineSegment(sketch, "E1604", {"start": v(-23.68, -2.18) * mm, "end": v(-23.88, -1.95) * mm});
            skLineSegment(sketch, "E1605", {"start": v(-23.88, -1.95) * mm, "end": v(-24.06, -1.71) * mm});
            skLineSegment(sketch, "E1606", {"start": v(-24.06, -1.71) * mm, "end": v(-24.22, -1.47) * mm});
            skLineSegment(sketch, "E1607", {"start": v(-24.22, -1.47) * mm, "end": v(-24.36, -1.22) * mm});
            skLineSegment(sketch, "E1608", {"start": v(-24.36, -1.22) * mm, "end": v(-24.48, -0.96) * mm});
            skLineSegment(sketch, "E1609", {"start": v(-24.48, -0.96) * mm, "end": v(-24.59, -0.7) * mm});
            skLineSegment(sketch, "E1610", {"start": v(-24.59, -0.7) * mm, "end": v(-24.68, -0.44) * mm});
            skLineSegment(sketch, "E1611", {"start": v(-24.68, -0.44) * mm, "end": v(-24.75, -0.17) * mm});
            skLineSegment(sketch, "E1612", {"start": v(-24.75, -0.17) * mm, "end": v(-24.8, 0.1) * mm});
            skLineSegment(sketch, "E1613", {"start": v(-24.8, 0.1) * mm, "end": v(-24.85, 0.39) * mm});
            skLineSegment(sketch, "E1614", {"start": v(-24.85, 0.39) * mm, "end": v(-24.88, 0.67) * mm});
            skLineSegment(sketch, "E1615", {"start": v(-24.88, 0.67) * mm, "end": v(-24.9, 0.96) * mm});
            skLineSegment(sketch, "E1616", {"start": v(-24.9, 0.96) * mm, "end": v(-24.9, 1.25) * mm});
            skLineSegment(sketch, "E1617", {"start": v(-24.9, 1.25) * mm, "end": v(-24.89, 1.55) * mm});
            skLineSegment(sketch, "E1618", {"start": v(-24.89, 1.55) * mm, "end": v(-24.86, 1.84) * mm});
            skLineSegment(sketch, "E1619", {"start": v(-24.86, 1.84) * mm, "end": v(-24.83, 2.15) * mm});
            skLineSegment(sketch, "E1620", {"start": v(-24.83, 2.15) * mm, "end": v(-24.78, 2.45) * mm});
            skLineSegment(sketch, "E1621", {"start": v(-24.78, 2.45) * mm, "end": v(-24.73, 2.75) * mm});
            skLineSegment(sketch, "E1622", {"start": v(-24.73, 2.75) * mm, "end": v(-24.66, 3.06) * mm});
            skLineSegment(sketch, "E1623", {"start": v(-24.66, 3.06) * mm, "end": v(-24.59, 3.37) * mm});
            skLineSegment(sketch, "E1624", {"start": v(-24.59, 3.37) * mm, "end": v(-24.5, 3.68) * mm});
            skLineSegment(sketch, "E1625", {"start": v(-24.5, 3.68) * mm, "end": v(-24.32, 4.3) * mm});
            skLineSegment(sketch, "E1626", {"start": v(-24.32, 4.3) * mm, "end": v(-24.1, 4.93) * mm});
            skLineSegment(sketch, "E1627", {"start": v(-24.1, 4.93) * mm, "end": v(-23.87, 5.56) * mm});
            skLineSegment(sketch, "E1628", {"start": v(-23.87, 5.56) * mm, "end": v(-23.62, 6.19) * mm});
            skLineSegment(sketch, "E1629", {"start": v(-23.62, 6.19) * mm, "end": v(-23.35, 6.8) * mm});
            skLineSegment(sketch, "E1630", {"start": v(-23.35, 6.8) * mm, "end": v(-22.8, 8.03) * mm});
            skLineSegment(sketch, "E1631", {"start": v(-22.8, 8.03) * mm, "end": v(-22.26, 9.2) * mm});
            skLineSegment(sketch, "E1632", {"start": v(-22.26, 9.2) * mm, "end": v(-22, 9.77) * mm});
            skLineSegment(sketch, "E1633", {"start": v(-22, 9.77) * mm, "end": v(-21.76, 10.32) * mm});
            skLineSegment(sketch, "E1634", {"start": v(-21.76, 10.32) * mm, "end": v(-21.54, 10.85) * mm});
            skLineSegment(sketch, "E1635", {"start": v(-21.54, 10.85) * mm, "end": v(-21.34, 11.36) * mm});
            skLineSegment(sketch, "E1636", {"start": v(-21.34, 11.36) * mm, "end": v(-21.18, 11.84) * mm});
            skLineSegment(sketch, "E1637", {"start": v(-21.18, 11.84) * mm, "end": v(-21.05, 12.3) * mm});
            skLineSegment(sketch, "E1638", {"start": v(-21.05, 12.3) * mm, "end": v(-20.9, 12.93) * mm});
            skLineSegment(sketch, "E1639", {"start": v(-20.9, 12.93) * mm, "end": v(-20.77, 13.6) * mm});
            skLineSegment(sketch, "E1640", {"start": v(-20.77, 13.6) * mm, "end": v(-20.54, 15.02) * mm});
            skLineSegment(sketch, "E1641", {"start": v(-20.54, 15.02) * mm, "end": v(-20.43, 15.74) * mm});
            skLineSegment(sketch, "E1642", {"start": v(-20.43, 15.74) * mm, "end": v(-20.3, 16.45) * mm});
            skLineSegment(sketch, "E1643", {"start": v(-20.3, 16.45) * mm, "end": v(-20.17, 17.16) * mm});
            skLineSegment(sketch, "E1644", {"start": v(-20.17, 17.16) * mm, "end": v(-20.02, 17.84) * mm});
            skLineSegment(sketch, "E1645", {"start": v(-20.02, 17.84) * mm, "end": v(-19.93, 18.17) * mm});
            skLineSegment(sketch, "E1646", {"start": v(-19.93, 18.17) * mm, "end": v(-19.83, 18.5) * mm});
            skLineSegment(sketch, "E1647", {"start": v(-19.83, 18.5) * mm, "end": v(-19.73, 18.8) * mm});
            skLineSegment(sketch, "E1648", {"start": v(-19.73, 18.8) * mm, "end": v(-19.61, 19.11) * mm});
            skLineSegment(sketch, "E1649", {"start": v(-19.61, 19.11) * mm, "end": v(-19.5, 19.4) * mm});
            skLineSegment(sketch, "E1650", {"start": v(-19.5, 19.4) * mm, "end": v(-19.36, 19.68) * mm});
            skLineSegment(sketch, "E1651", {"start": v(-19.36, 19.68) * mm, "end": v(-19.21, 19.95) * mm});
            skLineSegment(sketch, "E1652", {"start": v(-19.21, 19.95) * mm, "end": v(-19.06, 20.2) * mm});
            skLineSegment(sketch, "E1653", {"start": v(-19.06, 20.2) * mm, "end": v(-18.88, 20.43) * mm});
            skLineSegment(sketch, "E1654", {"start": v(-18.88, 20.43) * mm, "end": v(-18.7, 20.64) * mm});
            skLineSegment(sketch, "E1655", {"start": v(-18.7, 20.64) * mm, "end": v(-18.5, 20.84) * mm});
            skLineSegment(sketch, "E1656", {"start": v(-18.5, 20.84) * mm, "end": v(-18.29, 21.01) * mm});
            skLineSegment(sketch, "E1657", {"start": v(-18.29, 21.01) * mm, "end": v(-18.06, 21.17) * mm});
            skLineSegment(sketch, "E1658", {"start": v(-18.06, 21.17) * mm, "end": v(-17.8, 21.3) * mm});
            skLineSegment(sketch, "E1659", {"start": v(-17.8, 21.3) * mm, "end": v(-17.54, 21.41) * mm});
            skLineSegment(sketch, "E1660", {"start": v(-17.54, 21.41) * mm, "end": v(-17.26, 21.5) * mm});
            skLineSegment(sketch, "E1661", {"start": v(-17.26, 21.5) * mm, "end": v(-17, 21.55) * mm});
            skLineSegment(sketch, "E1662", {"start": v(-17, 21.55) * mm, "end": v(-16.73, 21.59) * mm});
            skLineSegment(sketch, "E1663", {"start": v(-16.73, 21.59) * mm, "end": v(-16.45, 21.6) * mm});
            skLineSegment(sketch, "E1664", {"start": v(-16.45, 21.6) * mm, "end": v(-16.16, 21.6) * mm});
            skLineSegment(sketch, "E1665", {"start": v(-16.16, 21.6) * mm, "end": v(-15.87, 21.6) * mm});
            skLineSegment(sketch, "E1666", {"start": v(-15.87, 21.6) * mm, "end": v(-15.57, 21.56) * mm});
            skLineSegment(sketch, "E1667", {"start": v(-15.57, 21.56) * mm, "end": v(-15.26, 21.52) * mm});
            skLineSegment(sketch, "E1668", {"start": v(-15.26, 21.52) * mm, "end": v(-14.95, 21.46) * mm});
            skLineSegment(sketch, "E1669", {"start": v(-14.95, 21.46) * mm, "end": v(-14.63, 21.38) * mm});
            skLineSegment(sketch, "E1670", {"start": v(-14.63, 21.38) * mm, "end": v(-14.3, 21.3) * mm});
            skLineSegment(sketch, "E1671", {"start": v(-14.3, 21.3) * mm, "end": v(-13.98, 21.2) * mm});
            skLineSegment(sketch, "E1672", {"start": v(-13.98, 21.2) * mm, "end": v(-13.65, 21.1) * mm});
            skLineSegment(sketch, "E1673", {"start": v(-13.65, 21.1) * mm, "end": v(-13.33, 20.98) * mm});
            skLineSegment(sketch, "E1674", {"start": v(-13.33, 20.98) * mm, "end": v(-13, 20.85) * mm});
            skLineSegment(sketch, "E1675", {"start": v(-13, 20.85) * mm, "end": v(-12.34, 20.58) * mm});
            skLineSegment(sketch, "E1676", {"start": v(-12.34, 20.58) * mm, "end": v(-11.7, 20.28) * mm});
            skLineSegment(sketch, "E1677", {"start": v(-11.7, 20.28) * mm, "end": v(-11.06, 19.96) * mm});
            skLineSegment(sketch, "E1678", {"start": v(-11.06, 19.96) * mm, "end": v(-10.44, 19.63) * mm});
            skLineSegment(sketch, "E1679", {"start": v(-10.44, 19.63) * mm, "end": v(-9.86, 19.29) * mm});
            skLineSegment(sketch, "E1680", {"start": v(-9.86, 19.29) * mm, "end": v(-9.3, 18.94) * mm});
            skLineSegment(sketch, "E1681", {"start": v(-9.3, 18.94) * mm, "end": v(-8.79, 18.61) * mm});
            skLineSegment(sketch, "E1682", {"start": v(-8.79, 18.61) * mm, "end": v(-8.32, 18.29) * mm});
            skLineSegment(sketch, "E1683", {"start": v(-8.32, 18.29) * mm, "end": v(-7.9, 17.99) * mm});
            skLineSegment(sketch, "E1684", {"start": v(-7.9, 17.99) * mm, "end": v(-7.5, 17.67) * mm});
            skLineSegment(sketch, "E1685", {"start": v(-7.5, 17.67) * mm, "end": v(-7.1, 17.36) * mm});
            skLineSegment(sketch, "E1686", {"start": v(-7.1, 17.36) * mm, "end": v(-6.7, 17.04) * mm});
            skLineSegment(sketch, "E1687", {"start": v(-6.7, 17.04) * mm, "end": v(-6.33, 16.72) * mm});
            skLineSegment(sketch, "E1688", {"start": v(-6.33, 16.72) * mm, "end": v(-5.96, 16.4) * mm});
            skLineSegment(sketch, "E1689", {"start": v(-5.96, 16.4) * mm, "end": v(-5.6, 16.08) * mm});
            skLineSegment(sketch, "E1690", {"start": v(-5.6, 16.08) * mm, "end": v(-4.92, 15.42) * mm});
            skLineSegment(sketch, "E1691", {"start": v(-4.92, 15.42) * mm, "end": v(-4.26, 14.76) * mm});
            skLineSegment(sketch, "E1692", {"start": v(-4.26, 14.76) * mm, "end": v(-3.63, 14.09) * mm});
            skLineSegment(sketch, "E1693", {"start": v(-3.63, 14.09) * mm, "end": v(-3.03, 13.4) * mm});
            skLineSegment(sketch, "E1694", {"start": v(-3.03, 13.4) * mm, "end": v(-2.44, 12.72) * mm});
            skLineSegment(sketch, "E1695", {"start": v(-2.44, 12.72) * mm, "end": v(-1.07, 17.55) * mm});
            skLineSegment(sketch, "E1696", {"start": v(-1.07, 17.55) * mm, "end": v(-0.4, 20.12) * mm});
            skLineSegment(sketch, "E1697", {"start": v(-0.4, 20.12) * mm, "end": v(-0.04, 21.49) * mm});
            skLineSegment(sketch, "E1698", {"start": v(-0.04, 21.49) * mm, "end": v(0.32, 22.9) * mm});
            skLineSegment(sketch, "E1699", {"start": v(0.32, 22.9) * mm, "end": v(0.66, 24.32) * mm});
            skLineSegment(sketch, "E1700", {"start": v(0.66, 24.32) * mm, "end": v(0.99, 25.76) * mm});
            skLineSegment(sketch, "E1701", {"start": v(0.99, 25.76) * mm, "end": v(1.3, 27.2) * mm});
            skLineSegment(sketch, "E1702", {"start": v(1.3, 27.2) * mm, "end": v(1.57, 28.61) * mm});
            skLineSegment(sketch, "E1703", {"start": v(1.57, 28.61) * mm, "end": v(1.7, 29.31) * mm});
            skLineSegment(sketch, "E1704", {"start": v(1.7, 29.31) * mm, "end": v(1.8, 30) * mm});
            skLineSegment(sketch, "E1705", {"start": v(1.8, 30) * mm, "end": v(1.9, 30.67) * mm});
            skLineSegment(sketch, "E1706", {"start": v(1.9, 30.67) * mm, "end": v(2, 31.34) * mm});
            skLineSegment(sketch, "E1707", {"start": v(2, 31.34) * mm, "end": v(2.07, 31.98) * mm});
            skLineSegment(sketch, "E1708", {"start": v(2.07, 31.98) * mm, "end": v(2.14, 32.61) * mm});
            skLineSegment(sketch, "E1709", {"start": v(2.14, 32.61) * mm, "end": v(2.18, 33.23) * mm});
            skLineSegment(sketch, "E1710", {"start": v(2.18, 33.23) * mm, "end": v(2.22, 33.82) * mm});
            skLineSegment(sketch, "E1711", {"start": v(2.22, 33.82) * mm, "end": v(2.23, 34.39) * mm});
            skLineSegment(sketch, "E1712", {"start": v(2.23, 34.39) * mm, "end": v(2.23, 34.93) * mm});
            skLineSegment(sketch, "E1713", {"start": v(2.23, 34.93) * mm, "end": v(2.2, 35.45) * mm});
            skLineSegment(sketch, "E1714", {"start": v(2.2, 35.45) * mm, "end": v(2.16, 35.94) * mm});
            skLineSegment(sketch, "E1715", {"start": v(2.16, 35.94) * mm, "end": v(2.1, 36.4) * mm});
            skLineSegment(sketch, "E1716", {"start": v(2.1, 36.4) * mm, "end": v(2.01, 36.84) * mm});
            skLineSegment(sketch, "E1717", {"start": v(2.01, 36.84) * mm, "end": v(1.96, 37.04) * mm});
            skLineSegment(sketch, "E1718", {"start": v(1.96, 37.04) * mm, "end": v(1.9, 37.23) * mm});
            skLineSegment(sketch, "E1719", {"start": v(1.9, 37.23) * mm, "end": v(1.84, 37.42) * mm});
            skLineSegment(sketch, "E1720", {"start": v(1.84, 37.42) * mm, "end": v(1.78, 37.6) * mm});
            skLineSegment(sketch, "E1721", {"start": v(1.78, 37.6) * mm, "end": v(1.65, 37.89) * mm});
            skLineSegment(sketch, "E1722", {"start": v(1.65, 37.89) * mm, "end": v(1.5, 38.17) * mm});
            skLineSegment(sketch, "E1723", {"start": v(1.5, 38.17) * mm, "end": v(1.33, 38.44) * mm});
            skLineSegment(sketch, "E1724", {"start": v(1.33, 38.44) * mm, "end": v(1.14, 38.7) * mm});
            skLineSegment(sketch, "E1725", {"start": v(1.14, 38.7) * mm, "end": v(0.94, 38.95) * mm});
            skLineSegment(sketch, "E1726", {"start": v(0.94, 38.95) * mm, "end": v(0.72, 39.2) * mm});
            skLineSegment(sketch, "E1727", {"start": v(0.72, 39.2) * mm, "end": v(0.49, 39.43) * mm});
            skLineSegment(sketch, "E1728", {"start": v(0.49, 39.43) * mm, "end": v(0.24, 39.65) * mm});
            skLineSegment(sketch, "E1729", {"start": v(0.24, 39.65) * mm, "end": v(-0.02, 39.86) * mm});
            skLineSegment(sketch, "E1730", {"start": v(-0.02, 39.86) * mm, "end": v(-0.29, 40.06) * mm});
            skLineSegment(sketch, "E1731", {"start": v(-0.29, 40.06) * mm, "end": v(-0.57, 40.25) * mm});
            skLineSegment(sketch, "E1732", {"start": v(-0.57, 40.25) * mm, "end": v(-0.86, 40.42) * mm});
            skLineSegment(sketch, "E1733", {"start": v(-0.86, 40.42) * mm, "end": v(-1.16, 40.59) * mm});
            skLineSegment(sketch, "E1734", {"start": v(-1.16, 40.59) * mm, "end": v(-1.46, 40.74) * mm});
            skLineSegment(sketch, "E1735", {"start": v(-1.46, 40.74) * mm, "end": v(-1.77, 40.87) * mm});
            skLineSegment(sketch, "E1736", {"start": v(-1.77, 40.87) * mm, "end": v(-2.1, 41) * mm});
            skLineSegment(sketch, "E1737", {"start": v(-2.1, 41) * mm, "end": v(-2.41, 41.1) * mm});
            skLineSegment(sketch, "E1738", {"start": v(-2.41, 41.1) * mm, "end": v(-2.74, 41.2) * mm});
            skLineSegment(sketch, "E1739", {"start": v(-2.74, 41.2) * mm, "end": v(-3.06, 41.27) * mm});
            skLineSegment(sketch, "E1740", {"start": v(-3.06, 41.27) * mm, "end": v(-3.39, 41.33) * mm});
            skLineSegment(sketch, "E1741", {"start": v(-3.39, 41.33) * mm, "end": v(-3.71, 41.38) * mm});
            skLineSegment(sketch, "E1742", {"start": v(-3.71, 41.38) * mm, "end": v(-4.04, 41.4) * mm});
            skLineSegment(sketch, "E1743", {"start": v(-4.04, 41.4) * mm, "end": v(-4.36, 41.42) * mm});
            skLineSegment(sketch, "E1744", {"start": v(-4.36, 41.42) * mm, "end": v(-4.68, 41.4) * mm});
            skLineSegment(sketch, "E1745", {"start": v(-4.68, 41.4) * mm, "end": v(-5, 41.38) * mm});
            skLineSegment(sketch, "E1746", {"start": v(-5, 41.38) * mm, "end": v(-5.31, 41.34) * mm});
            skLineSegment(sketch, "E1747", {"start": v(-5.31, 41.34) * mm, "end": v(-5.61, 41.28) * mm});
            skLineSegment(sketch, "E1748", {"start": v(-5.61, 41.28) * mm, "end": v(-5.91, 41.2) * mm});
            skLineSegment(sketch, "E1749", {"start": v(-5.91, 41.2) * mm, "end": v(-6.2, 41.1) * mm});
            skLineSegment(sketch, "E1750", {"start": v(-6.2, 41.1) * mm, "end": v(-6.48, 40.97) * mm});
            skLineSegment(sketch, "E1751", {"start": v(-6.48, 40.97) * mm, "end": v(-6.75, 40.83) * mm});
            skLineSegment(sketch, "E1752", {"start": v(-6.75, 40.83) * mm, "end": v(-7, 40.67) * mm});
            skLineSegment(sketch, "E1753", {"start": v(-7, 40.67) * mm, "end": v(-7.25, 40.49) * mm});
            skLineSegment(sketch, "E1754", {"start": v(-7.25, 40.49) * mm, "end": v(-7.48, 40.3) * mm});
            skLineSegment(sketch, "E1755", {"start": v(-7.48, 40.3) * mm, "end": v(-7.71, 40.09) * mm});
            skLineSegment(sketch, "E1756", {"start": v(-7.71, 40.09) * mm, "end": v(-7.93, 39.87) * mm});
            skLineSegment(sketch, "E1757", {"start": v(-7.93, 39.87) * mm, "end": v(-8.15, 39.64) * mm});
            skLineSegment(sketch, "E1758", {"start": v(-8.15, 39.64) * mm, "end": v(-8.35, 39.4) * mm});
            skLineSegment(sketch, "E1759", {"start": v(-8.35, 39.4) * mm, "end": v(-8.55, 39.15) * mm});
            skLineSegment(sketch, "E1760", {"start": v(-8.55, 39.15) * mm, "end": v(-8.74, 38.89) * mm});
            skLineSegment(sketch, "E1761", {"start": v(-8.74, 38.89) * mm, "end": v(-8.93, 38.62) * mm});
            skLineSegment(sketch, "E1762", {"start": v(-8.93, 38.62) * mm, "end": v(-9.1, 38.34) * mm});
            skLineSegment(sketch, "E1763", {"start": v(-9.1, 38.34) * mm, "end": v(-9.28, 38.06) * mm});
            skLineSegment(sketch, "E1764", {"start": v(-9.28, 38.06) * mm, "end": v(-9.45, 37.76) * mm});
            skLineSegment(sketch, "E1765", {"start": v(-9.45, 37.76) * mm, "end": v(-9.77, 37.16) * mm});
            skLineSegment(sketch, "E1766", {"start": v(-9.77, 37.16) * mm, "end": v(-10.07, 36.52) * mm});
            skLineSegment(sketch, "E1767", {"start": v(-10.07, 36.52) * mm, "end": v(-10.36, 35.87) * mm});
            skLineSegment(sketch, "E1768", {"start": v(-10.36, 35.87) * mm, "end": v(-10.63, 35.2) * mm});
            skLineSegment(sketch, "E1769", {"start": v(-10.63, 35.2) * mm, "end": v(-10.9, 34.52) * mm});
            skLineSegment(sketch, "E1770", {"start": v(-10.9, 34.52) * mm, "end": v(-11.16, 33.84) * mm});
            skLineSegment(sketch, "E1771", {"start": v(-11.16, 33.84) * mm, "end": v(-11.66, 32.46) * mm});
            skLineSegment(sketch, "E1772", {"start": v(-11.66, 32.46) * mm, "end": v(-12.16, 31.1) * mm});
            skLineSegment(sketch, "E1773", {"start": v(-12.16, 31.1) * mm, "end": v(-12.44, 30.4) * mm});
            skLineSegment(sketch, "E1774", {"start": v(-12.44, 30.4) * mm, "end": v(-12.73, 29.73) * mm});
            skLineSegment(sketch, "E1775", {"start": v(-12.73, 29.73) * mm, "end": v(-13.03, 29.07) * mm});
            skLineSegment(sketch, "E1776", {"start": v(-13.03, 29.07) * mm, "end": v(-13.35, 28.44) * mm});
            skLineSegment(sketch, "E1777", {"start": v(-13.35, 28.44) * mm, "end": v(-13.68, 27.82) * mm});
            skLineSegment(sketch, "E1778", {"start": v(-13.68, 27.82) * mm, "end": v(-14.03, 27.24) * mm});
            skLineSegment(sketch, "E1779", {"start": v(-14.03, 27.24) * mm, "end": v(-14.22, 26.96) * mm});
            skLineSegment(sketch, "E1780", {"start": v(-14.22, 26.96) * mm, "end": v(-14.4, 26.68) * mm});
            skLineSegment(sketch, "E1781", {"start": v(-14.4, 26.68) * mm, "end": v(-14.6, 26.42) * mm});
            skLineSegment(sketch, "E1782", {"start": v(-14.6, 26.42) * mm, "end": v(-14.8, 26.16) * mm});
            skLineSegment(sketch, "E1783", {"start": v(-14.8, 26.16) * mm, "end": v(-15, 25.91) * mm});
            skLineSegment(sketch, "E1784", {"start": v(-15, 25.91) * mm, "end": v(-15.2, 25.67) * mm});
            skLineSegment(sketch, "E1785", {"start": v(-15.2, 25.67) * mm, "end": v(-15.42, 25.44) * mm});
            skLineSegment(sketch, "E1786", {"start": v(-15.42, 25.44) * mm, "end": v(-15.64, 25.22) * mm});
            skLineSegment(sketch, "E1787", {"start": v(-15.64, 25.22) * mm, "end": v(-15.86, 25.01) * mm});
            skLineSegment(sketch, "E1788", {"start": v(-15.86, 25.01) * mm, "end": v(-16.09, 24.81) * mm});
            skLineSegment(sketch, "E1789", {"start": v(-16.09, 24.81) * mm, "end": v(-16.32, 24.62) * mm});
            skLineSegment(sketch, "E1790", {"start": v(-16.32, 24.62) * mm, "end": v(-16.56, 24.44) * mm});
            skLineSegment(sketch, "E1791", {"start": v(-16.56, 24.44) * mm, "end": v(-16.8, 24.28) * mm});
            skLineSegment(sketch, "E1792", {"start": v(-16.8, 24.28) * mm, "end": v(-17.06, 24.12) * mm});
            skLineSegment(sketch, "E1793", {"start": v(-17.06, 24.12) * mm, "end": v(-17.32, 23.98) * mm});
            skLineSegment(sketch, "E1794", {"start": v(-17.32, 23.98) * mm, "end": v(-17.58, 23.85) * mm});
            skLineSegment(sketch, "E1795", {"start": v(-17.58, 23.85) * mm, "end": v(-17.85, 23.73) * mm});
            skLineSegment(sketch, "E1796", {"start": v(-17.85, 23.73) * mm, "end": v(-18.13, 23.62) * mm});
            skLineSegment(sketch, "E1797", {"start": v(-18.13, 23.62) * mm, "end": v(-18.4, 23.53) * mm});
            skLineSegment(sketch, "E1798", {"start": v(-18.4, 23.53) * mm, "end": v(-18.7, 23.45) * mm});
            skLineSegment(sketch, "E1799", {"start": v(-18.7, 23.45) * mm, "end": v(-19.03, 23.39) * mm});
            skLineSegment(sketch, "E1800", {"start": v(-19.03, 23.39) * mm, "end": v(-19.38, 23.34) * mm});
            skLineSegment(sketch, "E1801", {"start": v(-19.38, 23.34) * mm, "end": v(-19.73, 23.3) * mm});
            skLineSegment(sketch, "E1802", {"start": v(-19.73, 23.3) * mm, "end": v(-20.1, 23.3) * mm});
            skLineSegment(sketch, "E1803", {"start": v(-20.1, 23.3) * mm, "end": v(-20.46, 23.31) * mm});
            skLineSegment(sketch, "E1804", {"start": v(-20.46, 23.31) * mm, "end": v(-20.83, 23.34) * mm});
            skLineSegment(sketch, "E1805", {"start": v(-20.83, 23.34) * mm, "end": v(-21.2, 23.39) * mm});
            skLineSegment(sketch, "E1806", {"start": v(-21.2, 23.39) * mm, "end": v(-21.58, 23.45) * mm});
            skLineSegment(sketch, "E1807", {"start": v(-21.58, 23.45) * mm, "end": v(-21.96, 23.54) * mm});
            skLineSegment(sketch, "E1808", {"start": v(-21.96, 23.54) * mm, "end": v(-22.33, 23.64) * mm});
            skLineSegment(sketch, "E1809", {"start": v(-22.33, 23.64) * mm, "end": v(-22.7, 23.75) * mm});
            skLineSegment(sketch, "E1810", {"start": v(-22.7, 23.75) * mm, "end": v(-23.05, 23.88) * mm});
            skLineSegment(sketch, "E1811", {"start": v(-23.05, 23.88) * mm, "end": v(-23.4, 24.03) * mm});
            skLineSegment(sketch, "E1812", {"start": v(-23.4, 24.03) * mm, "end": v(-23.73, 24.2) * mm});
            skLineSegment(sketch, "E1813", {"start": v(-23.73, 24.2) * mm, "end": v(-24.06, 24.37) * mm});
            skLineSegment(sketch, "E1814", {"start": v(-24.06, 24.37) * mm, "end": v(-24.37, 24.56) * mm});
            skLineSegment(sketch, "E1815", {"start": v(-24.37, 24.56) * mm, "end": v(-24.6, 24.72) * mm});
            skLineSegment(sketch, "E1816", {"start": v(-24.6, 24.72) * mm, "end": v(-24.82, 24.88) * mm});
            skLineSegment(sketch, "E1817", {"start": v(-24.82, 24.88) * mm, "end": v(-25.03, 25.05) * mm});
            skLineSegment(sketch, "E1818", {"start": v(-25.03, 25.05) * mm, "end": v(-25.23, 25.23) * mm});
            skLineSegment(sketch, "E1819", {"start": v(-25.23, 25.23) * mm, "end": v(-25.42, 25.42) * mm});
            skLineSegment(sketch, "E1820", {"start": v(-25.42, 25.42) * mm, "end": v(-25.6, 25.61) * mm});
            skLineSegment(sketch, "E1821", {"start": v(-25.6, 25.61) * mm, "end": v(-25.77, 25.81) * mm});
            skLineSegment(sketch, "E1822", {"start": v(-25.77, 25.81) * mm, "end": v(-25.93, 26.02) * mm});
            skLineSegment(sketch, "E1823", {"start": v(-25.93, 26.02) * mm, "end": v(-26.09, 26.23) * mm});
            skLineSegment(sketch, "E1824", {"start": v(-26.09, 26.23) * mm, "end": v(-26.23, 26.45) * mm});
            skLineSegment(sketch, "E1825", {"start": v(-26.23, 26.45) * mm, "end": v(-26.37, 26.68) * mm});
            skLineSegment(sketch, "E1826", {"start": v(-26.37, 26.68) * mm, "end": v(-26.5, 26.9) * mm});
            skLineSegment(sketch, "E1827", {"start": v(-26.5, 26.9) * mm, "end": v(-26.62, 27.15) * mm});
            skLineSegment(sketch, "E1828", {"start": v(-26.62, 27.15) * mm, "end": v(-26.73, 27.39) * mm});
            skLineSegment(sketch, "E1829", {"start": v(-26.73, 27.39) * mm, "end": v(-26.84, 27.64) * mm});
            skLineSegment(sketch, "E1830", {"start": v(-26.84, 27.64) * mm, "end": v(-26.93, 27.9) * mm});
            skLineSegment(sketch, "E1831", {"start": v(-26.93, 27.9) * mm, "end": v(-27.02, 28.15) * mm});
            skLineSegment(sketch, "E1832", {"start": v(-27.02, 28.15) * mm, "end": v(-27.1, 28.42) * mm});
            skLineSegment(sketch, "E1833", {"start": v(-27.1, 28.42) * mm, "end": v(-27.18, 28.68) * mm});
            skLineSegment(sketch, "E1834", {"start": v(-27.18, 28.68) * mm, "end": v(-27.25, 28.96) * mm});
            skLineSegment(sketch, "E1835", {"start": v(-27.25, 28.96) * mm, "end": v(-27.3, 29.24) * mm});
            skLineSegment(sketch, "E1836", {"start": v(-27.3, 29.24) * mm, "end": v(-27.36, 29.52) * mm});
            skLineSegment(sketch, "E1837", {"start": v(-27.36, 29.52) * mm, "end": v(-27.44, 30.1) * mm});
            skLineSegment(sketch, "E1838", {"start": v(-27.44, 30.1) * mm, "end": v(-27.5, 30.69) * mm});
            skLineSegment(sketch, "E1839", {"start": v(-27.5, 30.69) * mm, "end": v(-27.53, 31.3) * mm});
            skLineSegment(sketch, "E1840", {"start": v(-27.53, 31.3) * mm, "end": v(-27.54, 31.9) * mm});
            skLineSegment(sketch, "E1841", {"start": v(-27.54, 31.9) * mm, "end": v(-27.52, 32.54) * mm});
            skLineSegment(sketch, "E1842", {"start": v(13.38, 16.64) * mm, "end": v(13.38, 16.64) * mm});
            skLineSegment(sketch, "E1843", {"start": v(13.38, 16.64) * mm, "end": v(13.1, 15.64) * mm});
            skLineSegment(sketch, "E1844", {"start": v(13.1, 15.64) * mm, "end": v(-0.22, 13.64) * mm});
            skLineSegment(sketch, "E1845", {"start": v(-0.22, 13.64) * mm, "end": v(0.27, 15.5) * mm});
            skLineSegment(sketch, "E1846", {"start": v(0.27, 15.5) * mm, "end": v(0.7, 17.05) * mm});
            skLineSegment(sketch, "E1847", {"start": v(0.7, 17.05) * mm, "end": v(0.68, 17.06) * mm});
            skLineSegment(sketch, "E1848", {"start": v(0.68, 17.06) * mm, "end": v(2.38, 23.51) * mm});
            skLineSegment(sketch, "E1849", {"start": v(2.38, 23.51) * mm, "end": v(15.77, 25.77) * mm});
            skLineSegment(sketch, "E1850", {"start": v(15.77, 25.77) * mm, "end": v(13.38, 16.64) * mm});
            skLineSegment(sketch, "E1851", {"start": v(-13.42, 33.26) * mm, "end": v(-24.9, 36.93) * mm});
            skLineSegment(sketch, "E1852", {"start": v(-24.9, 36.93) * mm, "end": v(-25.05, 36.54) * mm});
            skLineSegment(sketch, "E1853", {"start": v(-25.05, 36.54) * mm, "end": v(-25.17, 36.13) * mm});
            skLineSegment(sketch, "E1854", {"start": v(-25.17, 36.13) * mm, "end": v(-25.29, 35.7) * mm});
            skLineSegment(sketch, "E1855", {"start": v(-25.29, 35.7) * mm, "end": v(-25.39, 35.27) * mm});
            skLineSegment(sketch, "E1856", {"start": v(-25.39, 35.27) * mm, "end": v(-25.48, 34.82) * mm});
            skLineSegment(sketch, "E1857", {"start": v(-25.48, 34.82) * mm, "end": v(-25.55, 34.37) * mm});
            skLineSegment(sketch, "E1858", {"start": v(-25.55, 34.37) * mm, "end": v(-25.62, 33.9) * mm});
            skLineSegment(sketch, "E1859", {"start": v(-25.62, 33.9) * mm, "end": v(-25.67, 33.45) * mm});
            skLineSegment(sketch, "E1860", {"start": v(-25.67, 33.45) * mm, "end": v(-25.7, 33) * mm});
            skLineSegment(sketch, "E1861", {"start": v(-25.7, 33) * mm, "end": v(-25.74, 32.54) * mm});
            skLineSegment(sketch, "E1862", {"start": v(-25.74, 32.54) * mm, "end": v(-25.75, 32.1) * mm});
            skLineSegment(sketch, "E1863", {"start": v(-25.75, 32.1) * mm, "end": v(-25.75, 31.66) * mm});
            skLineSegment(sketch, "E1864", {"start": v(-25.75, 31.66) * mm, "end": v(-25.74, 31.24) * mm});
            skLineSegment(sketch, "E1865", {"start": v(-25.74, 31.24) * mm, "end": v(-25.72, 30.83) * mm});
            skLineSegment(sketch, "E1866", {"start": v(-25.72, 30.83) * mm, "end": v(-25.69, 30.45) * mm});
            skLineSegment(sketch, "E1867", {"start": v(-25.69, 30.45) * mm, "end": v(-25.64, 30.09) * mm});
            skLineSegment(sketch, "E1868", {"start": v(-25.64, 30.09) * mm, "end": v(-25.58, 29.72) * mm});
            skLineSegment(sketch, "E1869", {"start": v(-25.58, 29.72) * mm, "end": v(-25.5, 29.36) * mm});
            skLineSegment(sketch, "E1870", {"start": v(-25.5, 29.36) * mm, "end": v(-25.42, 29) * mm});
            skLineSegment(sketch, "E1871", {"start": v(-25.42, 29) * mm, "end": v(-25.32, 28.65) * mm});
            skLineSegment(sketch, "E1872", {"start": v(-25.32, 28.65) * mm, "end": v(-25.2, 28.3) * mm});
            skLineSegment(sketch, "E1873", {"start": v(-25.2, 28.3) * mm, "end": v(-25.05, 27.98) * mm});
            skLineSegment(sketch, "E1874", {"start": v(-25.05, 27.98) * mm, "end": v(-24.9, 27.66) * mm});
            skLineSegment(sketch, "E1875", {"start": v(-24.9, 27.66) * mm, "end": v(-24.7, 27.35) * mm});
            skLineSegment(sketch, "E1876", {"start": v(-24.7, 27.35) * mm, "end": v(-24.6, 27.2) * mm});
            skLineSegment(sketch, "E1877", {"start": v(-24.6, 27.2) * mm, "end": v(-24.5, 27.06) * mm});
            skLineSegment(sketch, "E1878", {"start": v(-24.5, 27.06) * mm, "end": v(-24.38, 26.91) * mm});
            skLineSegment(sketch, "E1879", {"start": v(-24.38, 26.91) * mm, "end": v(-24.25, 26.78) * mm});
            skLineSegment(sketch, "E1880", {"start": v(-24.25, 26.78) * mm, "end": v(-24.12, 26.64) * mm});
            skLineSegment(sketch, "E1881", {"start": v(-24.12, 26.64) * mm, "end": v(-23.98, 26.51) * mm});
            skLineSegment(sketch, "E1882", {"start": v(-23.98, 26.51) * mm, "end": v(-23.83, 26.39) * mm});
            skLineSegment(sketch, "E1883", {"start": v(-23.83, 26.39) * mm, "end": v(-23.68, 26.26) * mm});
            skLineSegment(sketch, "E1884", {"start": v(-23.68, 26.26) * mm, "end": v(-23.51, 26.15) * mm});
            skLineSegment(sketch, "E1885", {"start": v(-23.51, 26.15) * mm, "end": v(-23.34, 26.03) * mm});
            skLineSegment(sketch, "E1886", {"start": v(-23.34, 26.03) * mm, "end": v(-23.16, 25.93) * mm});
            skLineSegment(sketch, "E1887", {"start": v(-23.16, 25.93) * mm, "end": v(-22.96, 25.82) * mm});
            skLineSegment(sketch, "E1888", {"start": v(-22.96, 25.82) * mm, "end": v(-22.76, 25.73) * mm});
            skLineSegment(sketch, "E1889", {"start": v(-22.76, 25.73) * mm, "end": v(-22.55, 25.63) * mm});
            skLineSegment(sketch, "E1890", {"start": v(-22.55, 25.63) * mm, "end": v(-22.33, 25.55) * mm});
            skLineSegment(sketch, "E1891", {"start": v(-22.33, 25.55) * mm, "end": v(-22.1, 25.47) * mm});
            skLineSegment(sketch, "E1892", {"start": v(-22.1, 25.47) * mm, "end": v(-21.6, 25.32) * mm});
            skLineSegment(sketch, "E1893", {"start": v(-21.6, 25.32) * mm, "end": v(-21.36, 25.26) * mm});
            skLineSegment(sketch, "E1894", {"start": v(-21.36, 25.26) * mm, "end": v(-21.13, 25.2) * mm});
            skLineSegment(sketch, "E1895", {"start": v(-21.13, 25.2) * mm, "end": v(-20.9, 25.17) * mm});
            skLineSegment(sketch, "E1896", {"start": v(-20.9, 25.17) * mm, "end": v(-20.68, 25.14) * mm});
            skLineSegment(sketch, "E1897", {"start": v(-20.68, 25.14) * mm, "end": v(-20.47, 25.11) * mm});
            skLineSegment(sketch, "E1898", {"start": v(-20.47, 25.11) * mm, "end": v(-20.26, 25.1) * mm});
            skLineSegment(sketch, "E1899", {"start": v(-20.26, 25.1) * mm, "end": v(-20.06, 25.1) * mm});
            skLineSegment(sketch, "E1900", {"start": v(-20.06, 25.1) * mm, "end": v(-19.86, 25.1) * mm});
            skLineSegment(sketch, "E1901", {"start": v(-19.86, 25.1) * mm, "end": v(-19.67, 25.11) * mm});
            skLineSegment(sketch, "E1902", {"start": v(-19.67, 25.11) * mm, "end": v(-19.48, 25.13) * mm});
            skLineSegment(sketch, "E1903", {"start": v(-19.48, 25.13) * mm, "end": v(-19.3, 25.16) * mm});
            skLineSegment(sketch, "E1904", {"start": v(-19.3, 25.16) * mm, "end": v(-19.13, 25.2) * mm});
            skLineSegment(sketch, "E1905", {"start": v(-19.13, 25.2) * mm, "end": v(-18.95, 25.24) * mm});
            skLineSegment(sketch, "E1906", {"start": v(-18.95, 25.24) * mm, "end": v(-18.79, 25.3) * mm});
            skLineSegment(sketch, "E1907", {"start": v(-18.79, 25.3) * mm, "end": v(-18.62, 25.35) * mm});
            skLineSegment(sketch, "E1908", {"start": v(-18.62, 25.35) * mm, "end": v(-18.46, 25.42) * mm});
            skLineSegment(sketch, "E1909", {"start": v(-18.46, 25.42) * mm, "end": v(-18.15, 25.57) * mm});
            skLineSegment(sketch, "E1910", {"start": v(-18.15, 25.57) * mm, "end": v(-17.85, 25.75) * mm});
            skLineSegment(sketch, "E1911", {"start": v(-17.85, 25.75) * mm, "end": v(-17.57, 25.95) * mm});
            skLineSegment(sketch, "E1912", {"start": v(-17.57, 25.95) * mm, "end": v(-17.3, 26.17) * mm});
            skLineSegment(sketch, "E1913", {"start": v(-17.3, 26.17) * mm, "end": v(-17.02, 26.42) * mm});
            skLineSegment(sketch, "E1914", {"start": v(-17.02, 26.42) * mm, "end": v(-16.76, 26.68) * mm});
            skLineSegment(sketch, "E1915", {"start": v(-16.76, 26.68) * mm, "end": v(-16.5, 26.97) * mm});
            skLineSegment(sketch, "E1916", {"start": v(-16.5, 26.97) * mm, "end": v(-16.26, 27.25) * mm});
            skLineSegment(sketch, "E1917", {"start": v(-16.26, 27.25) * mm, "end": v(-16.02, 27.56) * mm});
            skLineSegment(sketch, "E1918", {"start": v(-16.02, 27.56) * mm, "end": v(-15.78, 27.9) * mm});
            skLineSegment(sketch, "E1919", {"start": v(-15.78, 27.9) * mm, "end": v(-15.54, 28.26) * mm});
            skLineSegment(sketch, "E1920", {"start": v(-15.54, 28.26) * mm, "end": v(-15.3, 28.64) * mm});
            skLineSegment(sketch, "E1921", {"start": v(-15.3, 28.64) * mm, "end": v(-15.06, 29.04) * mm});
            skLineSegment(sketch, "E1922", {"start": v(-15.06, 29.04) * mm, "end": v(-14.84, 29.45) * mm});
            skLineSegment(sketch, "E1923", {"start": v(-14.84, 29.45) * mm, "end": v(-14.62, 29.87) * mm});
            skLineSegment(sketch, "E1924", {"start": v(-14.62, 29.87) * mm, "end": v(-14.4, 30.3) * mm});
            skLineSegment(sketch, "E1925", {"start": v(-14.4, 30.3) * mm, "end": v(-14.21, 30.73) * mm});
            skLineSegment(sketch, "E1926", {"start": v(-14.21, 30.73) * mm, "end": v(-14.03, 31.17) * mm});
            skLineSegment(sketch, "E1927", {"start": v(-14.03, 31.17) * mm, "end": v(-13.87, 31.6) * mm});
            skLineSegment(sketch, "E1928", {"start": v(-13.87, 31.6) * mm, "end": v(-13.72, 32.03) * mm});
            skLineSegment(sketch, "E1929", {"start": v(-13.72, 32.03) * mm, "end": v(-13.6, 32.45) * mm});
            skLineSegment(sketch, "E1930", {"start": v(-13.6, 32.45) * mm, "end": v(-13.5, 32.86) * mm});
            skLineSegment(sketch, "E1931", {"start": v(-13.5, 32.86) * mm, "end": v(-13.42, 33.26) * mm});
            skLineSegment(sketch, "E1932", {"start": v(-17.64, 51.15) * mm, "end": v(-17.41, 50.85) * mm});
            skLineSegment(sketch, "E1933", {"start": v(-17.41, 50.85) * mm, "end": v(-17.2, 50.53) * mm});
            skLineSegment(sketch, "E1934", {"start": v(-17.2, 50.53) * mm, "end": v(-16.77, 49.88) * mm});
            skLineSegment(sketch, "E1935", {"start": v(-16.77, 49.88) * mm, "end": v(-16.33, 49.21) * mm});
            skLineSegment(sketch, "E1936", {"start": v(-16.33, 49.21) * mm, "end": v(-15.88, 48.53) * mm});
            skLineSegment(sketch, "E1937", {"start": v(-15.88, 48.53) * mm, "end": v(-10.11, 40.27) * mm});
            skLineSegment(sketch, "E1938", {"start": v(-10.11, 40.27) * mm, "end": v(-9.56, 40.74) * mm});
            skLineSegment(sketch, "E1939", {"start": v(-9.56, 40.74) * mm, "end": v(-9.12, 41.14) * mm});
            skLineSegment(sketch, "E1940", {"start": v(-9.12, 41.14) * mm, "end": v(-8.49, 41.74) * mm});
            skLineSegment(sketch, "E1941", {"start": v(-8.49, 41.74) * mm, "end": v(-8.08, 42.15) * mm});
            skLineSegment(sketch, "E1942", {"start": v(-8.08, 42.15) * mm, "end": v(-7.91, 42.3) * mm});
            skLineSegment(sketch, "E1943", {"start": v(-7.91, 42.3) * mm, "end": v(-7.75, 42.42) * mm});
            skLineSegment(sketch, "E1944", {"start": v(-7.75, 42.42) * mm, "end": v(-7.56, 42.52) * mm});
            skLineSegment(sketch, "E1945", {"start": v(-7.56, 42.52) * mm, "end": v(-7.34, 42.61) * mm});
            skLineSegment(sketch, "E1946", {"start": v(-7.34, 42.61) * mm, "end": v(-7.06, 42.7) * mm});
            skLineSegment(sketch, "E1947", {"start": v(-7.06, 42.7) * mm, "end": v(-6.72, 42.8) * mm});
            skLineSegment(sketch, "E1948", {"start": v(-6.72, 42.8) * mm, "end": v(-5.73, 43.03) * mm});
            skLineSegment(sketch, "E1949", {"start": v(-5.73, 43.03) * mm, "end": v(-4.23, 43.39) * mm});
            skLineSegment(sketch, "E1950", {"start": v(-4.23, 43.39) * mm, "end": v(-3.96, 57.43) * mm});
            skLineSegment(sketch, "E1951", {"start": v(-3.96, 57.43) * mm, "end": v(-4.39, 57.44) * mm});
            skLineSegment(sketch, "E1952", {"start": v(-4.39, 57.44) * mm, "end": v(-4.85, 57.41) * mm});
            skLineSegment(sketch, "E1953", {"start": v(-4.85, 57.41) * mm, "end": v(-5.33, 57.36) * mm});
            skLineSegment(sketch, "E1954", {"start": v(-5.33, 57.36) * mm, "end": v(-5.84, 57.28) * mm});
            skLineSegment(sketch, "E1955", {"start": v(-5.84, 57.28) * mm, "end": v(-6.36, 57.18) * mm});
            skLineSegment(sketch, "E1956", {"start": v(-6.36, 57.18) * mm, "end": v(-6.9, 57.07) * mm});
            skLineSegment(sketch, "E1957", {"start": v(-6.9, 57.07) * mm, "end": v(-7.43, 56.94) * mm});
            skLineSegment(sketch, "E1958", {"start": v(-7.43, 56.94) * mm, "end": v(-7.96, 56.8) * mm});
            skLineSegment(sketch, "E1959", {"start": v(-7.96, 56.8) * mm, "end": v(-8.49, 56.64) * mm});
            skLineSegment(sketch, "E1960", {"start": v(-8.49, 56.64) * mm, "end": v(-9, 56.47) * mm});
            skLineSegment(sketch, "E1961", {"start": v(-9, 56.47) * mm, "end": v(-9.5, 56.3) * mm});
            skLineSegment(sketch, "E1962", {"start": v(-9.5, 56.3) * mm, "end": v(-9.96, 56.14) * mm});
            skLineSegment(sketch, "E1963", {"start": v(-9.96, 56.14) * mm, "end": v(-10.4, 55.97) * mm});
            skLineSegment(sketch, "E1964", {"start": v(-10.4, 55.97) * mm, "end": v(-10.8, 55.8) * mm});
            skLineSegment(sketch, "E1965", {"start": v(-10.8, 55.8) * mm, "end": v(-11.15, 55.64) * mm});
            skLineSegment(sketch, "E1966", {"start": v(-11.15, 55.64) * mm, "end": v(-11.47, 55.48) * mm});
            skLineSegment(sketch, "E1967", {"start": v(-11.47, 55.48) * mm, "end": v(-12.22, 55.09) * mm});
            skLineSegment(sketch, "E1968", {"start": v(-12.22, 55.09) * mm, "end": v(-13, 54.66) * mm});
            skLineSegment(sketch, "E1969", {"start": v(-13, 54.66) * mm, "end": v(-13.8, 54.2) * mm});
            skLineSegment(sketch, "E1970", {"start": v(-13.8, 54.2) * mm, "end": v(-14.21, 53.96) * mm});
            skLineSegment(sketch, "E1971", {"start": v(-14.21, 53.96) * mm, "end": v(-14.61, 53.7) * mm});
            skLineSegment(sketch, "E1972", {"start": v(-14.61, 53.7) * mm, "end": v(-15.02, 53.44) * mm});
            skLineSegment(sketch, "E1973", {"start": v(-15.02, 53.44) * mm, "end": v(-15.41, 53.16) * mm});
            skLineSegment(sketch, "E1974", {"start": v(-15.41, 53.16) * mm, "end": v(-15.8, 52.87) * mm});
            skLineSegment(sketch, "E1975", {"start": v(-15.8, 52.87) * mm, "end": v(-16.2, 52.56) * mm});
            skLineSegment(sketch, "E1976", {"start": v(-16.2, 52.56) * mm, "end": v(-16.57, 52.23) * mm});
            skLineSegment(sketch, "E1977", {"start": v(-16.57, 52.23) * mm, "end": v(-16.94, 51.89) * mm});
            skLineSegment(sketch, "E1978", {"start": v(-16.94, 51.89) * mm, "end": v(-17.3, 51.53) * mm});
            skLineSegment(sketch, "E1979", {"start": v(-17.3, 51.53) * mm, "end": v(-17.64, 51.15) * mm});
            skLineSegment(sketch, "E1980", {"start": v(2.05, 40.4) * mm, "end": v(2.23, 40.25) * mm});
            skLineSegment(sketch, "E1981", {"start": v(2.23, 40.25) * mm, "end": v(2.4, 40.1) * mm});
            skLineSegment(sketch, "E1982", {"start": v(2.4, 40.1) * mm, "end": v(2.55, 39.93) * mm});
            skLineSegment(sketch, "E1983", {"start": v(2.55, 39.93) * mm, "end": v(2.7, 39.76) * mm});
            skLineSegment(sketch, "E1984", {"start": v(2.7, 39.76) * mm, "end": v(2.82, 39.58) * mm});
            skLineSegment(sketch, "E1985", {"start": v(2.82, 39.58) * mm, "end": v(2.94, 39.4) * mm});
            skLineSegment(sketch, "E1986", {"start": v(2.94, 39.4) * mm, "end": v(3.06, 39.21) * mm});
            skLineSegment(sketch, "E1987", {"start": v(3.06, 39.21) * mm, "end": v(3.16, 39.02) * mm});
            skLineSegment(sketch, "E1988", {"start": v(3.16, 39.02) * mm, "end": v(3.26, 38.82) * mm});
            skLineSegment(sketch, "E1989", {"start": v(3.26, 38.82) * mm, "end": v(3.35, 38.62) * mm});
            skLineSegment(sketch, "E1990", {"start": v(3.35, 38.62) * mm, "end": v(3.5, 38.2) * mm});
            skLineSegment(sketch, "E1991", {"start": v(3.5, 38.2) * mm, "end": v(3.62, 37.78) * mm});
            skLineSegment(sketch, "E1992", {"start": v(3.62, 37.78) * mm, "end": v(3.73, 37.35) * mm});
            skLineSegment(sketch, "E1993", {"start": v(3.73, 37.35) * mm, "end": v(3.81, 36.92) * mm});
            skLineSegment(sketch, "E1994", {"start": v(3.81, 36.92) * mm, "end": v(3.88, 36.49) * mm});
            skLineSegment(sketch, "E1995", {"start": v(3.88, 36.49) * mm, "end": v(3.99, 35.66) * mm});
            skLineSegment(sketch, "E1996", {"start": v(3.99, 35.66) * mm, "end": v(4.08, 34.9) * mm});
            skLineSegment(sketch, "E1997", {"start": v(4.08, 34.9) * mm, "end": v(4.13, 34.55) * mm});
            skLineSegment(sketch, "E1998", {"start": v(4.13, 34.55) * mm, "end": v(4.18, 34.23) * mm});
            skLineSegment(sketch, "E1999", {"start": v(4.18, 34.23) * mm, "end": v(4.29, 34.23) * mm});
            skLineSegment(sketch, "E2000", {"start": v(4.29, 34.23) * mm, "end": v(4.45, 34.25) * mm});
            skLineSegment(sketch, "E2001", {"start": v(4.45, 34.25) * mm, "end": v(4.92, 34.31) * mm});
            skLineSegment(sketch, "E2002", {"start": v(4.92, 34.31) * mm, "end": v(5.56, 34.42) * mm});
            skLineSegment(sketch, "E2003", {"start": v(5.56, 34.42) * mm, "end": v(6.36, 34.57) * mm});
            skLineSegment(sketch, "E2004", {"start": v(6.36, 34.57) * mm, "end": v(8.27, 34.95) * mm});
            skLineSegment(sketch, "E2005", {"start": v(8.27, 34.95) * mm, "end": v(10.42, 35.4) * mm});
            skLineSegment(sketch, "E2006", {"start": v(10.42, 35.4) * mm, "end": v(12.6, 35.86) * mm});
            skLineSegment(sketch, "E2007", {"start": v(12.6, 35.86) * mm, "end": v(14.54, 36.3) * mm});
            skLineSegment(sketch, "E2008", {"start": v(14.54, 36.3) * mm, "end": v(16.05, 36.64) * mm});
            skLineSegment(sketch, "E2009", {"start": v(16.05, 36.64) * mm, "end": v(16.57, 36.77) * mm});
            skLineSegment(sketch, "E2010", {"start": v(16.57, 36.77) * mm, "end": v(16.89, 36.86) * mm});
            skLineSegment(sketch, "E2011", {"start": v(16.89, 36.86) * mm, "end": v(16.9, 37.38) * mm});
            skLineSegment(sketch, "E2012", {"start": v(16.9, 37.38) * mm, "end": v(16.9, 37.9) * mm});
            skLineSegment(sketch, "E2013", {"start": v(16.9, 37.9) * mm, "end": v(16.89, 38.44) * mm});
            skLineSegment(sketch, "E2014", {"start": v(16.89, 38.44) * mm, "end": v(16.86, 38.97) * mm});
            skLineSegment(sketch, "E2015", {"start": v(16.86, 38.97) * mm, "end": v(16.82, 39.52) * mm});
            skLineSegment(sketch, "E2016", {"start": v(16.82, 39.52) * mm, "end": v(16.76, 40.06) * mm});
            skLineSegment(sketch, "E2017", {"start": v(16.76, 40.06) * mm, "end": v(16.69, 40.61) * mm});
            skLineSegment(sketch, "E2018", {"start": v(16.69, 40.61) * mm, "end": v(16.6, 41.16) * mm});
            skLineSegment(sketch, "E2019", {"start": v(16.6, 41.16) * mm, "end": v(16.5, 41.71) * mm});
            skLineSegment(sketch, "E2020", {"start": v(16.5, 41.71) * mm, "end": v(16.4, 42.26) * mm});
            skLineSegment(sketch, "E2021", {"start": v(16.4, 42.26) * mm, "end": v(16.27, 42.81) * mm});
            skLineSegment(sketch, "E2022", {"start": v(16.27, 42.81) * mm, "end": v(16.13, 43.36) * mm});
            skLineSegment(sketch, "E2023", {"start": v(16.13, 43.36) * mm, "end": v(15.99, 43.9) * mm});
            skLineSegment(sketch, "E2024", {"start": v(15.99, 43.9) * mm, "end": v(15.83, 44.44) * mm});
            skLineSegment(sketch, "E2025", {"start": v(15.83, 44.44) * mm, "end": v(15.66, 44.97) * mm});
            skLineSegment(sketch, "E2026", {"start": v(15.66, 44.97) * mm, "end": v(15.48, 45.5) * mm});
            skLineSegment(sketch, "E2027", {"start": v(15.48, 45.5) * mm, "end": v(15.29, 46) * mm});
            skLineSegment(sketch, "E2028", {"start": v(15.29, 46) * mm, "end": v(15.09, 46.51) * mm});
            skLineSegment(sketch, "E2029", {"start": v(15.09, 46.51) * mm, "end": v(14.88, 47.01) * mm});
            skLineSegment(sketch, "E2030", {"start": v(14.88, 47.01) * mm, "end": v(14.66, 47.5) * mm});
            skLineSegment(sketch, "E2031", {"start": v(14.66, 47.5) * mm, "end": v(14.43, 47.97) * mm});
            skLineSegment(sketch, "E2032", {"start": v(14.43, 47.97) * mm, "end": v(14.2, 48.43) * mm});
            skLineSegment(sketch, "E2033", {"start": v(14.2, 48.43) * mm, "end": v(13.96, 48.88) * mm});
            skLineSegment(sketch, "E2034", {"start": v(13.96, 48.88) * mm, "end": v(13.7, 49.31) * mm});
            skLineSegment(sketch, "E2035", {"start": v(13.7, 49.31) * mm, "end": v(13.45, 49.73) * mm});
            skLineSegment(sketch, "E2036", {"start": v(13.45, 49.73) * mm, "end": v(13.18, 50.12) * mm});
            skLineSegment(sketch, "E2037", {"start": v(13.18, 50.12) * mm, "end": v(12.9, 50.5) * mm});
            skLineSegment(sketch, "E2038", {"start": v(12.9, 50.5) * mm, "end": v(12.63, 50.86) * mm});
            skLineSegment(sketch, "E2039", {"start": v(12.63, 50.86) * mm, "end": v(12.35, 51.2) * mm});
            skLineSegment(sketch, "E2040", {"start": v(12.35, 51.2) * mm, "end": v(12.06, 51.52) * mm});
            skLineSegment(sketch, "E2041", {"start": v(12.06, 51.52) * mm, "end": v(11.76, 51.81) * mm});
            skLineSegment(sketch, "E2042", {"start": v(11.76, 51.81) * mm, "end": v(11.46, 52.08) * mm});
            skLineSegment(sketch, "E2043", {"start": v(11.46, 52.08) * mm, "end": v(2.05, 40.4) * mm});
            skSolve(sketch);
        }
        {
            var Q0;
            Q0=makeQuery(id+"F0.imprint","IMPRINT",FACE,{"disambiguationData":[TD([[makeQuery(id+"F0.imprint","IMPRINT",EDGE,{"derivedFrom":sQuery(id+"F0.wireOp",EDGE,"E0")}),1.0]])]});
            extrude(context, id + "F1", {"entities" : qUnion([Q0]), "depth" : 3 * mm});
        }
    });
